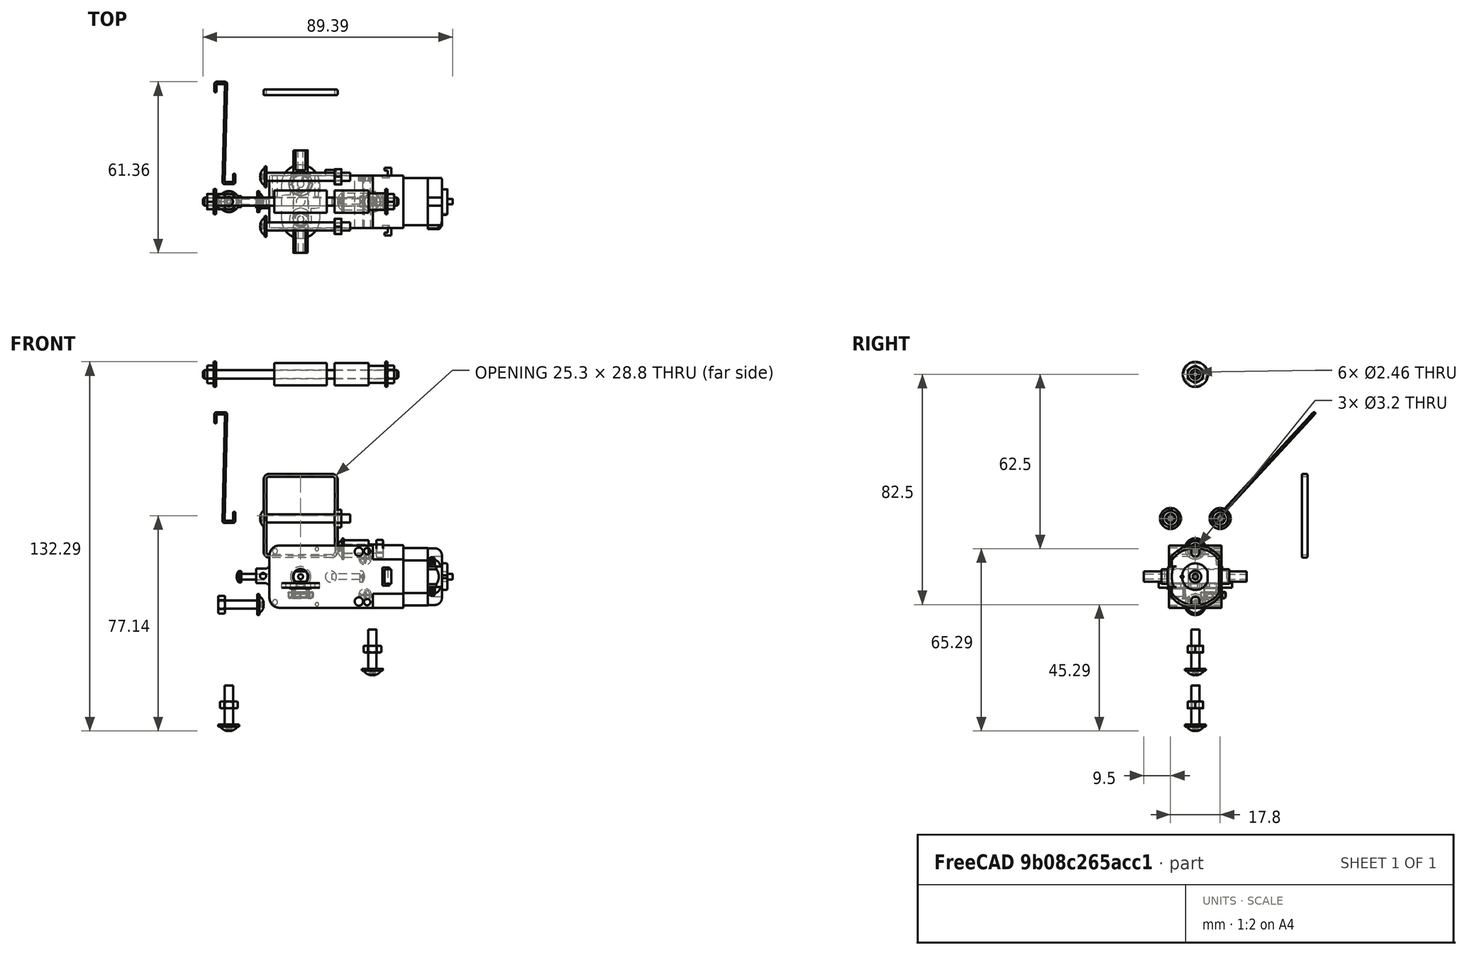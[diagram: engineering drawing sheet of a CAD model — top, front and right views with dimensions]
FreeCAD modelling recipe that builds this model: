
FCSTD DOCUMENT  (FreeCAD 0.21R33771 (Git))
Label: walking_robot_05_real_color
License: CERN Open Hardware Licence permissive
LicenseURL: https://cern-ohl.web.cern.ch/
objects: PartDesign::Body×27, PartDesign::SubShapeBinder×26, Sketcher::SketchObject×22, Part::FeaturePython×19, Part::Part2DObjectPython×19, PartDesign::Pad×15, PartDesign::FeatureBase×12, Part::Feature×10, PartDesign::Plane×7, App::DocumentObjectGroup×5, TechDraw::DrawViewDimension×5, PartDesign::FeaturePython×4, PartDesign::Fillet×3, Spreadsheet::Sheet×2, PartDesign::CoordinateSystem×2, Part::Box×2, Part::Cut×2, App::Part×2, PartDesign::Pocket×2, PartDesign::AdditivePipe×1, +4 more types
note: 199 computed .brp shape members not serialized (recipe doc carries the construction recipe); baked Part::Feature solids carry a one-line shape summary decoded from their .brp

FEATURE [Spreadsheet::Sheet] Spreadsheet
  cells = A1='acrylic_thick; B1(acrylic_thick)==4.9 mm; A2='acrylic_thin; B2(acrylic_thin)=2.8; A3='cam_length; B3(cam_length)=10; A4='angle; B4(angle)=270
FEATURE [Part::Feature] Compound002  label="motoreducteur001"
  Placement = pos=(25.85,-9.4,11.15) rot=(-1,0,0;1.5708rad)
  shape: bbox 70.34 x 38.2 x 22.5 mm, 234 faces, 3 solids (baked)
FEATURE [PartDesign::CoordinateSystem] Local_CS002
  AttacherType = Attacher::AttachEngine3D
  AttachmentOffset = pos=(0,0,0) rot=(0,-1,0;1.5708rad)
  MapMode = 11
  Placement = pos=(-2.8e-15,-19.1,1.8e-15) rot=(0,0,-1;1.5708rad)
  Support = -> [Compound002]
FEATURE [PartDesign::CoordinateSystem] Local_CS003
  AttacherType = Attacher::AttachEngine3D
  AttachmentOffset = pos=(0,0,0) rot=(0,1,0;1.5708rad)
  MapMode = 11
  Placement = pos=(-2.8e-15,19.1,1.9e-15) rot=(0,0,1;4.71239rad)
  Support = -> [Compound002]
FEATURE [PartDesign::SubShapeBinder] Binder
  BindCopyOnChange = 0
  BindMode = 0
  ClaimChildren = false
  Context = -> Body [Binder.]
  Fuse = false
  MakeFace = true
  OffsetFill = false
  OffsetIntersection = false
  OffsetJoinType = 0
  OffsetOpenResult = false
  PartialLoad = false
  Relative = true
  Support = -> [Part001]
  _Version = 2
FEATURE [Sketcher::SketchObject] Sketch
  ExternalGeometry = -> [Binder]
  FullyConstrained = true
  MapMode = 5
  Placement = pos=(-18.4,0,0) rot=(0.57735,-0.57735,-0.57735;2.0944rad)
  Support = -> [Binder]
  expr: Constraints[38] = Spreadsheet.cam_length
  expr: Constraints[81] = Spreadsheet.angle
  sketch-geometry (37):
    g0: ArcOfCircle CenterX=3.55 CenterY=5 CenterZ=0 NormalX=0 NormalY=0 NormalZ=1 AngleXU=0 Radius=0.4 StartAngle=0 EndAngle=3.14159
    g1: ArcOfCircle CenterX=3.55 CenterY=-5 CenterZ=0 NormalX=0 NormalY=0 NormalZ=1 AngleXU=0 Radius=0.4 StartAngle=3.14159 EndAngle=6.28319
    g2: LineSegment StartX=3.15 StartY=5 StartZ=0 EndX=3.15 EndY=-5 EndZ=0
    g3: LineSegment StartX=3.95 StartY=-5 StartZ=0 EndX=3.95 EndY=5 EndZ=0
    g4: ArcOfCircle CenterX=-3.55 CenterY=5 CenterZ=0 NormalX=0 NormalY=0 NormalZ=1 AngleXU=0 Radius=0.4 StartAngle=3e-16 EndAngle=3.14159
    g5: ArcOfCircle CenterX=-3.55 CenterY=-5 CenterZ=0 NormalX=0 NormalY=0 NormalZ=1 AngleXU=0 Radius=0.4 StartAngle=3.14159 EndAngle=6.28319
    g6: LineSegment StartX=-3.15 StartY=-5 StartZ=0 EndX=-3.15 EndY=5 EndZ=0
    g7: LineSegment StartX=3.55 StartY=5 StartZ=0 EndX=3.55 EndY=-5 EndZ=0
    g8: LineSegment StartX=-3.55 StartY=5 StartZ=0 EndX=-3.55 EndY=-5 EndZ=0
    g9: ArcOfCircle CenterX=1.55 CenterY=5 CenterZ=0 NormalX=0 NormalY=0 NormalZ=1 AngleXU=0 Radius=0.2 StartAngle=0 EndAngle=3.14159
    g10: ArcOfCircle CenterX=1.55 CenterY=-5 CenterZ=0 NormalX=0 NormalY=0 NormalZ=1 AngleXU=0 Radius=0.2 StartAngle=3.14159 EndAngle=6.28319
    g11: LineSegment StartX=1.35 StartY=5 StartZ=0 EndX=1.35 EndY=2.16333 EndZ=0
    g12: LineSegment StartX=1.75 StartY=-5 StartZ=0 EndX=1.75 EndY=5 EndZ=0
    g13: ArcOfCircle CenterX=-1.55 CenterY=5 CenterZ=0 NormalX=0 NormalY=0 NormalZ=1 AngleXU=0 Radius=0.2 StartAngle=5e-16 EndAngle=3.14159
    g14: ArcOfCircle CenterX=-1.55 CenterY=-5 CenterZ=0 NormalX=0 NormalY=0 NormalZ=1 AngleXU=0 Radius=0.2 StartAngle=3.14159 EndAngle=6.28319
    g15: LineSegment StartX=-1.75 StartY=5 StartZ=0 EndX=-1.75 EndY=-5 EndZ=0
    g16: LineSegment StartX=-1.35 StartY=-5 StartZ=0 EndX=-1.35 EndY=-2.16333 EndZ=0
    g17: LineSegment StartX=1.55 StartY=5 StartZ=0 EndX=1.55 EndY=-5 EndZ=0
    g18: LineSegment StartX=-1.55 StartY=5 StartZ=0 EndX=-1.55 EndY=-5 EndZ=0
    g19: LineSegment StartX=3.55 StartY=-4.2e-15 StartZ=0 EndX=1.55 EndY=-3.8e-15 EndZ=0
    g20: ArcOfCircle CenterX=9.6e-15 CenterY=5 CenterZ=0 NormalX=0 NormalY=0 NormalZ=1 AngleXU=0 Radius=7.5 StartAngle=0 EndAngle=3.14159
    g21: ArcOfCircle CenterX=6.9e-15 CenterY=-10 CenterZ=0 NormalX=0 NormalY=0 NormalZ=1 AngleXU=0 Radius=7.5 StartAngle=3.14159 EndAngle=6.28319
    g22: LineSegment StartX=-7.5 StartY=5 StartZ=0 EndX=-7.5 EndY=-10 EndZ=0
    g23: LineSegment StartX=7.5 StartY=-10 StartZ=0 EndX=7.5 EndY=5 EndZ=0
    g24: LineSegment StartX=8.7e-15 StartY=-3.6e-15 StartZ=0 EndX=9.6e-15 EndY=5 EndZ=0
    g25: LineSegment StartX=8.7e-15 StartY=-3.6e-15 StartZ=0 EndX=6.9e-15 EndY=-10 EndZ=0
    g26: Circle CenterX=6.9e-15 CenterY=-10 CenterZ=0 NormalX=0 NormalY=0 NormalZ=1 AngleXU=0 Radius=3.1
    g27: LineSegment StartX=-3.95 StartY=-5 StartZ=0 EndX=-3.95 EndY=5 EndZ=0
    g28: LineSegment StartX=1.55 StartY=-3.8e-15 StartZ=0 EndX=8.7e-15 EndY=-3.6e-15 EndZ=0
    g29: Circle CenterX=8.7e-15 CenterY=-3.6e-15 CenterZ=0 NormalX=0 NormalY=0 NormalZ=1 AngleXU=0 Radius=1.75
    g30: LineSegment StartX=-1.75 StartY=-4.1e-15 StartZ=0 EndX=-1.85 EndY=-4.1e-15 EndZ=0
    g31: LineSegment StartX=-3.55 StartY=-2.9e-15 StartZ=0 EndX=-1.55 EndY=-3.3e-15 EndZ=0
    g32: LineSegment StartX=8.7e-15 StartY=-3.6e-15 StartZ=0 EndX=-1.55 EndY=-3.3e-15 EndZ=0
    g33: LineSegment StartX=-1.35 StartY=2.16333 StartZ=0 EndX=-1.35 EndY=5 EndZ=0
    g34: LineSegment StartX=1.35 StartY=-2.16333 StartZ=0 EndX=1.35 EndY=-5 EndZ=0
    g35: ArcOfCircle CenterX=8.7e-15 CenterY=-3.6e-15 CenterZ=0 NormalX=0 NormalY=0 NormalZ=1 AngleXU=0 Radius=2.55 StartAngle=1.01289 EndAngle=2.1287
    g36: ArcOfCircle CenterX=8.7e-15 CenterY=-3.6e-15 CenterZ=0 NormalX=0 NormalY=0 NormalZ=1 AngleXU=0 Radius=2.55 StartAngle=4.15448 EndAngle=5.2703
  constraints (89):
    c: Tangent(g0,g2) = -1.5708
    c: Tangent(g2,g1) = -1.5708
    c: Tangent(g1,g3) = -1.5708
    c: Tangent(g5,g6) = -1.5708
    c: Tangent(g6,g4) = -1.5708
    c: Radius(g0) = 0.4
    c: Coincident(g7,g0)
    c: Coincident(g7,g1)
    c: Coincident(g8,g4)
    c: Coincident(g8,g5)
    c: Equal(g7,g8)
    c: Distance(g7) = 10
    c: Tangent(g9,g11) = -1.5708
    c: Tangent(g10,g12) = -1.5708
    c: Tangent(g12,g9) = -1.5708
    c: Tangent(g13,g15) = -1.5708
    c: Tangent(g15,g14) = -1.5708
    c: Tangent(g14,g16) = -1.5708
    c: Coincident(g17,g9)
    c: Coincident(g17,g10)
    c: Coincident(g18,g13)
    c: Coincident(g18,g14)
    c: Equal(g17,g7)
    c: Equal(g8,g18)
    c: Symmetric(g10,g9,g19)
    c: Distance(g19) = 2
    c: Perpendicular(g7,g19)
    c: Parallel(g17,g7)
    c: Parallel(g18,g8)
    c: Tangent(g20,g22) = -1.5708
    c: Tangent(g22,g21) = -1.5708
    c: Tangent(g21,g23) = -1.5708
    c: Tangent(g23,g20) = -1.5708
    c: Equal(g20,g21)
    c: Coincident(g24,g20)
    c: Coincident(g25,g21)
    c: Diameter(g20) = 15
    c: Distance(g24) = 5
    c: Distance(g25) = 10
    c: Coincident(g26,g21)
    c: Diameter(g26) = 6.2
    c: Tangent(g27,g4) = 1.5708
    c: Tangent(g27,g5) = 1.5708
    c: Symmetric(g0,g1,g19)
    c: Coincident(g28,g19)
    c: Parallel(g28,g19)
    c: Perpendicular(g28,g24)
    c: Tangent(g0,g3) = -1.5708
    c: PointOnObject(g30,g29)
    c: Horizontal(g30)
    c: Symmetric(g-5,g-5,g30)
    c: DistanceX(g30,g30) = 0.1
    c: Perpendicular(g25,g28)
    c: Symmetric(g14,g13,g31)
    c: Symmetric(g5,g4,g31)
    c: Equal(g31,g19)
    c: Coincident(g32,g31)
    c: Equal(g28,g32)
    c: Perpendicular(g32,g24)
    c: Perpendicular(g32,g18)
    c: Perpendicular(g18,g31)
    c: Tangent(g15,g29)
    c: PointOnObject(g34,g11)
    c: PointOnObject(g33,g-3)
    c: Parallel(g33,g17)
    c: Parallel(g17,g34)
    c: Tangent(g33,g13) = -1.5708
    c: Tangent(g34,g10) = -1.5708
    c: Coincident(g25,g32)
    c: Coincident(g25,g24)
    c: Coincident(g25,g28)
    c: Coincident(g24,g29)
    c: Coincident(g35,g24)
    c: Coincident(g35,g33)
    c: Coincident(g35,g11)
    c: Coincident(g36,g35)
    c: Coincident(g36,g34)
    c: Equal(g36,g-4)
    c: Coincident(g16,g36)
    c: Parallel(g16,g18)
    c: Coincident(g35,g-4)
    c: Angle(g25) = 4.71239
    c: Equal(g5,g1)
    c: Equal(g1,g4)
    c: Equal(g4,g0)
    c: Equal(g13,g9)
    c: Equal(g9,g14)
    c: Equal(g14,g10)
    c: Radius(g9) = 0.2
FEATURE [PartDesign::SubShapeBinder] Binder001
  BindCopyOnChange = 0
  BindMode = 0
  ClaimChildren = false
  Context = -> Body002 [Binder001.]
  Fuse = false
  MakeFace = true
  OffsetFill = false
  OffsetIntersection = false
  OffsetJoinType = 0
  OffsetOpenResult = false
  PartialLoad = false
  Relative = true
  Support = -> [Part001]
  _Version = 2
FEATURE [Part::Box] Box  label="Cube"
  AttacherType = Attacher::AttachEngine3D
  Height = 10
  Length = 10
  Placement = pos=(-5,18.4,-5) rot=(0,0,1;0rad)
  Width = 10
FEATURE [Part::Box] Box001  label="Cube001"
  AttacherType = Attacher::AttachEngine3D
  Height = 10
  Length = 10
  Placement = pos=(-5,-28.4,-5) rot=(0,0,1;0rad)
  Width = 10
FEATURE [Part::Cut] Cut
  Base = -> Compound002
  Tool = -> Box
FEATURE [Part::Cut] Cut001
  Base = -> Cut
  Tool = -> Box001
FEATURE [App::Part] Part001  label="Motor"
  Group = -> [Box001,Compound002,Local_CS002,Local_CS003,Box,Cut,Cut001]
  Origin = -> Origin004
  Placement = pos=(0,0,0) rot=(-0.57735,0.57735,-0.57735;4.18879rad)
FEATURE [PartDesign::Pad] Pad
  Direction = (-1,2e-16,-2e-16)
  Length = 2.8
  Length2 = 10
  Profile = -> Sketch
  ReferenceAxis = -> Sketch [N_Axis]
  Reversed = true
  Type = 0
  expr: Length = Spreadsheet.acrylic_thin
FEATURE [PartDesign::Body] Body  label="cam_right_1"
  Group = -> [Sketch,Binder,Pad]
  Origin = -> Origin001
  Tip = -> Pad
FEATURE [PartDesign::SubShapeBinder] Binder002
  BindCopyOnChange = 0
  BindMode = 0
  ClaimChildren = false
  Context = -> Body003 [Binder002.]
  Fuse = false
  MakeFace = true
  OffsetFill = false
  OffsetIntersection = false
  OffsetJoinType = 0
  OffsetOpenResult = false
  PartialLoad = false
  Relative = true
  Support = -> [Body]
  _Version = 2
FEATURE [PartDesign::Plane] DatumPlane001
  AttachmentOffset = pos=(0,0,0.1) rot=(0,0,1;0rad)
  Length = 60
  MapMode = 5
  Placement = pos=(-18.5,5.2e-15,-3.9e-15) rot=(-0.57735,0.57735,0.57735;4.18879rad)
  ResizeMode = 0
  Support = -> [Binder002]
  Width = 60
FEATURE [Sketcher::SketchObject] Sketch002
  ExternalGeometry = -> [Binder002]
  FullyConstrained = true
  MapMode = 5
  Placement = pos=(-18.5,5.2e-15,-3.9e-15) rot=(-0.57735,0.57735,0.57735;4.18879rad)
  Support = -> [DatumPlane001]
  sketch-geometry (6):
    g0: ArcOfCircle CenterX=-1.6948e-12 CenterY=5 CenterZ=0 NormalX=0 NormalY=0 NormalZ=1 AngleXU=0 Radius=7.5 StartAngle=2.58e-13 EndAngle=3.14159
    g1: ArcOfCircle CenterX=2.174e-12 CenterY=-10 CenterZ=0 NormalX=0 NormalY=0 NormalZ=1 AngleXU=0 Radius=7.5 StartAngle=3.14159 EndAngle=6.28319
    g2: LineSegment StartX=-7.5 StartY=5 StartZ=0 EndX=-7.5 EndY=-10 EndZ=0
    g3: LineSegment StartX=7.5 StartY=-10 StartZ=0 EndX=7.5 EndY=5 EndZ=0
    g4: Circle CenterX=2.174e-12 CenterY=-10 CenterZ=0 NormalX=0 NormalY=0 NormalZ=1 AngleXU=0 Radius=3.1
    g5: Circle CenterX=0 CenterY=0 CenterZ=0 NormalX=0 NormalY=0 NormalZ=1 AngleXU=0 Radius=1
  constraints (12):
    c: Tangent(g0,g2) = -1.5708
    c: Tangent(g2,g1) = -1.5708
    c: Tangent(g1,g3) = -1.5708
    c: Tangent(g3,g0) = -1.5708
    c: Equal(g0,g1)
    c: Coincident(g0,g-3)
    c: Coincident(g1,g-5)
    c: Equal(g0,g-3)
    c: Coincident(g4,g1)
    c: Equal(g4,g-5)
    c: Coincident(g5,g-6)
    c: Diameter(g5) = 2
FEATURE [PartDesign::Pad] Pad002
  Direction = (-1,2e-16,-2e-16)
  Length = 2.8
  Length2 = 10
  Placement = pos=(-18.5,5e-15,-4e-15) rot=(0.57735,-0.57735,-0.57735;2.0944rad)
  Profile = -> Sketch002
  ReferenceAxis = -> Sketch002 [N_Axis]
  Type = 0
  expr: Length = Spreadsheet.acrylic_thin
FEATURE [PartDesign::Body] Body003  label="cam_right_2"
  Group = -> [Binder002,DatumPlane001,Sketch002,Pad002]
  Origin = -> Origin
  Tip = -> Pad002
FEATURE [PartDesign::SubShapeBinder] Binder003
  BindCopyOnChange = 0
  BindMode = 0
  ClaimChildren = false
  Context = -> Body004 [Binder003.]
  Fuse = false
  MakeFace = true
  OffsetFill = false
  OffsetIntersection = false
  OffsetJoinType = 0
  OffsetOpenResult = false
  PartialLoad = false
  Relative = true
  Support = -> [Body003]
  _Version = 2
FEATURE [PartDesign::Plane] DatumPlane002
  AttachmentOffset = pos=(0,0,0.1) rot=(0,0,1;0rad)
  Length = 60
  MapMode = 5
  Placement = pos=(-21.4,5.3e-15,-1.05e-14) rot=(-0.57735,0.57735,0.57735;4.18879rad)
  ResizeMode = 0
  Support = -> [Binder003]
  Width = 60
FEATURE [Sketcher::SketchObject] Sketch003
  ExternalGeometry = -> [Binder003]
  FullyConstrained = true
  MapMode = 5
  Placement = pos=(-21.4,5.3e-15,-1.05e-14) rot=(-0.57735,0.57735,0.57735;4.18879rad)
  Support = -> [DatumPlane002]
  sketch-geometry (6):
    g0: ArcOfCircle CenterX=-1.6956e-12 CenterY=5 CenterZ=0 NormalX=0 NormalY=0 NormalZ=1 AngleXU=0 Radius=7.5 StartAngle=2.581e-13 EndAngle=3.14159
    g1: ArcOfCircle CenterX=2.1765e-12 CenterY=-10 CenterZ=0 NormalX=0 NormalY=0 NormalZ=1 AngleXU=0 Radius=7.5 StartAngle=3.14159 EndAngle=6.28319
    g2: LineSegment StartX=-7.5 StartY=5 StartZ=0 EndX=-7.5 EndY=-10 EndZ=0
    g3: LineSegment StartX=7.5 StartY=-10 StartZ=0 EndX=7.5 EndY=5 EndZ=0
    g4: Circle CenterX=2.1765e-12 CenterY=-10 CenterZ=0 NormalX=0 NormalY=0 NormalZ=1 AngleXU=0 Radius=3.1
    g5: Circle CenterX=0 CenterY=0 CenterZ=0 NormalX=0 NormalY=0 NormalZ=1 AngleXU=0 Radius=3
  constraints (12):
    c: Tangent(g0,g2) = -1.5708
    c: Tangent(g2,g1) = -1.5708
    c: Tangent(g1,g3) = -1.5708
    c: Tangent(g3,g0) = -1.5708
    c: Equal(g0,g1)
    c: Coincident(g0,g-3)
    c: Coincident(g1,g-5)
    c: Equal(g0,g-3)
    c: Coincident(g4,g1)
    c: Equal(g4,g-5)
    c: Coincident(g5,g-6)
    c: Diameter(g5) = 6
FEATURE [PartDesign::Pad] Pad003
  Direction = (-1,3e-16,-3e-16)
  Length = 2.8
  Length2 = 10
  Placement = pos=(-21.4,5e-15,-1e-14) rot=(0.57735,-0.57735,-0.57735;2.0944rad)
  Profile = -> Sketch003
  ReferenceAxis = -> Sketch003 [N_Axis]
  Type = 0
  expr: Length = Spreadsheet.acrylic_thin
FEATURE [PartDesign::Body] Body004  label="cam_right_3"
  Group = -> [Binder003,DatumPlane002,Sketch003,Pad003]
  Origin = -> Origin005
  Tip = -> Pad003
FEATURE [PartDesign::SubShapeBinder] Binder004
  BindCopyOnChange = 0
  BindMode = 0
  ClaimChildren = false
  Context = -> Body002 [Binder004.]
  Fuse = false
  MakeFace = true
  OffsetFill = false
  OffsetIntersection = false
  OffsetJoinType = 0
  OffsetOpenResult = false
  PartialLoad = false
  Relative = true
  Support = -> [Body004]
  _Version = 2
FEATURE [PartDesign::Plane] DatumPlane003
  AttachmentOffset = pos=(0,0,0.1) rot=(0,0,1;0rad)
  Length = 66.5529
  MapMode = 5
  Placement = pos=(-24.3,8.3e-15,-1.41e-14) rot=(-0.57735,0.57735,0.57735;4.18879rad)
  ResizeMode = 0
  Support = -> [Binder004]
  Width = 153.553
FEATURE [Sketcher::SketchObject] Sketch001
  ExternalGeometry = -> [Binder004]
  FullyConstrained = false
  MapMode = 5
  Placement = pos=(-24.3,8.3e-15,-1.41e-14) rot=(-0.57735,0.57735,0.57735;4.18879rad)
  Support = -> [DatumPlane003]
  expr: Constraints[92] = Spreadsheet.angle
  expr: Constraints[98] = Spreadsheet.acrylic_thin
  sketch-geometry (38):
    g0: LineSegment StartX=-10 StartY=84 StartZ=0 EndX=10 EndY=84 EndZ=0
    g1: LineSegment StartX=10 StartY=84 StartZ=0 EndX=10 EndY=-53 EndZ=0
    g2: LineSegment StartX=10 StartY=-53 StartZ=0 EndX=-10 EndY=-53 EndZ=0
    g3: LineSegment StartX=-10 StartY=-53 StartZ=0 EndX=-10 EndY=84 EndZ=0
    g4: LineSegment StartX=4e-15 StartY=-10 StartZ=0 EndX=-10 EndY=-10 EndZ=0
    g5: LineSegment StartX=4e-15 StartY=-10 StartZ=0 EndX=10 EndY=-10 EndZ=0
    g6: ArcOfCircle CenterX=-2e-16 CenterY=75 CenterZ=0 NormalX=0 NormalY=0 NormalZ=1 AngleXU=0 Radius=3.1 StartAngle=2e-16 EndAngle=3.14159
    g7: ArcOfCircle CenterX=6e-16 CenterY=50 CenterZ=0 NormalX=0 NormalY=0 NormalZ=1 AngleXU=0 Radius=3.1 StartAngle=3.14159 EndAngle=6.28319
    g8: LineSegment StartX=-3.1 StartY=75 StartZ=0 EndX=-3.1 EndY=50 EndZ=0
    g9: LineSegment StartX=3.1 StartY=50 StartZ=0 EndX=3.1 EndY=75 EndZ=0
    g10: LineSegment StartX=-2e-16 StartY=75 StartZ=0 EndX=-4e-16 EndY=84 EndZ=0
    g11: Circle CenterX=4e-15 CenterY=-10 CenterZ=0 NormalX=0 NormalY=0 NormalZ=1 AngleXU=0 Radius=1.55
    g12: LineSegment StartX=0 StartY=0 StartZ=0 EndX=4e-15 EndY=-10 EndZ=0
    g13: Circle CenterX=0 CenterY=71 CenterZ=0 NormalX=0 NormalY=0 NormalZ=1 AngleXU=0 Radius=3.1
    g14: LineSegment StartX=0 StartY=71 StartZ=0 EndX=0 EndY=0 EndZ=0
    g15: LineSegment StartX=6e-16 StartY=50 StartZ=0 EndX=1e-16 EndY=62.5 EndZ=0
    g16: LineSegment StartX=-2e-16 StartY=75 StartZ=0 EndX=1e-16 EndY=62.5 EndZ=0
    g17: LineSegment StartX=-10 StartY=-53 StartZ=0 EndX=-6 EndY=-53 EndZ=0
    g18: LineSegment StartX=-6 StartY=-53 StartZ=0 EndX=-6 EndY=-50.2 EndZ=0
    g19: LineSegment StartX=-6 StartY=-50.2 StartZ=0 EndX=-1.25 EndY=-50.2 EndZ=0
    g20: LineSegment StartX=-1.25 StartY=-50.2 StartZ=0 EndX=-1.25 EndY=-47.2 EndZ=0
    g21: LineSegment StartX=-1.25 StartY=-47.2 StartZ=0 EndX=-2.75 EndY=-47.2 EndZ=0
    g22: LineSegment StartX=-2.75 StartY=-47.2 StartZ=0 EndX=-2.75 EndY=-44.7 EndZ=0
    g23: LineSegment StartX=-2.75 StartY=-44.7 StartZ=0 EndX=-1.25 EndY=-44.7 EndZ=0
    g24: LineSegment StartX=-1.25 StartY=-44.7 StartZ=0 EndX=-1.25 EndY=-37.7 EndZ=0
    g25: LineSegment StartX=-1.25 StartY=-37.7 StartZ=0 EndX=1.25 EndY=-37.7 EndZ=0
    g26: LineSegment StartX=1.25 StartY=-37.7 StartZ=0 EndX=1.25 EndY=-44.7 EndZ=0
    g27: LineSegment StartX=1.25 StartY=-44.7 StartZ=0 EndX=2.75 EndY=-44.7 EndZ=0
    g28: LineSegment StartX=2.75 StartY=-44.7 StartZ=0 EndX=2.75 EndY=-47.2 EndZ=0
    g29: LineSegment StartX=2.75 StartY=-47.2 StartZ=0 EndX=1.25 EndY=-47.2 EndZ=0
    g30: LineSegment StartX=1.25 StartY=-47.2 StartZ=0 EndX=1.25 EndY=-50.2 EndZ=0
    g31: LineSegment StartX=1.25 StartY=-50.2 StartZ=0 EndX=6 EndY=-50.2 EndZ=0
    g32: LineSegment StartX=6 StartY=-50.2 StartZ=0 EndX=6 EndY=-53 EndZ=0
    g33: LineSegment StartX=6 StartY=-53 StartZ=0 EndX=10 EndY=-53 EndZ=0
    g34: LineSegment StartX=-7 StartY=-10 StartZ=0 EndX=-7 EndY=20 EndZ=0
    g35: LineSegment StartX=7 StartY=20 StartZ=0 EndX=7 EndY=-10 EndZ=0
    g36: Circle CenterX=-7 CenterY=20 CenterZ=0 NormalX=0 NormalY=0 NormalZ=1 AngleXU=0 Radius=0.6
    g37: Circle CenterX=7 CenterY=20 CenterZ=0 NormalX=0 NormalY=0 NormalZ=1 AngleXU=0 Radius=0.6
  constraints (105):
    c: Coincident(g0,g1)
    c: Coincident(g1,g2)
    c: Coincident(g2,g3)
    c: Coincident(g3,g0)
    c: Distance(g0) = 20
    c: Perpendicular(g3,g0)
    c: Perpendicular(g1,g2)
    c: Perpendicular(g2,g3)
    c: PointOnObject(g4,g3)
    c: PointOnObject(g5,g1)
    c: Perpendicular(g1,g5)
    c: Perpendicular(g3,g4)
    c: Equal(g4,g5)
    c: Distance(g3) = 137
    c: Tangent(g6,g8) = -1.5708
    c: Tangent(g8,g7) = -1.5708
    c: Tangent(g7,g9) = -1.5708
    c: Tangent(g9,g6) = -1.5708
    c: Equal(g6,g7)
    c: Diameter(g7) = 6.2
    c: Distance(g6,g7) = 25
    c: Coincident(g10,g6)
    c: Perpendicular(g0,g10)
    c: Distance(g10) = 9
    c: Symmetric(g0,g0,g10)
    c: Parallel(g8,g3)
    c: Diameter(g11) = 3.1
    c: Coincident(g14,g13)
    c: DistanceY(g14,g14) = 71
    c: Coincident(g14,g12)
    c: Coincident(g15,g7)
    c: Coincident(g16,g6)
    c: Coincident(g16,g15)
    c: Equal(g16,g15)
    c: Parallel(g16,g8)
    c: Tangent(g13,g9)
    c: Vertical(g14)
    c: Coincident(g17,g3)
    c: Coincident(g17,g18)
    c: Coincident(g18,g19)
    c: Coincident(g19,g20)
    c: Coincident(g20,g21)
    c: Coincident(g21,g22)
    c: Coincident(g22,g23)
    c: Coincident(g23,g24)
    c: Coincident(g24,g25)
    c: Coincident(g25,g26)
    c: Coincident(g26,g27)
    c: Coincident(g27,g28)
    c: Coincident(g28,g29)
    c: Coincident(g29,g30)
    c: Coincident(g30,g31)
    c: Coincident(g31,g32)
    c: Coincident(g32,g33)
    c: Coincident(g33,g1)
    c: Perpendicular(g17,g3)
    c: Perpendicular(g33,g1)
    c: Perpendicular(g32,g33)
    c: Perpendicular(g17,g18)
    c: Perpendicular(g19,g18)
    c: Perpendicular(g32,g31)
    c: Perpendicular(g31,g30)
    c: Perpendicular(g19,g20)
    c: Perpendicular(g29,g30)
    c: Perpendicular(g20,g21)
    c: Perpendicular(g28,g29)
    c: Perpendicular(g22,g21)
    c: Perpendicular(g28,g27)
    c: Perpendicular(g23,g22)
    c: Perpendicular(g27,g26)
    c: Perpendicular(g24,g23)
    c: Equal(g18,g32)
    c: Equal(g30,g20)
    c: Equal(g29,g21)
    c: Equal(g23,g27)
    c: Equal(g19,g31)
    c: Distance(g22,g27) = 5.5
    c: Equal(g25,g22)
    c: Equal(g22,g28)
    c: Distance(g24) = 7
    c: Perpendicular(g25,g26)
    c: Equal(g21,g23)
    c: PointOnObject(g34,g4)
    c: Equal(g34,g35)
    c: Distance(g34,g4) = 3
    c: Coincident(g36,g34)
    c: Coincident(g37,g35)
    c: Equal(g37,g36)
    c: Diameter(g37) = 1.2
    c: Distance(g34) = 30
    c: Perpendicular(g5,g35)
    c: Perpendicular(g4,g34)
    c: Angle(g12) = 4.71239
    c: Equal(g17,g33)
    c: Distance(g17) = 4
    c: DistanceY(g3,g12) = 53
    c: Coincident(g12,g-1)
    c: DistanceY(g22,g22) = 2.5
    c: DistanceY(g18,g18) = 2.8
    c: DistanceY(g20,g20) = 3
    c: Equal(g7,g13)
    c: Coincident(g4,g5)
    c: Coincident(g4,g12)
    c: Coincident(g4,g-3)
    c: Coincident(g4,g11)
FEATURE [PartDesign::Pad] Pad004
  Direction = (-1,5e-16,-5e-16)
  Length = 2.8
  Length2 = 10
  Placement = pos=(-24.3,8e-15,-1.4e-14) rot=(0.57735,-0.57735,-0.57735;2.0944rad)
  Profile = -> Sketch001
  ReferenceAxis = -> Sketch001 [N_Axis]
  Type = 0
  expr: Length = Spreadsheet.acrylic_thin
FEATURE [PartDesign::SubShapeBinder] Binder005
  BindCopyOnChange = 0
  BindMode = 0
  ClaimChildren = false
  Context = -> Body005 [Binder005.]
  Fuse = false
  MakeFace = true
  OffsetFill = false
  OffsetIntersection = false
  OffsetJoinType = 0
  OffsetOpenResult = false
  PartialLoad = false
  Relative = true
  Support = -> [Body004]
  _Version = 2
FEATURE [Part::FeaturePython] Screw  label="M3x14-Screw"  # Fasteners workbench fastener (typed FeaturePython)
  Placement = pos=(-15.5,7.6099e-12,-10) rot=(0,1,0;1.5708rad)
  diameter = 1
  invert = false
  leftHanded = false
  length = 6
  lengthCustom = 14
  matchOuter = false
  offset = 0
  thread = false
  type = 25
FEATURE [Part::FeaturePython] Nut  label="M3-Nut"  # Fasteners workbench fastener (typed FeaturePython)
  Placement = pos=(-29.5,7.6239e-12,-10) rot=(0,1,0;1.5708rad)
  baseObject = -> Screw [Edge71]
  diameter = 4
  invert = false
  leftHanded = false
  matchOuter = false
  offset = 0
  thread = false
  type = 25
FEATURE [PartDesign::SubShapeBinder] Binder008
  BindCopyOnChange = 0
  BindMode = 0
  ClaimChildren = false
  Context = -> Body005 [Binder008.]
  Fuse = false
  MakeFace = true
  OffsetFill = false
  OffsetIntersection = false
  OffsetJoinType = 0
  OffsetOpenResult = false
  PartialLoad = false
  Relative = true
  Support = -> [Body002[Pad004.]]
  _Version = 2
FEATURE [Sketcher::SketchObject] Sketch004
  ExternalGeometry = -> [Binder005]
  FullyConstrained = true
  MapMode = 5
  Placement = pos=(-24.3,-1.36e-14,-3.65e-14) rot=(0.57735,0.57735,0.57735;2.0944rad)
  Support = -> [Binder008]
  sketch-geometry (2):
    g0: Circle CenterX=-2.172e-12 CenterY=-10 CenterZ=0 NormalX=0 NormalY=0 NormalZ=1 AngleXU=0 Radius=3
    g1: Circle CenterX=-2.172e-12 CenterY=-10 CenterZ=0 NormalX=0 NormalY=0 NormalZ=1 AngleXU=0 Radius=1.6
  constraints (4):
    c: Diameter(g1) = 3.2
    c: Diameter(g0) = 6
    c: Coincident(g1,g-3)
    c: Coincident(g0,g1)
FEATURE [PartDesign::Pad] Pad005
  Direction = (1,0,4e-16)
  Length = 8.8
  Length2 = 10
  Profile = -> Sketch004
  ReferenceAxis = -> Sketch004 [N_Axis]
  Type = 0
FEATURE [PartDesign::Body] Body005  label="spacer_right"
  Group = -> [Binder005,Sketch004,Pad005,Binder008]
  Origin = -> Origin006
  Tip = -> Pad005
FEATURE [PartDesign::SubShapeBinder] Binder009
  BindCopyOnChange = 0
  BindMode = 0
  ClaimChildren = false
  Context = -> Body007 [Binder009.]
  Fuse = false
  MakeFace = true
  OffsetFill = false
  OffsetIntersection = false
  OffsetJoinType = 0
  OffsetOpenResult = false
  PartialLoad = false
  Relative = true
  Support = -> [Body002[Pad004.]]
  _Version = 2
FEATURE [PartDesign::Plane] DatumPlane
  Length = 74.3266
  MapMode = 5
  Placement = pos=(5.3e-14,-1.145e-13,-53) rot=(1,0,0;3.14159rad)
  ResizeMode = 0
  Support = -> [Binder009]
  Width = 119.627
FEATURE [Sketcher::SketchObject] Sketch006
  ExternalGeometry = -> [Binder009]
  FullyConstrained = true
  MapMode = 5
  Placement = pos=(5.3e-14,-1.145e-13,-53) rot=(0,0,1;3.14159rad)
  Support = -> [DatumPlane]
  sketch-geometry (51):
    g0: LineSegment StartX=-12.3 StartY=40 StartZ=0 EndX=25.7 EndY=40 EndZ=0
    g1: LineSegment StartX=25.7 StartY=40 StartZ=0 EndX=25.7 EndY=0 EndZ=0
    g2: LineSegment StartX=25.7 StartY=0 StartZ=0 EndX=25.7 EndY=-56 EndZ=0
    g3: LineSegment StartX=25.7 StartY=-56 StartZ=0 EndX=-12.3 EndY=-56 EndZ=0
    g4: ArcOfCircle CenterX=-12.3 CenterY=40 CenterZ=0 NormalX=0 NormalY=0 NormalZ=1 AngleXU=0 Radius=4 StartAngle=1.5708 EndAngle=4.71239
    g5: ArcOfCircle CenterX=-12.3 CenterY=-56 CenterZ=0 NormalX=0 NormalY=0 NormalZ=1 AngleXU=0 Radius=4 StartAngle=1.5708 EndAngle=4.71239
    g6: LineSegment StartX=-12.3 StartY=44 StartZ=0 EndX=25.7 EndY=44 EndZ=0
    g7: LineSegment StartX=-12.3 StartY=36 StartZ=0 EndX=15.7 EndY=36 EndZ=0
    g8: LineSegment StartX=-12.3 StartY=-52 StartZ=0 EndX=15.7 EndY=-52 EndZ=0
    g9: LineSegment StartX=-12.3 StartY=-60 StartZ=0 EndX=25.7 EndY=-60 EndZ=0
    g10: ArcOfCircle CenterX=25.7 CenterY=10.1 CenterZ=0 NormalX=0 NormalY=0 NormalZ=1 AngleXU=0 Radius=8 StartAngle=0 EndAngle=0.895665
    g11: ArcOfCircle CenterX=25.7 CenterY=-9.9 CenterZ=0 NormalX=0 NormalY=0 NormalZ=1 AngleXU=0 Radius=8 StartAngle=3.14159 EndAngle=4.03726
    g12: LineSegment StartX=17.7 StartY=10.1 StartZ=0 EndX=17.7 EndY=-9.9 EndZ=0
    g13: LineSegment StartX=33.7 StartY=-9.9 StartZ=0 EndX=33.7 EndY=10.1 EndZ=0
    g14: LineSegment StartX=20.7 StartY=31 StartZ=0 EndX=20.7 EndY=16.345 EndZ=0
    g15: LineSegment StartX=30.7 StartY=16.345 StartZ=0 EndX=30.7 EndY=39 EndZ=0
    g16: ArcOfCircle CenterX=25.7 CenterY=39 CenterZ=0 NormalX=0 NormalY=0 NormalZ=1 AngleXU=0 Radius=5 StartAngle=0 EndAngle=1.5708
    g17: LineSegment StartX=20.7 StartY=-47 StartZ=0 EndX=20.7 EndY=-16.145 EndZ=0
    g18: LineSegment StartX=30.7 StartY=-16.145 StartZ=0 EndX=30.7 EndY=-55 EndZ=0
    g19: ArcOfCircle CenterX=25.7 CenterY=-55 CenterZ=0 NormalX=0 NormalY=0 NormalZ=1 AngleXU=0 Radius=5 StartAngle=4.71239 EndAngle=6.28319
    g20: ArcOfCircle CenterX=25.7 CenterY=-9.9 CenterZ=0 NormalX=0 NormalY=0 NormalZ=1 AngleXU=0 Radius=8 StartAngle=5.38752 EndAngle=6.28319
    g21: ArcOfCircle CenterX=25.7 CenterY=10.1 CenterZ=0 NormalX=0 NormalY=0 NormalZ=1 AngleXU=0 Radius=8 StartAngle=2.24593 EndAngle=3.14159
    g22: Circle CenterX=25.7 CenterY=0 CenterZ=0 NormalX=0 NormalY=0 NormalZ=1 AngleXU=0 Radius=1.55
    g23: LineSegment StartX=24.2 StartY=10.1 StartZ=0 EndX=27.2 EndY=10.1 EndZ=0
    g24: LineSegment StartX=27.2 StartY=10.1 StartZ=0 EndX=27.2 EndY=6.1 EndZ=0
    g25: LineSegment StartX=27.2 StartY=6.1 StartZ=0 EndX=24.2 EndY=6.1 EndZ=0
    g26: LineSegment StartX=24.2 StartY=6.1 StartZ=0 EndX=24.2 EndY=10.1 EndZ=0
    g27: LineSegment StartX=24.3 StartY=10 StartZ=0 EndX=24.3 EndY=10.1 EndZ=0
    g28: LineSegment StartX=24.3 StartY=10 StartZ=0 EndX=24.2 EndY=10 EndZ=0
    g29: LineSegment StartX=27.1 StartY=6 StartZ=0 EndX=27.2 EndY=6 EndZ=0
    g30: LineSegment StartX=27.1 StartY=6 StartZ=0 EndX=27.1 EndY=6.1 EndZ=0
    g31: LineSegment StartX=24.2 StartY=-5.9 StartZ=0 EndX=27.2 EndY=-5.9 EndZ=0
    g32: LineSegment StartX=27.2 StartY=-5.9 StartZ=0 EndX=27.2 EndY=-9.9 EndZ=0
    g33: LineSegment StartX=27.2 StartY=-9.9 StartZ=0 EndX=24.2 EndY=-9.9 EndZ=0
    g34: LineSegment StartX=24.2 StartY=-9.9 StartZ=0 EndX=24.2 EndY=-5.9 EndZ=0
    g35: LineSegment StartX=24.3 StartY=-6 StartZ=0 EndX=24.3 EndY=-5.9 EndZ=0
    g36: LineSegment StartX=24.3 StartY=-6 StartZ=0 EndX=24.2 EndY=-6 EndZ=0
    g37: LineSegment StartX=27.1 StartY=-10 StartZ=0 EndX=27.2 EndY=-10 EndZ=0
    g38: LineSegment StartX=27.1 StartY=-10 StartZ=0 EndX=27.1 EndY=-9.9 EndZ=0
    g39: ArcOfCircle CenterX=15.7 CenterY=-47 CenterZ=0 NormalX=0 NormalY=0 NormalZ=1 AngleXU=0 Radius=5 StartAngle=4.71239 EndAngle=6.28319
    g40: GeomPoint X=20.7 Y=-52 Z=0
    g41: ArcOfCircle CenterX=15.7 CenterY=31 CenterZ=0 NormalX=0 NormalY=0 NormalZ=1 AngleXU=0 Radius=5 StartAngle=0 EndAngle=1.5708
    g42: GeomPoint X=20.7 Y=36 Z=0
    g43: LineSegment StartX=24.2 StartY=10.1 StartZ=0 EndX=17.7 EndY=10.1 EndZ=0
    g44: LineSegment StartX=27.2 StartY=10.1 StartZ=0 EndX=33.7 EndY=10.1 EndZ=0
    g45: LineSegment StartX=24.2 StartY=-9.9 StartZ=0 EndX=17.7 EndY=-9.9 EndZ=0
    g46: LineSegment StartX=27.2 StartY=-9.9 StartZ=0 EndX=33.7 EndY=-9.9 EndZ=0
    g47: LineSegment StartX=24.3 StartY=1.25 StartZ=0 EndX=24.3 EndY=-1.25 EndZ=0
    g48: LineSegment StartX=27.1 StartY=1.25 StartZ=0 EndX=27.1 EndY=-1.25 EndZ=0
    g49: LineSegment StartX=24.3 StartY=1e-15 StartZ=0 EndX=25.7 EndY=0 EndZ=0
    g50: LineSegment StartX=25.7 StartY=0 StartZ=0 EndX=27.1 EndY=1e-15 EndZ=0
  constraints (133):
    c: Horizontal(g0)
    c: Coincident(g0,g1)
    c: Vertical(g1)
    c: Coincident(g1,g2)
    c: Vertical(g2)
    c: Coincident(g2,g3)
    c: Horizontal(g3)
    c: DistanceY(g2,g2) = 56
    c: Equal(g3,g0)
    c: DistanceX(g0,g0) = 38
    c: Coincident(g4,g0)
    c: Coincident(g5,g3)
    c: Equal(g5,g4)
    c: Diameter(g5) = 8
    c: Horizontal(g6)
    c: Horizontal(g7)
    c: Tangent(g4,g6) = 1.5708
    c: Tangent(g4,g7) = -1.5708
    c: Distance(g42,g1) = 5
    c: Horizontal(g8)
    c: Horizontal(g9)
    c: Tangent(g5,g8) = 1.5708
    c: Tangent(g5,g9) = -1.5708
    c: Equal(g6,g9)
    c: Tangent(g12,g11) = -1.5708
    c: Tangent(g13,g10) = -1.5708
    c: Equal(g10,g11)
    c: Diameter(g10) = 16
    c: Vertical(g14)
    c: PointOnObject(g6,g1)
    c: Vertical(g15)
    c: Tangent(g15,g16) = -1.5708
    c: Tangent(g16,g6) = 1.5708
    c: Distance(g15,g1) = 5
    c: Vertical(g17)
    c: Vertical(g18)
    c: Distance(g18,g2) = 5
    c: Tangent(g19,g9) = -1.5708
    c: Tangent(g19,g18) = 1.5708
    c: Equal(g11,g20)
    c: Coincident(g11,g17)
    c: Coincident(g20,g18)
    c: Coincident(g11,g20)
    c: Tangent(g20,g13) = -1.5708
    c: Equal(g10,g21)
    c: Coincident(g21,g14)
    c: Coincident(g10,g21)
    c: Coincident(g10,g15)
    c: Tangent(g21,g12) = -1.5708
    c: Coincident(g22,g1)
    c: Diameter(g22) = 3.1
    c: Coincident(g23,g24)
    c: Coincident(g24,g25)
    c: Coincident(g25,g26)
    c: Coincident(g26,g23)
    c: Coincident(g28,g27)
    c: Coincident(g30,g29)
    c: Equal(g28,g27)
    c: Equal(g27,g30)
    c: Equal(g30,g29)
    c: Coincident(g31,g32)
    c: Coincident(g32,g33)
    c: Coincident(g33,g34)
    c: Coincident(g34,g31)
    c: Coincident(g36,g35)
    c: Coincident(g38,g37)
    c: Coincident(g37,g-5)
    c: Coincident(g35,g-6)
    c: Coincident(g-4,g29)
    c: Coincident(g27,g-3)
    c: PointOnObject(g40,g8)
    c: PointOnObject(g40,g17)
    c: Tangent(g8,g39) = -1.5708
    c: Tangent(g17,g39) = -1.5708
    c: Radius(g39) = 5
    c: Symmetric(g11,g18,g2)
    c: PointOnObject(g42,g7)
    c: PointOnObject(g42,g14)
    c: Tangent(g7,g41) = 1.5708
    c: Tangent(g14,g41) = 1.5708
    c: Equal(g41,g39)
    c: DistanceY(g1,g1) = 40
    c: Distance(g27) = 0.1
    c: Perpendicular(g-3,g27)
    c: Perpendicular(g28,g27)
    c: PointOnObject(g28,g26)
    c: PointOnObject(g27,g23)
    c: Perpendicular(g28,g26)
    c: Perpendicular(g23,g27)
    c: Perpendicular(g-4,g30)
    c: Perpendicular(g29,g30)
    c: PointOnObject(g29,g24)
    c: PointOnObject(g30,g25)
    c: Perpendicular(g25,g30)
    c: Perpendicular(g29,g24)
    c: Perpendicular(g-5,g38)
    c: Perpendicular(g37,g38)
    c: Perpendicular(g35,g-6)
    c: Perpendicular(g36,g35)
    c: Equal(g35,g36)
    c: Equal(g36,g37)
    c: Equal(g37,g38)
    c: Equal(g38,g27)
    c: PointOnObject(g35,g31)
    c: PointOnObject(g36,g34)
    c: Perpendicular(g34,g36)
    c: Perpendicular(g31,g35)
    c: PointOnObject(g38,g33)
    c: PointOnObject(g37,g32)
    c: Perpendicular(g32,g37)
    c: Perpendicular(g33,g38)
    c: Coincident(g43,g23)
    c: Coincident(g43,g12)
    c: Coincident(g44,g23)
    c: Coincident(g44,g10)
    c: Perpendicular(g44,g24)
    c: Perpendicular(g43,g26)
    c: Coincident(g45,g33)
    c: Coincident(g45,g11)
    c: Coincident(g46,g32)
    c: Coincident(g46,g13)
    c: Perpendicular(g32,g46)
    c: Coincident(g47,g-8)
    c: Coincident(g47,g-7)
    c: Coincident(g48,g-8)
    c: Coincident(g48,g-7)
    c: Coincident(g50,g49)
    c: PointOnObject(g50,g48)
    c: Equal(g49,g50)
    c: Perpendicular(g49,g47)
    c: Perpendicular(g48,g50)
    c: Symmetric(g47,g47,g49)
    c: Coincident(g22,g49)
FEATURE [PartDesign::Pad] Pad006
  Direction = (-6e-16,2.1e-15,1)
  Length = 2.8
  Length2 = 10
  Placement = pos=(2.9e-14,-1.09e-13,-53) rot=(1,0,0;3.14159rad)
  Profile = -> Sketch006
  ReferenceAxis = -> Sketch006 [N_Axis]
  Type = 0
  expr: Length = Spreadsheet.acrylic_thin
FEATURE [PartDesign::Body] Body007  label="feet_right"
  Group = -> [Sketch006,Binder009,DatumPlane,Pad006]
  Origin = -> Origin009
  Tip = -> Pad006
FEATURE [PartDesign::FeatureBase] Clone
  BaseFeature = -> Body
FEATURE [PartDesign::Body] Body008  label="cam_left_1"
  Group = -> [Clone]
  Origin = -> Origin010
  Placement = pos=(0,0,0) rot=(0,1,0;3.14159rad)
  Tip = -> Clone
FEATURE [PartDesign::FeatureBase] Clone001
  BaseFeature = -> Body003
FEATURE [PartDesign::Body] Body009  label="cam_left_2"
  Group = -> [Clone001]
  Origin = -> Origin011
  Placement = pos=(0,0,0) rot=(0,1,0;3.14159rad)
  Tip = -> Clone001
FEATURE [PartDesign::FeatureBase] Clone002
  BaseFeature = -> Body004
FEATURE [PartDesign::Body] Body010  label="cam_left_3"
  Group = -> [Clone002]
  Origin = -> Origin012
  Placement = pos=(0,0,0) rot=(0,1,0;3.14159rad)
  Tip = -> Clone002
FEATURE [PartDesign::FeatureBase] Clone003
  BaseFeature = -> Body005
FEATURE [PartDesign::Body] Body011  label="spacer_left"
  Group = -> [Clone003]
  Origin = -> Origin013
  Placement = pos=(0,0,0) rot=(0,1,0;3.14159rad)
  Tip = -> Clone003
FEATURE [PartDesign::FeatureBase] Clone007
  BaseFeature = -> Body007
FEATURE [PartDesign::Body] Body015  label="feet_left"
  Group = -> [Clone007]
  Origin = -> Origin017
  Placement = pos=(1e-14,0,-83.2) rot=(0,1,0;3.14159rad)
  Tip = -> Clone007
FEATURE [PartDesign::Fillet] Fillet
  Base = -> Pad004 [Edge1,Edge2,Edge11,Edge14,Edge53,Edge20,Edge38,Edge35,Edge50,Edge23,Edge41,Edge32,Edge26,Edge47,Edge44,Edge29]
  BaseFeature = -> Pad004
  Placement = pos=(-24.3,8e-15,-1.4e-14) rot=(0.57735,-0.57735,-0.57735;2.0944rad)
  Radius = 0.4
  SupportTransform = false
  UseAllEdges = false
FEATURE [PartDesign::Fillet] Fillet001
  Base = -> Fillet [Edge91,Edge93]
  BaseFeature = -> Fillet
  Placement = pos=(-24.3,8e-15,-1.4e-14) rot=(0.57735,-0.57735,-0.57735;2.0944rad)
  Radius = 5
  SupportTransform = false
  UseAllEdges = false
FEATURE [PartDesign::SubShapeBinder] Binder010
  BindCopyOnChange = 0
  BindMode = 0
  ClaimChildren = false
  Context = -> Body017 [Binder010.]
  Fuse = false
  MakeFace = true
  OffsetFill = false
  OffsetIntersection = false
  OffsetJoinType = 0
  OffsetOpenResult = false
  PartialLoad = false
  Relative = true
  Support = -> [Part001]
  _Version = 2
FEATURE [PartDesign::SubShapeBinder] Binder011
  BindCopyOnChange = 0
  BindMode = 0
  ClaimChildren = false
  Context = -> Body017 [Binder011.]
  Fuse = false
  MakeFace = true
  OffsetFill = false
  OffsetIntersection = false
  OffsetJoinType = 0
  OffsetOpenResult = false
  PartialLoad = false
  Relative = true
  Support = -> [Body002]
  _Version = 2
FEATURE [PartDesign::SubShapeBinder] Binder012
  BindCopyOnChange = 0
  BindMode = 0
  ClaimChildren = false
  Context = -> Body017 [Binder012.]
  Fuse = false
  MakeFace = true
  OffsetFill = false
  OffsetIntersection = false
  OffsetJoinType = 0
  OffsetOpenResult = false
  PartialLoad = false
  Relative = true
  Support = -> [Body014]
  _Version = 2
FEATURE [Sketcher::SketchObject] Sketch007
  ExternalGeometry = -> [Binder010,Binder011,Binder012]
  FullyConstrained = true
  MapMode = 5
  Placement = pos=(-9.4,0,0) rot=(0.57735,-0.57735,-0.57735;2.0944rad)
  Support = -> [Binder010]
  expr: Constraints[77] = Spreadsheet.acrylic_thin
  expr: Constraints[80] = Spreadsheet.acrylic_thin
  expr: Constraints[84] = Spreadsheet.acrylic_thin * 2
  sketch-geometry (39):
    g0: Circle CenterX=0 CenterY=10.85 CenterZ=0 NormalX=0 NormalY=0 NormalZ=1 AngleXU=0 Radius=2.1
    g1: Circle CenterX=-8.9 CenterY=20.85 CenterZ=0 NormalX=0 NormalY=0 NormalZ=1 AngleXU=0 Radius=1.55
    g2: Circle CenterX=8.9 CenterY=20.85 CenterZ=0 NormalX=0 NormalY=0 NormalZ=1 AngleXU=0 Radius=1.55
    g3: Circle CenterX=-1.19e-14 CenterY=72.5 CenterZ=0 NormalX=0 NormalY=0 NormalZ=1 AngleXU=0 Radius=1.55
    g4: ArcOfCircle CenterX=-8.15 CenterY=75.1 CenterZ=0 NormalX=0 NormalY=0 NormalZ=1 AngleXU=0 Radius=3 StartAngle=1.5708 EndAngle=3.14159
    g5: ArcOfCircle CenterX=8.15 CenterY=75.1 CenterZ=0 NormalX=0 NormalY=0 NormalZ=1 AngleXU=0 Radius=3 StartAngle=1.6841e-12 EndAngle=1.5708
    g6: LineSegment StartX=11.15 StartY=75.1 StartZ=0 EndX=11.15 EndY=36.85 EndZ=0
    g7: ArcOfCircle CenterX=8.15 CenterY=9.85 CenterZ=0 NormalX=0 NormalY=0 NormalZ=1 AngleXU=0 Radius=3 StartAngle=4.71239 EndAngle=6.28319
    g8: LineSegment StartX=8.15 StartY=6.85 StartZ=0 EndX=-11.15 EndY=6.85 EndZ=0
    g9: LineSegment StartX=-11.15 StartY=39.85 StartZ=0 EndX=-11.15 EndY=75.1 EndZ=0
    g10: GeomPoint X=11.15 Y=6.85 Z=0
    g11: ArcOfCircle CenterX=-3.18082 CenterY=49.59 CenterZ=0 NormalX=0 NormalY=0 NormalZ=1 AngleXU=0 Radius=3 StartAngle=1.5708 EndAngle=3.14159
    g12: LineSegment StartX=-3.18082 StartY=52.59 StartZ=0 EndX=3.18082 EndY=52.59 EndZ=0
    g13: ArcOfCircle CenterX=3.18082 CenterY=49.59 CenterZ=0 NormalX=0 NormalY=0 NormalZ=1 AngleXU=0 Radius=3 StartAngle=-7.3053e-12 EndAngle=1.5708
    g14: ArcOfCircle CenterX=3.18082 CenterY=28.85 CenterZ=0 NormalX=0 NormalY=0 NormalZ=1 AngleXU=0 Radius=3 StartAngle=4.71239 EndAngle=6.28319
    g15: LineSegment StartX=3.18082 StartY=25.85 StartZ=0 EndX=-3.18082 EndY=25.85 EndZ=0
    g16: ArcOfCircle CenterX=-3.18082 CenterY=28.85 CenterZ=0 NormalX=0 NormalY=0 NormalZ=1 AngleXU=0 Radius=3 StartAngle=3.14159 EndAngle=4.71239
    g17: LineSegment StartX=-6.18082 StartY=28.85 StartZ=0 EndX=-6.18082 EndY=49.59 EndZ=0
    g18: LineSegment StartX=6.18082 StartY=49.59 StartZ=0 EndX=6.18082 EndY=28.85 EndZ=0
    g19: LineSegment StartX=-11.15 StartY=6.85 StartZ=0 EndX=-37.15 EndY=6.85 EndZ=0
    g20: ArcOfCircle CenterX=-37.15 CenterY=7.85 CenterZ=0 NormalX=0 NormalY=0 NormalZ=1 AngleXU=0 Radius=1 StartAngle=3.14159 EndAngle=4.71239
    g21: ArcOfCircle CenterX=-39.15 CenterY=7.85 CenterZ=0 NormalX=0 NormalY=0 NormalZ=1 AngleXU=0 Radius=1 StartAngle=0 EndAngle=3.14159
    g22: ArcOfCircle CenterX=-41.15 CenterY=7.85 CenterZ=0 NormalX=0 NormalY=0 NormalZ=1 AngleXU=0 Radius=1 StartAngle=3.14159 EndAngle=6.28319
    g23: LineSegment StartX=-42.15 StartY=7.85 StartZ=0 EndX=-42.15 EndY=35.85 EndZ=0
    g24: ArcOfCircle CenterX=-41.15 CenterY=35.85 CenterZ=0 NormalX=0 NormalY=0 NormalZ=1 AngleXU=0 Radius=1 StartAngle=-1.8e-15 EndAngle=3.14159
    g25: ArcOfCircle CenterX=-39.15 CenterY=35.85 CenterZ=0 NormalX=0 NormalY=0 NormalZ=1 AngleXU=0 Radius=1 StartAngle=3.14159 EndAngle=6.28319
    g26: ArcOfCircle CenterX=-37.15 CenterY=35.85 CenterZ=0 NormalX=0 NormalY=0 NormalZ=1 AngleXU=0 Radius=1 StartAngle=1.5708 EndAngle=3.14159
    g27: LineSegment StartX=-37.15 StartY=36.85 StartZ=0 EndX=-14.15 EndY=36.85 EndZ=0
    g28: ArcOfCircle CenterX=-14.15 CenterY=39.85 CenterZ=0 NormalX=0 NormalY=0 NormalZ=1 AngleXU=0 Radius=3 StartAngle=4.71239 EndAngle=6.28319
    g29: LineSegment StartX=-8.15 StartY=78.1 StartZ=0 EndX=8.15 EndY=78.1 EndZ=0
    g30: ArcOfCircle CenterX=12.55 CenterY=13.85 CenterZ=0 NormalX=0 NormalY=0 NormalZ=1 AngleXU=0 Radius=1.4 StartAngle=6e-16 EndAngle=3.14159
    g31: LineSegment StartX=13.95 StartY=13.85 StartZ=0 EndX=13.95 EndY=8.25 EndZ=0
    g32: ArcOfCircle CenterX=15.35 CenterY=8.25 CenterZ=0 NormalX=0 NormalY=0 NormalZ=1 AngleXU=0 Radius=1.4 StartAngle=3.14159 EndAngle=6.28319
    g33: LineSegment StartX=16.75 StartY=8.25 StartZ=0 EndX=16.75 EndY=39.65 EndZ=0
    g34: ArcOfCircle CenterX=15.35 CenterY=39.65 CenterZ=0 NormalX=0 NormalY=0 NormalZ=1 AngleXU=0 Radius=1.4 StartAngle=-9e-16 EndAngle=3.14159
    g35: LineSegment StartX=13.95 StartY=39.65 StartZ=0 EndX=13.95 EndY=36.85 EndZ=0
    g36: LineSegment StartX=13.95 StartY=36.85 StartZ=0 EndX=11.15 EndY=36.85 EndZ=0
    g37: LineSegment StartX=8.15 StartY=6.85 StartZ=0 EndX=15.35 EndY=6.85 EndZ=0
    g38: LineSegment StartX=11.15 StartY=13.85 StartZ=0 EndX=11.15 EndY=9.85 EndZ=0
  constraints (98):
    c: Equal(g1,g2)
    c: Diameter(g1) = 3.1
    c: Diameter(g3) = 3.1
    c: Tangent(g5,g6) = 1.5708
    c: Tangent(g7,g8) = 1.5708
    c: Tangent(g9,g4) = 1.5708
    c: Horizontal(g8)
    c: Vertical(g6)
    c: Vertical(g9)
    c: Equal(g4,g5)
    c: Equal(g5,g7)
    c: PointOnObject(g10,g6)
    c: PointOnObject(g10,g8)
    c: Distance(g0,g8) = 4
    c: Tangent(g11,g12) = 1.5708
    c: Tangent(g12,g13) = 1.5708
    c: Tangent(g14,g15) = 1.5708
    c: Tangent(g15,g16) = 1.5708
    c: Tangent(g17,g11) = 1.5708
    c: Horizontal(g12)
    c: Horizontal(g15)
    c: Vertical(g17)
    c: Radius(g11) = 3
    c: Coincident(g0,g-5)
    c: Coincident(g1,g-3)
    c: Coincident(g2,g-4)
    c: PointOnObject(g38,g-7)
    c: Tangent(g16,g17) = 1.5708
    c: Vertical(g18)
    c: Tangent(g18,g14) = 1.5708
    c: Tangent(g18,g13) = 1.5708
    c: Equal(g11,g13)
    c: Equal(g13,g14)
    c: Equal(g14,g16)
    c: PointOnObject(g16,g-10)
    c: PointOnObject(g14,g-11)
    c: Horizontal(g15,g-10)
    c: PointOnObject(g19,g-6)
    c: Horizontal(g19)
    c: Tangent(g19,g20) = 1.5708
    c: Tangent(g20,g21) = 1.5708
    c: Tangent(g21,g22) = 1.5708
    c: Vertical(g23)
    c: Tangent(g23,g24) = 1.5708
    c: Tangent(g24,g25) = 1.5708
    c: Tangent(g25,g26) = 1.5708
    c: Horizontal(g27)
    c: Coincident(g8,g19)
    c: Tangent(g9,g28) = -1.5708
    c: Tangent(g27,g28) = -1.5708
    c: Tangent(g26,g27) = 1.5708
    c: Tangent(g22,g23) = 1.5708
    c: Equal(g20,g21)
    c: Equal(g20,g22)
    c: Equal(g20,g24)
    c: Equal(g20,g25)
    c: Equal(g20,g26)
    c: Radius(g20) = 1
    c: Angle(g20) = 1.5708
    c: Angle(g21) = 3.14159
    c: Angle(g26) = 1.5708
    c: Angle(g25) = 3.14159
    c: Radius(g4) = 3
    c: Equal(g28,g4)
    c: DistanceY(g8,g27) = 30
    c: DistanceX(g19,g19) = 26
    c: Vertical(g9,g8)
    c: Horizontal(g29)
    c: Tangent(g29,g4) = 1.5708
    c: Tangent(g29,g5) = 1.5708
    c: Vertical(g31)
    c: Tangent(g31,g32) = -1.5708
    c: Vertical(g33)
    c: Vertical(g35)
    c: Coincident(g35,g36)
    c: Horizontal(g36)
    c: Equal(g36,g35)
    c: DistanceX(g36,g36) = 2.8
    c: Tangent(g33,g34) = -1.5708
    c: Tangent(g34,g35) = -1.5708
    c: Diameter(g34) = 2.8
    c: Equal(g32,g34)
    c: Tangent(g32,g33) = -1.5708
    c: Tangent(g30,g31) = 1.5708
    c: DistanceY(g32,g30) = 5.6
    c: Tangent(g30,g6) = -1.5708
    c: Coincident(g37,g7)
    c: Horizontal(g37)
    c: Horizontal(g36,g27)
    c: Tangent(g37,g32) = -1.5708
    c: Coincident(g6,g36)
    c: Vertical(g38)
    c: Coincident(g38,g30)
    c: Tangent(g38,g7) = 1.5708
    c: Diameter(g0) = 4.2
    c: Symmetric(g-12,g-13,g3)
    c: Tangent(g29,g-12)
    c: PointOnObject(g11,g-14)
FEATURE [PartDesign::Pad] Pad007
  Direction = (-1,0,0)
  Length = 2.8
  Length2 = 10
  Profile = -> Sketch007
  ReferenceAxis = -> Sketch007 [N_Axis]
  Type = 0
  expr: Length = Spreadsheet.acrylic_thin
FEATURE [PartDesign::Body] Body017  label="body_right"
  Group = -> [Sketch007,Binder010,Binder011,Binder012,Pad007]
  Origin = -> Origin019
  Tip = -> Pad007
FEATURE [Part::Feature] Part__Feature  label="batt_9V005_cp_sp"
  shape: bbox 13.59 x 26.29 x 1.575 mm, 21 faces (baked)
FEATURE [Part::Feature] Part__Feature003  label="batt_9V005_cp_sp003"
  shape: bbox 7.925 x 7.925 x 3.557 mm, 27 faces (baked)
FEATURE [Part::Feature] Part__Feature004  label="batt_9V005_cp_sp004"
  shape: bbox 9.35 x 9.35 x 4.186 mm, 125 faces (baked)
FEATURE [Part::Feature] Part__Feature005  label="batt_9V005_cp_sp005"
  shape: bbox 15.74 x 25.33 x 0.8457 mm, 1 faces, 0 solids (baked)
FEATURE [Part::Feature] Part__Feature006  label="batt_9V005_cp_sp006"
  shape: bbox 15.38 x 24.78 x 2e-07 mm, 1 faces, 0 solids (baked)
FEATURE [Part::Feature] Part__Feature007  label="batt_9V005_cp_sp007"
  shape: bbox 16.6 x 26 x 42.82 mm, 188 faces, 0 solids (baked)
FEATURE [Part::Feature] Part__Feature008  label="batt_9V005_cp_sp008"
  shape: bbox 7.6 x 8.776 x 3 mm, 28 faces, 0 solids (baked)
FEATURE [Part::Feature] Part__Feature009  label="batt_9V005_cp_sp009"
  shape: bbox 6.35 x 6.35 x 1.5 mm, 2 faces, 0 solids (baked)
FEATURE [Part::Feature] Part__Feature010  label="batt_9V005_cp_sp010"
  shape: bbox 8 x 8 x 3.2 mm, 10 faces, 0 solids (baked)
FEATURE [App::Part] batt_9V005_cp_sp  label="batt_9V005_cp_sp011"
  Group = -> [Part__Feature,Part__Feature003,Part__Feature004,Part__Feature005,Part__Feature006,Part__Feature007,Part__Feature008,Part__Feature009,Part__Feature010]
  Origin = -> Origin020
  Placement = pos=(0,25,40) rot=(0,0,1;0rad)
FEATURE [PartDesign::FeatureBase] Clone008
  BaseFeature = -> Body017
FEATURE [PartDesign::Body] Body018  label="body_left"
  Group = -> [Clone008]
  Origin = -> Origin021
  Placement = pos=(21.6,0,0) rot=(0,0,1;0rad)
  Tip = -> Clone008
FEATURE [PartDesign::SubShapeBinder] Binder013
  BindCopyOnChange = 0
  BindMode = 0
  ClaimChildren = false
  Context = -> Body019 [Binder013.]
  Fuse = false
  MakeFace = true
  OffsetFill = false
  OffsetIntersection = false
  OffsetJoinType = 0
  OffsetOpenResult = false
  PartialLoad = false
  Relative = true
  Support = -> [Body017]
  _Version = 2
FEATURE [PartDesign::SubShapeBinder] Binder014
  BindCopyOnChange = 0
  BindMode = 0
  ClaimChildren = false
  Context = -> Body019 [Binder014.]
  Fuse = false
  MakeFace = true
  OffsetFill = false
  OffsetIntersection = false
  OffsetJoinType = 0
  OffsetOpenResult = false
  PartialLoad = false
  Relative = true
  Support = -> [Body018]
  _Version = 2
FEATURE [Sketcher::SketchObject] Sketch008
  ExternalGeometry = -> [Binder014]
  FullyConstrained = true
  MapMode = 5
  Placement = pos=(0,0,0) rot=(0.57735,0.57735,0.57735;2.0944rad)
  Support = -> [YZ_Plane020]
  sketch-geometry (2):
    g0: Circle CenterX=5e-16 CenterY=72.5 CenterZ=0 NormalX=0 NormalY=0 NormalZ=1 AngleXU=0 Radius=1.55
    g1: Circle CenterX=5e-16 CenterY=72.5 CenterZ=0 NormalX=0 NormalY=0 NormalZ=1 AngleXU=0 Radius=4
  constraints (4):
    c: Coincident(g0,g-3)
    c: Coincident(g1,g0)
    c: Equal(g0,g-3)
    c: Diameter(g1) = 8
FEATURE [PartDesign::Pad] Pad008
  Direction = (1,-2e-16,3e-16)
  Length = 18.8
  Length2 = 10
  Midplane = true
  Placement = pos=(0,0,0) rot=(0.57735,0.57735,0.57735;2.0944rad)
  Profile = -> Sketch008
  ReferenceAxis = -> Sketch008 [N_Axis]
  Type = 0
FEATURE [PartDesign::Body] Body019  label="spacer_top_centre"
  Group = -> [Sketch008,Binder013,Binder014,Pad008]
  Origin = -> Origin022
  Tip = -> Pad008
FEATURE [PartDesign::SubShapeBinder] Binder015
  BindCopyOnChange = 0
  BindMode = 0
  ClaimChildren = false
  Context = -> Body020 [Binder015.]
  Fuse = false
  MakeFace = true
  OffsetFill = false
  OffsetIntersection = false
  OffsetJoinType = 0
  OffsetOpenResult = false
  PartialLoad = false
  Relative = true
  Support = -> [Body017]
  _Version = 2
FEATURE [PartDesign::SubShapeBinder] Binder016
  BindCopyOnChange = 0
  BindMode = 0
  ClaimChildren = false
  Context = -> Body020 [Binder016.]
  Fuse = false
  MakeFace = true
  OffsetFill = false
  OffsetIntersection = false
  OffsetJoinType = 0
  OffsetOpenResult = false
  PartialLoad = false
  Relative = true
  Support = -> [Body002]
  _Version = 2
FEATURE [Sketcher::SketchObject] Sketch009
  ExternalGeometry = -> [Binder015]
  FullyConstrained = true
  MapMode = 5
  Placement = pos=(-12.2,0,0) rot=(0.57735,-0.57735,-0.57735;2.0944rad)
  Support = -> [Binder015]
  sketch-geometry (2):
    g0: Circle CenterX=-5.8e-15 CenterY=72.5 CenterZ=0 NormalX=0 NormalY=0 NormalZ=1 AngleXU=0 Radius=1.55
    g1: Circle CenterX=-5.8e-15 CenterY=72.5 CenterZ=0 NormalX=0 NormalY=0 NormalZ=1 AngleXU=0 Radius=4
  constraints (4):
    c: Coincident(g1,g0)
    c: Diameter(g1) = 8
    c: Equal(g0,g-3)
    c: Coincident(g0,g-3)
FEATURE [PartDesign::Pad] Pad009
  Direction = (-1,0,0)
  Length = 10
  Length2 = 10
  Profile = -> Sketch009
  ReferenceAxis = -> Sketch009 [N_Axis]
  Type = 3
  UpToFace = -> Binder016 [Face1]
FEATURE [Sketcher::SketchObject] Sketch010
  ExternalGeometry = -> [Pad009,Binder016]
  FullyConstrained = true
  MapMode = 5
  Placement = pos=(-24.3,-1.09e-14,-2.58e-14) rot=(0.57735,-0.57735,-0.57735;2.0944rad)
  Support = -> [Pad009]
  sketch-geometry (2):
    g0: Circle CenterX=-2.06e-14 CenterY=72.5 CenterZ=0 NormalX=0 NormalY=0 NormalZ=1 AngleXU=0 Radius=3
    g1: Circle CenterX=-2.06e-14 CenterY=72.5 CenterZ=0 NormalX=0 NormalY=0 NormalZ=1 AngleXU=0 Radius=1.55
  constraints (4):
    c: Equal(g1,g-6)
    c: Coincident(g0,g-6)
    c: Coincident(g0,g1)
    c: Diameter(g0) = 6
FEATURE [PartDesign::Pad] Pad010
  BaseFeature = -> Pad009
  Direction = (-1,-3e-16,-1e-15)
  Length = 6
  Length2 = 10
  Profile = -> Sketch010
  ReferenceAxis = -> Sketch010 [N_Axis]
  Type = 0
  expr: Length = Spreadsheet.acrylic_thin * 2 + 0.4
FEATURE [PartDesign::Body] Body020  label="spacer_top_right"
  Group = -> [Binder015,Binder016,Sketch009,Pad009,Sketch010,Pad010]
  Origin = -> Origin023
  Tip = -> Pad010
FEATURE [PartDesign::FeatureBase] Clone009
  BaseFeature = -> Body020
FEATURE [PartDesign::Body] Body021  label="spacer_top_left"
  Group = -> [Clone009]
  Origin = -> Origin024
  Placement = pos=(0,0,0) rot=(0,0,1;3.14159rad)
  Tip = -> Clone009
FEATURE [Part::FeaturePython] ThreadedRod  label="M3x70-ThreadedRod"  # Fasteners workbench fastener (typed FeaturePython)
  Placement = pos=(-35,0,72.5) rot=(0,-1,0;1.5708rad)
  diameter = 4
  diameterCustom = 6
  invert = false
  leftHanded = false
  length = 70
  matchOuter = false
  offset = 0
  pitchCustom = 1
  thread = false
  type = 4
FEATURE [PartDesign::SubShapeBinder] Binder017
  BindCopyOnChange = 0
  BindMode = 0
  ClaimChildren = false
  Context = -> Body022 [Binder017.]
  Fuse = false
  MakeFace = true
  OffsetFill = false
  OffsetIntersection = false
  OffsetJoinType = 0
  OffsetOpenResult = false
  PartialLoad = false
  Relative = true
  Support = -> [Body017]
  _Version = 2
FEATURE [PartDesign::SubShapeBinder] Binder018
  BindCopyOnChange = 0
  BindMode = 0
  ClaimChildren = false
  Context = -> Body022 [Binder018.]
  Fuse = false
  MakeFace = true
  OffsetFill = false
  OffsetIntersection = false
  OffsetJoinType = 0
  OffsetOpenResult = false
  PartialLoad = false
  Relative = true
  Support = -> [Body018]
  _Version = 2
FEATURE [PartDesign::SubShapeBinder] Binder019
  BindCopyOnChange = 0
  BindMode = 0
  ClaimChildren = false
  Context = -> Body022 [Binder019.]
  Fuse = false
  MakeFace = true
  OffsetFill = false
  OffsetIntersection = false
  OffsetJoinType = 0
  OffsetOpenResult = false
  PartialLoad = false
  Relative = true
  Support = -> [Part001]
  _Version = 2
FEATURE [Sketcher::SketchObject] Sketch011
  ExternalGeometry = -> [Binder017,Binder018]
  FullyConstrained = true
  MapMode = 5
  Placement = pos=(0,-11.15,0) rot=(1,0,0;1.5708rad)
  Support = -> [Binder019]
  expr: Constraints[23] = Spreadsheet.acrylic_thin - 0.3
  expr: Constraints[24] = Spreadsheet.acrylic_thin + 0.3
  sketch-geometry (36):
    g0: LineSegment StartX=-9.4 StartY=36.85 StartZ=0 EndX=-12.2 EndY=36.85 EndZ=0
    g1: LineSegment StartX=-12.2 StartY=36.85 StartZ=0 EndX=-12.2 EndY=76.6 EndZ=0
    g2: ArcOfCircle CenterX=-10.7 CenterY=76.6 CenterZ=0 NormalX=0 NormalY=0 NormalZ=1 AngleXU=0 Radius=1.5 StartAngle=1.5708 EndAngle=3.14159
    g3: LineSegment StartX=-5 StartY=79.6 StartZ=0 EndX=-5 EndY=81.6 EndZ=0
    g4: LineSegment StartX=-9.4 StartY=36.85 StartZ=0 EndX=-9.4 EndY=11.35 EndZ=0
    g5: LineSegment StartX=-9.4 StartY=11.35 StartZ=0 EndX=-12.2 EndY=11.35 EndZ=0
    g6: LineSegment StartX=-12.2 StartY=11.35 StartZ=0 EndX=-12.2 EndY=8.25 EndZ=0
    g7: LineSegment StartX=-12.2 StartY=8.25 StartZ=0 EndX=0 EndY=8.25 EndZ=0
    g8: LineSegment StartX=-10.7 StartY=78.1 StartZ=0 EndX=-6.5 EndY=78.1 EndZ=0
    g9: ArcOfCircle CenterX=-6.5 CenterY=79.6 CenterZ=0 NormalX=0 NormalY=0 NormalZ=1 AngleXU=0 Radius=1.5 StartAngle=4.71239 EndAngle=6.28319
    g10: LineSegment StartX=12.2 StartY=11.35 StartZ=0 EndX=9.4 EndY=11.35 EndZ=0
    g11: LineSegment StartX=9.4 StartY=11.35 StartZ=0 EndX=9.4 EndY=36.85 EndZ=0
    g12: LineSegment StartX=9.4 StartY=36.85 StartZ=0 EndX=12.2 EndY=36.85 EndZ=0
    g13: LineSegment StartX=12.2 StartY=36.85 StartZ=0 EndX=12.2 EndY=76.6 EndZ=0
    g14: ArcOfCircle CenterX=10.7 CenterY=76.6 CenterZ=0 NormalX=0 NormalY=0 NormalZ=1 AngleXU=0 Radius=1.5 StartAngle=4e-15 EndAngle=1.5708
    g15: LineSegment StartX=10.7 StartY=78.1 StartZ=0 EndX=6.5 EndY=78.1 EndZ=0
    g16: ArcOfCircle CenterX=6.5 CenterY=79.6 CenterZ=0 NormalX=0 NormalY=0 NormalZ=1 AngleXU=0 Radius=1.5 StartAngle=3.14159 EndAngle=4.71239
    g17: LineSegment StartX=5 StartY=79.6 StartZ=0 EndX=5 EndY=81.6 EndZ=0
    g18: LineSegment StartX=12.2 StartY=11.35 StartZ=0 EndX=12.2 EndY=8.25 EndZ=0
    g19: LineSegment StartX=12.2 StartY=8.25 StartZ=0 EndX=0 EndY=8.25 EndZ=0
    g20: LineSegment StartX=-19 StartY=104.35 StartZ=0 EndX=19 EndY=104.35 EndZ=0
    g21: LineSegment StartX=19 StartY=104.35 StartZ=0 EndX=19 EndY=96.3913 EndZ=0
    g22: LineSegment StartX=19 StartY=83.1 StartZ=0 EndX=6.5 EndY=83.1 EndZ=0
    g23: LineSegment StartX=-19 StartY=83.1 StartZ=0 EndX=-19 EndY=86.8087 EndZ=0
    g24: LineSegment StartX=-6.5 StartY=83.1 StartZ=0 EndX=-19 EndY=83.1 EndZ=0
    g25: ArcOfCircle CenterX=-6.5 CenterY=81.6 CenterZ=0 NormalX=0 NormalY=0 NormalZ=1 AngleXU=0 Radius=1.5 StartAngle=-3.6e-15 EndAngle=1.5708
    g26: GeomPoint X=-5 Y=83.1 Z=0
    g27: ArcOfCircle CenterX=6.5 CenterY=81.6 CenterZ=0 NormalX=0 NormalY=0 NormalZ=1 AngleXU=0 Radius=1.5 StartAngle=1.5708 EndAngle=3.14159
    g28: ArcOfCircle CenterX=-18 CenterY=94.1 CenterZ=0 NormalX=0 NormalY=0 NormalZ=1 AngleXU=0 Radius=2.5 StartAngle=1.98231 EndAngle=3.14159
    g29: ArcOfCircle CenterX=-18 CenterY=89.1 CenterZ=0 NormalX=0 NormalY=0 NormalZ=1 AngleXU=0 Radius=2.5 StartAngle=3.14159 EndAngle=4.30087
    g30: LineSegment StartX=-20.5 StartY=94.1 StartZ=0 EndX=-20.5 EndY=89.1 EndZ=0
    g31: ArcOfCircle CenterX=18 CenterY=94.1 CenterZ=0 NormalX=0 NormalY=0 NormalZ=1 AngleXU=0 Radius=2.5 StartAngle=6e-16 EndAngle=1.15928
    g32: ArcOfCircle CenterX=18 CenterY=89.1 CenterZ=0 NormalX=0 NormalY=0 NormalZ=1 AngleXU=0 Radius=2.5 StartAngle=5.12391 EndAngle=6.28319
    g33: LineSegment StartX=20.5 StartY=89.1 StartZ=0 EndX=20.5 EndY=94.1 EndZ=0
    g34: LineSegment StartX=-19 StartY=96.3913 StartZ=0 EndX=-19 EndY=104.35 EndZ=0
    g35: LineSegment StartX=19 StartY=86.8087 StartZ=0 EndX=19 EndY=83.1 EndZ=0
  constraints (94):
    c: Coincident(g-3,g0)
    c: Coincident(g0,g-3)
    c: Coincident(g0,g1)
    c: Vertical(g1)
    c: Tangent(g1,g2) = 1.5708
    c: Vertical(g3)
    c: Coincident(g0,g4)
    c: Vertical(g4)
    c: Coincident(g4,g5)
    c: Horizontal(g5)
    c: Coincident(g5,g6)
    c: Vertical(g6)
    c: Coincident(g6,g7)
    c: Horizontal(g7)
    c: Radius(g2) = 1.5
    c: Angle(g2) = 1.5708
    c: DistanceX(g-2,g3) = -5
    c: DistanceY(g3,g26) = 3.5
    c: Tangent(g2,g8) = 1.5708
    c: Tangent(g8,g9) = -1.5708
    c: Tangent(g9,g3) = -1.5708
    c: Equal(g9,g2)
    c: Equal(g0,g5)
    c: DistanceY(g5,g-5) = 2.5
    c: DistanceY(g6,g6) = 3.1
    c: PointOnObject(g7,g-2)
    c: Horizontal(g10)
    c: Coincident(g10,g11)
    c: Coincident(g11,g-4)
    c: Vertical(g11)
    c: Coincident(g11,g12)
    c: Coincident(g12,g-4)
    c: Coincident(g12,g13)
    c: Vertical(g13)
    c: Tangent(g13,g14) = -1.5708
    c: Horizontal(g15)
    c: Tangent(g15,g16) = 1.5708
    c: Vertical(g17)
    c: Tangent(g14,g15) = -1.5708
    c: Equal(g14,g16)
    c: Equal(g16,g2)
    c: Tangent(g16,g17) = 1.5708
    c: Equal(g13,g1)
    c: Equal(g15,g8)
    c: Equal(g11,g4)
    c: Equal(g10,g5)
    c: Coincident(g10,g18)
    c: Vertical(g18)
    c: Coincident(g18,g19)
    c: Coincident(g19,g7)
    c: Horizontal(g19)
    c: PointOnObject(g-9,g8)
    c: Coincident(g20,g21)
    c: Coincident(g35,g22)
    c: Coincident(g24,g23)
    c: Coincident(g34,g20)
    c: Horizontal(g20)
    c: Vertical(g21)
    c: Vertical(g23)
    c: DistanceY(g23,g34) = 21.25
    c: DistanceX(g24,g22) = 38
    c: Symmetric(g24,g35,g-2)
    c: Horizontal(g24)
    c: Horizontal(g22)
    c: PointOnObject(g26,g24)
    c: PointOnObject(g26,g3)
    c: Tangent(g24,g25) = -1.5708
    c: Tangent(g3,g25) = -1.5708
    c: Tangent(g22,g27) = -1.5708
    c: Tangent(g17,g27) = 1.5708
    c: Equal(g25,g27)
    c: Equal(g27,g9)
    c: Tangent(g28,g30) = -1.5708
    c: Tangent(g30,g29) = -1.5708
    c: Equal(g28,g29)
    c: Vertical(g30)
    c: Tangent(g32,g33) = -1.5708
    c: Tangent(g33,g31) = -1.5708
    c: Equal(g31,g32)
    c: Symmetric(g28,g31,g-2)
    c: Symmetric(g29,g32,g-2)
    c: DistanceY(g29,g28) = 5
    c: Equal(g28,g31)
    c: DistanceX(g23,g29) = 1
    c: Radius(g28) = 2.5
    c: DistanceY(g23,g29) = 6
    c: Coincident(g23,g29)
    c: Coincident(g34,g28)
    c: Coincident(g21,g31)
    c: Coincident(g35,g32)
    c: Vertical(g34)
    c: Vertical(g23,g28)
    c: Vertical(g21,g32)
    c: Vertical(g35)
FEATURE [PartDesign::Pad] Pad011
  Direction = (0,-1,2e-16)
  Length = 2.8
  Length2 = 10
  Profile = -> Sketch011
  ReferenceAxis = -> Sketch011 [N_Axis]
  Type = 0
  expr: Length = Spreadsheet.acrylic_thin
FEATURE [PartDesign::SubShapeBinder] Binder020
  BindCopyOnChange = 0
  BindMode = 0
  ClaimChildren = false
  Context = -> Body023 [Binder020.]
  Fuse = false
  MakeFace = true
  OffsetFill = false
  OffsetIntersection = false
  OffsetJoinType = 0
  OffsetOpenResult = false
  PartialLoad = false
  Relative = true
  Support = -> [Body020]
  _Version = 2
FEATURE [PartDesign::SubShapeBinder] Binder021
  BindCopyOnChange = 0
  BindMode = 0
  ClaimChildren = false
  Context = -> Body023 [Binder021.]
  Fuse = false
  MakeFace = true
  OffsetFill = false
  OffsetIntersection = false
  OffsetJoinType = 0
  OffsetOpenResult = false
  PartialLoad = false
  Relative = true
  Support = -> [Body002]
  _Version = 2
FEATURE [PartDesign::Plane] DatumPlane004
  AttachmentOffset = pos=(0,0,0.1) rot=(0,0,1;0rad)
  Length = 148.256
  MapMode = 5
  Placement = pos=(-27.2,9e-15,1.36e-14) rot=(0.57735,-0.57735,-0.57735;2.0944rad)
  ResizeMode = 0
  Support = -> [Binder021]
  Width = 130.375
FEATURE [Sketcher::SketchObject] Sketch012
  ExternalGeometry = -> [Binder020,Binder021]
  FullyConstrained = true
  MapMode = 5
  Placement = pos=(-27.2,9e-15,1.36e-14) rot=(-0.57735,0.57735,0.57735;4.18879rad)
  Support = -> [DatumPlane004]
  sketch-geometry (34):
    g0: LineSegment StartX=-44.0703 StartY=62.2032 StartZ=0 EndX=-2.75559 EndY=81.4686 EndZ=0
    g1: LineSegment StartX=7.87582 StartY=77.5991 StartZ=0 EndX=23.7603 EndY=43.5348 EndZ=0
    g2: LineSegment StartX=27.747 StartY=42.0837 StartZ=0 EndX=61.2804 EndY=57.7206 EndZ=0
    g3: LineSegment StartX=61.2804 StartY=57.7206 StartZ=0 EndX=65.5066 EndY=48.6575 EndZ=0
    g4: LineSegment StartX=65.5066 StartY=48.6575 StartZ=0 EndX=31.9732 EndY=33.0207 EndZ=0
    g5: LineSegment StartX=14.6972 StartY=39.3086 StartZ=0 EndX=2.64634 EndY=65.1517 EndZ=0
    g6: LineSegment StartX=-6.75058 StartY=68.5719 StartZ=0 EndX=-39.8442 EndY=53.1402 EndZ=0
    g7: ArcOfCircle CenterX=-41.9572 CenterY=57.6717 CenterZ=0 NormalX=0 NormalY=0 NormalZ=1 AngleXU=0 Radius=5 StartAngle=2.00713 EndAngle=5.14872
    g8: ArcOfCircle CenterX=26.4792 CenterY=44.8027 CenterZ=0 NormalX=0 NormalY=0 NormalZ=1 AngleXU=0 Radius=3 StartAngle=3.57792 EndAngle=5.14872
    g9: LineSegment StartX=-44.0703 StartY=62.2032 StartZ=0 EndX=-39.8442 EndY=53.1402 EndZ=0
    g10: LineSegment StartX=-6.75058 StartY=68.5719 StartZ=0 EndX=2.64634 EndY=65.1517 EndZ=0
    g11: ArcOfCircle CenterX=26.4792 CenterY=44.8027 CenterZ=0 NormalX=0 NormalY=0 NormalZ=1 AngleXU=0 Radius=13 StartAngle=3.57792 EndAngle=5.14872
    g12: LineSegment StartX=-41.9572 StartY=57.6717 StartZ=0 EndX=-5.70494 EndY=74.5764 EndZ=0
    g13: LineSegment StartX=5.70494 StartY=70.4236 StartZ=0 EndX=22.6097 EndY=34.1713 EndZ=0
    g14: LineSegment StartX=22.6097 StartY=34.1713 StartZ=0 EndX=63.3935 EndY=53.1891 EndZ=0
    g15: LineSegment StartX=-5.70494 StartY=74.5764 StartZ=0 EndX=5.70494 EndY=70.4236 EndZ=0
    g16: LineSegment StartX=-1.92e-14 StartY=72.5 StartZ=0 EndX=-2.05212 EndY=66.8618 EndZ=0
    g17: Circle CenterX=-1.92e-14 CenterY=72.5 CenterZ=0 NormalX=0 NormalY=0 NormalZ=1 AngleXU=0 Radius=3
    g18: ArcOfCircle CenterX=0.625359 CenterY=74.2182 CenterZ=0 NormalX=0 NormalY=0 NormalZ=1 AngleXU=0 Radius=8 StartAngle=0.436332 EndAngle=2.00713
    g19: LineSegment StartX=71.0274 StartY=51.0155 StartZ=0 EndX=76.4652 EndY=53.5512 EndZ=0
    g20: LineSegment StartX=76.4652 StartY=53.5512 StartZ=0 EndX=76.9881 EndY=59.5284 EndZ=0
    g21: LineSegment StartX=76.9881 StartY=59.5284 StartZ=0 EndX=72.0732 EndY=62.9698 EndZ=0
    g22: LineSegment StartX=72.0732 StartY=62.9698 StartZ=0 EndX=66.6354 EndY=60.4341 EndZ=0
    g23: LineSegment StartX=66.6354 StartY=60.4341 StartZ=0 EndX=66.1124 EndY=54.4569 EndZ=0
    g24: LineSegment StartX=66.1124 StartY=54.4569 StartZ=0 EndX=71.0274 EndY=51.0155 EndZ=0
    g25: Circle CenterX=71.5503 CenterY=56.9926 CenterZ=0 NormalX=0 NormalY=0 NormalZ=1 AngleXU=0 Radius=6
    g26: LineSegment StartX=63.3935 StartY=53.1891 StartZ=0 EndX=66.1124 EndY=54.4569 EndZ=0
    g27: LineSegment StartX=72.0732 StartY=62.9698 StartZ=0 EndX=70.3828 EndY=66.595 EndZ=0
    g28: LineSegment StartX=70.3828 StartY=66.595 StartZ=0 EndX=61.7027 EndY=62.5475 EndZ=0
    g29: LineSegment StartX=61.7027 StartY=62.5475 StartZ=0 EndX=61.2804 EndY=57.7206 EndZ=0
    g30: LineSegment StartX=65.5066 StartY=48.6575 StartZ=0 EndX=69.4756 EndY=45.8784 EndZ=0
    g31: LineSegment StartX=69.4756 StartY=45.8784 StartZ=0 EndX=78.1557 EndY=49.926 EndZ=0
    g32: LineSegment StartX=78.1557 StartY=49.926 StartZ=0 EndX=76.4652 EndY=53.5512 EndZ=0
    g33: Circle CenterX=-41.9572 CenterY=57.6717 CenterZ=0 NormalX=0 NormalY=0 NormalZ=1 AngleXU=0 Radius=0.6
  constraints (84):
    c: Coincident(g2,g3)
    c: Coincident(g3,g4)
    c: Tangent(g6,g7) = 1.5708
    c: Tangent(g1,g8) = -1.5708
    c: Tangent(g2,g8) = -1.5708
    c: Perpendicular(g2,g3)
    c: Perpendicular(g4,g3)
    c: Perpendicular(g5,g4)
    c: Perpendicular(g2,g1)
    c: Tangent(g7,g0) = 1.5708
    c: Perpendicular(g5,g6)
    c: Angle(g7) = 3.14159
    c: Coincident(g9,g0)
    c: Coincident(g9,g6)
    c: Distance(g9) = 10
    c: Coincident(g10,g6)
    c: Coincident(g10,g5)
    c: Tangent(g11,g5) = 1.5708
    c: Tangent(g11,g4) = 1.5708
    c: Coincident(g11,g8)
    c: Symmetric(g2,g3,g14)
    c: Perpendicular(g14,g3)
    c: Coincident(g14,g13)
    c: Distance(g14) = 45
    c: Perpendicular(g13,g14)
    c: Perpendicular(g12,g13)
    c: Coincident(g12,g7)
    c: Angle(g10,g5) = 2.35619
    c: Coincident(g12,g15)
    c: Coincident(g13,g15)
    c: Perpendicular(g16,g10)
    c: Perpendicular(g16,g15)
    c: Symmetric(g6,g5,g16)
    c: Symmetric(g12,g13,g16)
    c: Coincident(g16,g-3)
    c: Equal(g12,g13)
    c: Distance(g12) = 40
    c: Coincident(g17,g16)
    c: Equal(g17,g-3)
    c: Tangent(g18,g1) = 1.5708
    c: Tangent(g18,g0) = 1.5708
    c: Equal(g3,g9)
    c: Coincident(g19,g20)
    c: Coincident(g20,g21)
    c: Coincident(g21,g22)
    c: Coincident(g22,g23)
    c: Coincident(g23,g24)
    c: Coincident(g24,g19)
    c: Equal(g19, g20-g24) x5
    c: PointOnObject(g19,g25)
    c: PointOnObject(g20,g25)
    c: PointOnObject(g21,g25)
    c: PointOnObject(g22,g25)
    c: PointOnObject(g23,g25)
    c: PointOnObject(g24,g25)
    c: Parallel(g22,g14)
    c: Coincident(g26,g14)
    c: Coincident(g26,g23)
    c: Perpendicular(g3,g26)
    c: Distance(g23) = 6
    c: Distance(g26) = 3
    c: Coincident(g22,g27)
    c: Coincident(g27,g28)
    c: Coincident(g28,g29)
    c: Coincident(g29,g2)
    c: Coincident(g4,g30)
    c: Coincident(g30,g31)
    c: Coincident(g31,g32)
    c: Coincident(g32,g19)
    c: Equal(g27,g32)
    c: Perpendicular(g22,g27)
    c: Perpendicular(g32,g19)
    c: Distance(g27) = 4
    c: Perpendicular(g28,g27)
    c: Perpendicular(g31,g32)
    c: Parallel(g24,g30)
    c: Parallel(g29,g23)
    c: Distance(g10) = 10
    c: Distance(g16) = 6
    c: Radius(g18) = 8
    c: Radius(g8) = 3
    c: Coincident(g33,g7)
    c: Diameter(g33) = 1.2
    c: Angle(g16) = -1.91986
FEATURE [PartDesign::Pad] Pad012
  Direction = (-1,-2e-16,-8e-16)
  Length = 2.8
  Length2 = 10
  Placement = pos=(-27.2,-1.2e-14,-2.9e-14) rot=(0.57735,-0.57735,-0.57735;2.0944rad)
  Profile = -> Sketch012
  ReferenceAxis = -> Sketch012 [N_Axis]
  Type = 0
  expr: Length = Spreadsheet.acrylic_thin
FEATURE [PartDesign::Body] Body023  label="arm_right"
  Group = -> [Binder020,Binder021,DatumPlane004,Sketch012,Pad012]
  Origin = -> Origin026
  Tip = -> Pad012
FEATURE [PartDesign::FeatureBase] Clone010
  BaseFeature = -> Body023
FEATURE [PartDesign::Body] Body024  label="arm_left"
  Group = -> [Clone010]
  Origin = -> Origin027
  Placement = pos=(57.2,30.65,6.9) rot=(1,0,0;0.436332rad)
  Tip = -> Clone010
FEATURE [Part::FeaturePython] Washer  label="M3-Washer"  # Fasteners workbench fastener (typed FeaturePython)
  Placement = pos=(-30.3,1.6e-14,72.5) rot=(0,-1,0;1.5708rad)
  baseObject = -> Body020 [Edge11]
  diameter = 1
  invert = false
  matchOuter = false
  offset = 0
  type = 11
FEATURE [Part::FeaturePython] Nut001  label="M3-Nut063"  # Fasteners workbench fastener (typed FeaturePython)
  Placement = pos=(-31.1,1.6e-14,72.5) rot=(0,-1,0;1.5708rad)
  baseObject = -> Washer [Edge1]
  diameter = 4
  invert = false
  leftHanded = false
  matchOuter = false
  offset = 0
  thread = false
  type = 25
FEATURE [Part::FeaturePython] Washer001  label="M3-Washer001"  # Fasteners workbench fastener (typed FeaturePython)
  Placement = pos=(30.3,-1.6e-14,72.5) rot=(0,1,0;1.5708rad)
  baseObject = -> Body021 [Edge11]
  diameter = 1
  invert = false
  matchOuter = false
  offset = 0
  type = 11
FEATURE [Part::FeaturePython] Nut002  label="M3-Nut064"  # Fasteners workbench fastener (typed FeaturePython)
  Placement = pos=(31.1,-1.6e-14,72.5) rot=(0,1,0;1.5708rad)
  baseObject = -> Washer001 [Edge1]
  diameter = 4
  invert = false
  leftHanded = false
  matchOuter = false
  offset = 0
  thread = false
  type = 25
FEATURE [Part::FeaturePython] Screw001  label="M2x10-Screw"  # Fasteners workbench fastener (typed FeaturePython)
  Placement = pos=(-21.3,1e-14,-9e-15) rot=(0,-1,0;1.5708rad)
  baseObject = -> Body003 [Edge18]
  diameter = 2
  invert = false
  leftHanded = false
  length = 5
  lengthCustom = 10
  matchOuter = false
  offset = 0
  thread = false
  type = 49
FEATURE [Part::FeaturePython] Screw002  label="M2x10-Screw001"  # Fasteners workbench fastener (typed FeaturePython)
  Placement = pos=(21.3,1e-14,1e-14) rot=(0,1,0;1.5708rad)
  baseObject = -> Body009 [Edge18]
  diameter = 2
  invert = false
  leftHanded = false
  length = 5
  lengthCustom = 10
  matchOuter = false
  offset = 0
  thread = false
  type = 49
FEATURE [Part::FeaturePython] Screw003  label="M3x14-Screw021"  # Fasteners workbench fastener (typed FeaturePython)
  Placement = pos=(-25.7,-1.09e-13,-53) rot=(0.969846,0.243717,0;3.14159rad)
  baseObject = -> Body007 [Edge86]
  diameter = 1
  invert = true
  leftHanded = false
  length = 6
  lengthCustom = 14
  matchOuter = false
  offset = 0
  thread = false
  type = 25
FEATURE [Part::FeaturePython] Nut003  label="M3-Nut060"  # Fasteners workbench fastener (typed FeaturePython)
  Placement = pos=(-25.7,-1.08e-13,-44.75) rot=(1,0,0;3.14159rad)
  baseObject = -> Screw003 [Edge71]
  diameter = 4
  invert = false
  leftHanded = false
  matchOuter = false
  offset = 5.75
  thread = false
  type = 25
FEATURE [Part::FeaturePython] Screw004  label="M3x14-Screw022"  # Fasteners workbench fastener (typed FeaturePython)
  Placement = pos=(25.7,-1.03e-13,-33) rot=(0.969846,-0.243717,0;3.14159rad)
  baseObject = -> Body015 [Edge87]
  diameter = 1
  invert = false
  leftHanded = false
  length = 6
  lengthCustom = 14
  matchOuter = false
  offset = 0
  thread = false
  type = 25
FEATURE [Part::FeaturePython] Nut004  label="M3-Nut061"  # Fasteners workbench fastener (typed FeaturePython)
  Placement = pos=(25.7,-1.04e-13,-24.75) rot=(1,0,0;3.14159rad)
  baseObject = -> Screw004 [Edge71]
  diameter = 4
  invert = false
  leftHanded = false
  matchOuter = false
  offset = 5.75
  thread = false
  type = 25
FEATURE [Part::FeaturePython] Screw005  label="M3x30-Screw"  # Fasteners workbench fastener (typed FeaturePython)
  Placement = pos=(-12.2,-8.9,20.85) rot=(0,-1,0;1.5708rad)
  baseObject = -> Body017 [Edge105]
  diameter = 1
  invert = false
  leftHanded = false
  length = 10
  lengthCustom = 30
  matchOuter = false
  offset = 0
  thread = false
  type = 25
FEATURE [Part::FeaturePython] Nut005  label="M3-Nut065"  # Fasteners workbench fastener (typed FeaturePython)
  Placement = pos=(12.2,-8.9,20.85) rot=(0,1,0;1.5708rad)
  baseObject = -> Body018 [Edge104]
  diameter = 4
  invert = true
  leftHanded = false
  matchOuter = false
  offset = 0
  thread = false
  type = 25
FEATURE [Part::FeaturePython] Screw006  label="M3x30-Screw001"  # Fasteners workbench fastener (typed FeaturePython)
  Placement = pos=(-12.2,8.9,20.85) rot=(0,-1,0;1.5708rad)
  baseObject = -> Body017 [Edge108]
  diameter = 1
  invert = false
  leftHanded = false
  length = 10
  lengthCustom = 30
  matchOuter = false
  offset = 0
  thread = false
  type = 25
FEATURE [Part::FeaturePython] Nut006  label="M3-Nut066"  # Fasteners workbench fastener (typed FeaturePython)
  Placement = pos=(12.2,8.9,20.85) rot=(0,1,0;1.5708rad)
  baseObject = -> Body018 [Edge107]
  diameter = 4
  invert = true
  leftHanded = false
  matchOuter = false
  offset = 0
  thread = false
  type = 25
FEATURE [App::DocumentObjectGroup] Group001  label="3D_prints"
  Group = -> [Body005,Body011,Body019,Body020,Body021]
FEATURE [Part::FeaturePython] Screw007  label="M3x14-Screw023"  # Fasteners workbench fastener (typed FeaturePython)
  Placement = pos=(15.5,-2.165e-12,10) rot=(0,-1,0;1.5708rad)
  baseObject = -> Body011 [Edge6]
  diameter = 1
  invert = false
  leftHanded = false
  length = 6
  lengthCustom = 14
  matchOuter = false
  offset = 0
  thread = false
  type = 25
FEATURE [Part::FeaturePython] Nut007  label="M3-Nut062"  # Fasteners workbench fastener (typed FeaturePython)
  Placement = pos=(29.5,-2.168e-12,10) rot=(0,-1,0;1.5708rad)
  baseObject = -> Screw007 [Edge71]
  diameter = 4
  invert = false
  leftHanded = false
  matchOuter = false
  offset = 0
  thread = false
  type = 25
FEATURE [App::DocumentObjectGroup] Group  label="Fasteners"
  Group = -> [Washer,Nut001,Washer001,Nut002,ThreadedRod,Screw,Nut,Screw001,Screw002,Screw003,Nut003,Screw004,Nut004,Screw005,Nut005,Screw006,Nut006,Screw007,Nut007]
FEATURE [PartDesign::SubShapeBinder] Binder022
  BindCopyOnChange = 0
  BindMode = 0
  ClaimChildren = false
  Context = -> Body025 [Binder022.]
  Fuse = false
  MakeFace = true
  OffsetFill = false
  OffsetIntersection = false
  OffsetJoinType = 0
  OffsetOpenResult = false
  PartialLoad = false
  Relative = true
  Support = -> [Body017[Pad007.]]
  _Version = 2
FEATURE [Sketcher::SketchObject] Sketch013
  ExternalGeometry = -> [Binder022]
  FullyConstrained = true
  MapMode = 5
  Placement = pos=(0,0,0) rot=(0.57735,0.57735,0.57735;2.0944rad)
  Support = -> [YZ_Plane026]
  sketch-geometry (4):
    g0: LineSegment StartX=38.15 StartY=36.85 StartZ=0 EndX=40.15 EndY=36.85 EndZ=0
    g1: LineSegment StartX=40.15 StartY=36.85 StartZ=0 EndX=40.15 EndY=35.85 EndZ=0
    g2: LineSegment StartX=40.15 StartY=35.85 StartZ=0 EndX=38.15 EndY=35.85 EndZ=0
    g3: LineSegment StartX=38.15 StartY=35.85 StartZ=0 EndX=38.15 EndY=36.85 EndZ=0
  constraints (11):
    c: Coincident(g0,g1)
    c: Coincident(g1,g2)
    c: Coincident(g2,g3)
    c: Coincident(g3,g0)
    c: Horizontal(g0)
    c: Horizontal(g2)
    c: Vertical(g1)
    c: Vertical(g3)
    c: DistanceX(g0,g0) = 2
    c: DistanceY(g1,g1) = 1
    c: Symmetric(g2,g1,g-3)
FEATURE [PartDesign::Pad] Pad013
  Direction = (1,-2e-16,3e-16)
  Length = 22.5
  Length2 = 10
  Midplane = true
  Placement = pos=(0,0,0) rot=(0.57735,0.57735,0.57735;2.0944rad)
  Profile = -> Sketch013
  ReferenceAxis = -> Sketch013 [N_Axis]
  Type = 0
FEATURE [PartDesign::FeaturePython] Bend  # WARN: FeaturePython — macro-defined, semantics opaque (R4)
  AutoMiter = true
  BaseFeature = -> Pad013
  BendType = 0
  LengthList = [26]
  LengthSpec = 0
  ReliefFactor = 0.7
  UseReliefFactor = false
  angle = 90
  baseObject = -> Pad013 [Face5]
  bendAList = [90]
  extend1 = 0
  extend2 = 0
  gap1 = 0
  gap2 = 0
  invert = false
  kfactor = 0.5
  length = 26
  maxExtendDist = 5
  minGap = 0.2
  minReliefGap = 1
  miterangle1 = 0
  miterangle2 = 0
  offset = 0
  radius = 1
  reliefType = 0
  reliefd = 1
  reliefw = 0.8
  sketchflip = false
  sketchinvert = false
  unfold = false
FEATURE [PartDesign::FeaturePython] Bend001  # WARN: FeaturePython — macro-defined, semantics opaque (R4)
  AutoMiter = true
  BaseFeature = -> Bend
  BendType = 0
  LengthList = [22.5]
  LengthSpec = 0
  ReliefFactor = 0.7
  UseReliefFactor = false
  angle = 90
  baseObject = -> Bend [Face3]
  bendAList = [90]
  extend1 = 0
  extend2 = 0
  gap1 = 0
  gap2 = 0
  invert = false
  kfactor = 0.5
  length = 22.5
  maxExtendDist = 5
  minGap = 0.2
  minReliefGap = 1
  miterangle1 = 0
  miterangle2 = 0
  offset = 0
  radius = 1
  reliefType = 0
  reliefd = 1
  reliefw = 0.8
  sketchflip = false
  sketchinvert = false
  unfold = false
FEATURE [PartDesign::SubShapeBinder] Binder023
  BindCopyOnChange = 0
  BindMode = 0
  ClaimChildren = false
  Context = -> Body025 [Binder023.]
  Fuse = false
  MakeFace = true
  OffsetFill = false
  OffsetIntersection = false
  OffsetJoinType = 0
  OffsetOpenResult = false
  PartialLoad = false
  Relative = true
  Support = -> [Body018[Clone008.]]
  _Version = 2
FEATURE [PartDesign::FeaturePython] Bend002  # WARN: FeaturePython — macro-defined, semantics opaque (R4)
  AutoMiter = true
  BaseFeature = -> Bend001
  BendType = 0
  LengthList = [26]
  LengthSpec = 0
  ReliefFactor = 0.7
  UseReliefFactor = false
  angle = 90
  baseObject = -> Bend001 [Face3]
  bendAList = [90]
  extend1 = 0
  extend2 = 0
  gap1 = 0
  gap2 = 0
  invert = false
  kfactor = 0.5
  length = 26
  maxExtendDist = 5
  minGap = 0.2
  minReliefGap = 1
  miterangle1 = 0
  miterangle2 = 0
  offset = 0
  radius = 1
  reliefType = 0
  reliefd = 1
  reliefw = 0.8
  sketchflip = false
  sketchinvert = false
  unfold = false
FEATURE [PartDesign::FeaturePython] Bend003  # WARN: FeaturePython — macro-defined, semantics opaque (R4)
  AutoMiter = true
  BaseFeature = -> Bend002
  BendType = 0
  LengthList = [0.1]
  LengthSpec = 0
  ReliefFactor = 0.7
  UseReliefFactor = false
  angle = 90
  baseObject = -> Bend002 [Face3]
  bendAList = [90]
  extend1 = 0
  extend2 = 0
  gap1 = 0
  gap2 = 0
  invert = false
  kfactor = 0.5
  length = 0.1
  maxExtendDist = 5
  minGap = 0.2
  minReliefGap = 1
  miterangle1 = 0
  miterangle2 = 0
  offset = 0
  radius = 1
  reliefType = 0
  reliefd = 1
  reliefw = 0.8
  sketchflip = false
  sketchinvert = false
  unfold = false
FEATURE [PartDesign::Fillet] Fillet002
  Base = -> Bend003 [Edge1,Edge2,Edge3,Edge4,Edge5,Edge6,Edge7,Edge8,Edge9,Edge10,Edge11,Edge12,Edge13,Edge14,Edge15,Edge16,Edge17,Edge18,Edge19,Edge20,Edge21,Edge22,Edge23,Edge24,Edge25,Edge26,Edge27,Edge28,Edge29,Edge30,Edge31,Edge32,Edge33,Edge34,Edge35,Edge36,Edge37,Edge38,Edge39,Edge40,+32 more]
  BaseFeature = -> Bend003
  Radius = 0.4
  Refine = true
  SupportTransform = false
  UseAllEdges = true
FEATURE [PartDesign::Body] Body025  label="elastic_band"
  Group = -> [Binder022,Sketch013,Pad013,Bend,Bend001,Binder023,Bend002,Bend003,Fillet002]
  Origin = -> Origin028
  Tip = -> Fillet002
FEATURE [PartDesign::SubShapeBinder] Binder024
  BindCopyOnChange = 0
  BindMode = 0
  ClaimChildren = false
  Context = -> Body026 [Binder024.]
  Fuse = false
  MakeFace = true
  OffsetFill = false
  OffsetIntersection = false
  OffsetJoinType = 0
  OffsetOpenResult = false
  PartialLoad = false
  Relative = true
  Support = -> [Body017[Pad007.]]
  _Version = 2
FEATURE [Sketcher::SketchObject] Sketch014
  ExternalGeometry = -> [Binder024]
  FullyConstrained = true
  MapMode = 5
  Placement = pos=(-9.4,0,0) rot=(0.57735,0.57735,0.57735;2.0944rad)
  Support = -> [Binder024]
  sketch-geometry (10):
    g0: ArcOfCircle CenterX=14.15 CenterY=31.85 CenterZ=0 NormalX=0 NormalY=0 NormalZ=1 AngleXU=0 Radius=3 StartAngle=1.5708 EndAngle=3.14159
    g1: LineSegment StartX=14.15 StartY=34.85 StartZ=0 EndX=39.15 EndY=34.85 EndZ=0
    g2: ArcOfCircle CenterX=39.15 CenterY=31.85 CenterZ=0 NormalX=0 NormalY=0 NormalZ=1 AngleXU=0 Radius=3 StartAngle=1e-16 EndAngle=1.5708
    g3: LineSegment StartX=42.15 StartY=31.85 StartZ=0 EndX=42.15 EndY=11.85 EndZ=0
    g4: ArcOfCircle CenterX=39.15 CenterY=11.85 CenterZ=0 NormalX=0 NormalY=0 NormalZ=1 AngleXU=0 Radius=3 StartAngle=4.71239 EndAngle=6.28319
    g5: LineSegment StartX=39.15 StartY=8.85 StartZ=0 EndX=14.15 EndY=8.85 EndZ=0
    g6: ArcOfCircle CenterX=14.15 CenterY=11.85 CenterZ=0 NormalX=0 NormalY=0 NormalZ=1 AngleXU=0 Radius=3 StartAngle=3.14159 EndAngle=4.71239
    g7: LineSegment StartX=11.15 StartY=11.85 StartZ=0 EndX=11.15 EndY=31.85 EndZ=0
    g8: GeomPoint X=11.15 Y=34.85 Z=0
    g9: GeomPoint X=42.15 Y=8.85 Z=0
  constraints (24):
    c: Tangent(g0,g1) = 1.5708
    c: Tangent(g1,g2) = 1.5708
    c: Tangent(g2,g3) = 1.5708
    c: Tangent(g3,g4) = 1.5708
    c: Tangent(g4,g5) = 1.5708
    c: Tangent(g5,g6) = 1.5708
    c: Tangent(g6,g7) = 1.5708
    c: Tangent(g7,g0) = 1.5708
    c: Horizontal(g1)
    c: Horizontal(g5)
    c: Vertical(g3)
    c: Vertical(g7)
    c: Equal(g0,g2)
    c: Equal(g2,g4)
    c: Equal(g4,g6)
    c: PointOnObject(g8,g1)
    c: PointOnObject(g8,g7)
    c: PointOnObject(g9,g3)
    c: PointOnObject(g9,g5)
    c: Radius(g0) = 3
    c: PointOnObject(g2,g-4)
    c: Vertical(g0,g-3)
    c: PointOnObject(g1,g-5)
    c: PointOnObject(g4,g-6)
FEATURE [PartDesign::Pad] Pad014
  Direction = (1,0,0)
  Length = 1
  Length2 = 10
  Profile = -> Sketch014
  ReferenceAxis = -> Sketch014 [N_Axis]
  Type = 0
FEATURE [PartDesign::Body] Body026  label="foam_battery_right"
  Group = -> [Binder024,Sketch014,Pad014]
  Origin = -> Origin029
  Tip = -> Pad014
FEATURE [PartDesign::FeatureBase] Clone011
  BaseFeature = -> Body026
FEATURE [PartDesign::Body] Body027  label="foam_battery_left"
  Group = -> [Clone011]
  Origin = -> Origin030
  Placement = pos=(17.8,0,0) rot=(0,0,1;0rad)
  Tip = -> Clone011
FEATURE [PartDesign::SubShapeBinder] Binder025
  BindCopyOnChange = 0
  BindMode = 0
  ClaimChildren = false
  Context = -> Body028 [Binder025.]
  Fuse = false
  MakeFace = true
  OffsetFill = false
  OffsetIntersection = false
  OffsetJoinType = 0
  OffsetOpenResult = false
  PartialLoad = false
  Relative = true
  Support = -> [Body007[Pad006.]]
  _Version = 2
FEATURE [Sketcher::SketchObject] Sketch015
  ExternalGeometry = -> [Binder025]
  FullyConstrained = true
  MapMode = 5
  Placement = pos=(2.92e-14,-1.081e-13,-53) rot=(1,0,0;3.14159rad)
  Support = -> [Binder025]
  sketch-geometry (21):
    g0: LineSegment StartX=-25.7 StartY=44 StartZ=0 EndX=12.3 EndY=44 EndZ=0
    g1: ArcOfCircle CenterX=12.3 CenterY=40 CenterZ=0 NormalX=0 NormalY=0 NormalZ=1 AngleXU=0 Radius=4 StartAngle=4.71239 EndAngle=7.85398
    g2: LineSegment StartX=12.3 StartY=36 StartZ=0 EndX=-15.7 EndY=36 EndZ=0
    g3: ArcOfCircle CenterX=-15.7 CenterY=31 CenterZ=0 NormalX=0 NormalY=0 NormalZ=1 AngleXU=0 Radius=5 StartAngle=1.5708 EndAngle=3.14159
    g4: LineSegment StartX=-20.7 StartY=31 StartZ=0 EndX=-20.7 EndY=16.345 EndZ=0
    g5: ArcOfCircle CenterX=-25.7 CenterY=10.1 CenterZ=0 NormalX=0 NormalY=0 NormalZ=1 AngleXU=0 Radius=8 StartAngle=1e-16 EndAngle=0.895665
    g6: LineSegment StartX=-17.7 StartY=10.1 StartZ=0 EndX=-17.7 EndY=-9.9 EndZ=0
    g7: ArcOfCircle CenterX=-25.7 CenterY=-9.9 CenterZ=0 NormalX=0 NormalY=0 NormalZ=1 AngleXU=0 Radius=8 StartAngle=5.38752 EndAngle=6.28319
    g8: LineSegment StartX=-20.7 StartY=-16.145 StartZ=0 EndX=-20.7 EndY=-47 EndZ=0
    g9: ArcOfCircle CenterX=-15.7 CenterY=-47 CenterZ=0 NormalX=0 NormalY=0 NormalZ=1 AngleXU=0 Radius=5 StartAngle=3.14159 EndAngle=4.71239
    g10: LineSegment StartX=-15.7 StartY=-52 StartZ=0 EndX=12.3 EndY=-52 EndZ=0
    g11: ArcOfCircle CenterX=12.3 CenterY=-56 CenterZ=0 NormalX=0 NormalY=0 NormalZ=1 AngleXU=0 Radius=4 StartAngle=4.71239 EndAngle=7.85398
    g12: LineSegment StartX=12.3 StartY=-60 StartZ=0 EndX=-25.7 EndY=-60 EndZ=0
    g13: ArcOfCircle CenterX=-25.7 CenterY=-55 CenterZ=0 NormalX=0 NormalY=0 NormalZ=1 AngleXU=0 Radius=5 StartAngle=3.14159 EndAngle=4.71239
    g14: LineSegment StartX=-30.7 StartY=-55 StartZ=0 EndX=-30.7 EndY=-16.145 EndZ=0
    g15: ArcOfCircle CenterX=-25.7 CenterY=-9.9 CenterZ=0 NormalX=0 NormalY=0 NormalZ=1 AngleXU=0 Radius=8 StartAngle=3.14159 EndAngle=4.03726
    g16: LineSegment StartX=-33.7 StartY=-9.9 StartZ=0 EndX=-33.7 EndY=10.1 EndZ=0
    g17: ArcOfCircle CenterX=-25.7 CenterY=10.1 CenterZ=0 NormalX=0 NormalY=0 NormalZ=1 AngleXU=0 Radius=8 StartAngle=2.24593 EndAngle=3.14159
    g18: LineSegment StartX=-30.7 StartY=16.345 StartZ=0 EndX=-30.7 EndY=39 EndZ=0
    g19: ArcOfCircle CenterX=-25.7 CenterY=39 CenterZ=0 NormalX=0 NormalY=0 NormalZ=1 AngleXU=0 Radius=5 StartAngle=1.5708 EndAngle=3.14159
    g20: Circle CenterX=-25.7 CenterY=0 CenterZ=0 NormalX=0 NormalY=0 NormalZ=1 AngleXU=0 Radius=4.5
  constraints (46):
    c: Horizontal(g0)
    c: Tangent(g0,g1) = 1.5708
    c: Horizontal(g2)
    c: Tangent(g2,g3) = -1.5708
    c: Vertical(g6)
    c: Tangent(g6,g7) = 1.5708
    c: Vertical(g8)
    c: Tangent(g8,g9) = -1.5708
    c: Horizontal(g10)
    c: Tangent(g10,g11) = 1.5708
    c: Tangent(g11,g12) = 1.5708
    c: Vertical(g14)
    c: Vertical(g16)
    c: Tangent(g16,g17) = 1.5708
    c: Vertical(g18)
    c: Tangent(g18,g19) = 1.5708
    c: Tangent(g19,g0) = 1.5708
    c: Tangent(g1,g2) = 1.5708
    c: Tangent(g3,g4) = -1.5708
    c: Tangent(g5,g6) = 1.5708
    c: Coincident(g17,g18)
    c: Coincident(g4,g5)
    c: Vertical(g4)
    c: Coincident(g7,g8)
    c: Tangent(g9,g10) = -1.5708
    c: Tangent(g13,g14) = 1.5708
    c: Coincident(g14,g15)
    c: Tangent(g15,g16) = 1.5708
    c: Coincident(g19,g-7)
    c: Coincident(g1,g-3)
    c: Coincident(g3,g-8)
    c: Coincident(g5,g-11)
    c: Coincident(g5,g17)
    c: Coincident(g7,g-13)
    c: Coincident(g15,g7)
    c: Coincident(g9,g-5)
    c: Coincident(g11,g-4)
    c: Coincident(g13,g-6)
    c: Equal(g1,g-3)
    c: Equal(g-11,g5)
    c: Equal(g-5,g9)
    c: Tangent(g12,g13) = 1.5708
    c: Equal(g13,g-6)
    c: Equal(g15,g-13)
    c: Coincident(g20,g-9)
    c: Diameter(g20) = 9
FEATURE [PartDesign::Pad] Pad015
  Direction = (5e-16,-2.2e-15,-1)
  Length = 2
  Length2 = 10
  Profile = -> Sketch015
  ReferenceAxis = -> Sketch015 [N_Axis]
  Type = 0
FEATURE [PartDesign::Body] Body028  label="foam_feet_right"
  Group = -> [Binder025,Sketch015,Pad015]
  Origin = -> Origin031
  Tip = -> Pad015
FEATURE [PartDesign::FeatureBase] Clone012
  BaseFeature = -> Body028
FEATURE [PartDesign::Body] Body029  label="foam_feet_left"
  Group = -> [Clone012]
  Origin = -> Origin032
  Placement = pos=(1.1e-14,0,-88) rot=(0,1,0;3.14159rad)
  Tip = -> Clone012
FEATURE [Part::Part2DObjectPython] Shape2DView  label="foam_battery_right_DXF"  # Draft 2D object (typed FeaturePython)
  AutoUpdate = true
  Base = -> Body026
  Clip = false
  FuseArch = false
  HiddenLines = false
  InPlace = true
  OnlySolids = false
  Projection = (-1,0,0)
  ProjectionMode = 0
  SegmentLength = 0.05
  Tessellation = false
  VisibleOnly = false
FEATURE [Part::Part2DObjectPython] Shape2DView001  label="foam_feet_right_DXF"  # Draft 2D object (typed FeaturePython)
  AutoUpdate = true
  Base = -> Body028
  Clip = false
  FuseArch = false
  HiddenLines = false
  InPlace = true
  OnlySolids = false
  Projection = (0,0,1)
  ProjectionMode = 0
  SegmentLength = 0.05
  Tessellation = false
  VisibleOnly = false
FEATURE [Part::Part2DObjectPython] Shape2DView002  label="foam_feet_left_DXF"  # Draft 2D object (typed FeaturePython)
  AutoUpdate = true
  Base = -> Body029
  Clip = false
  FuseArch = false
  HiddenLines = false
  InPlace = true
  OnlySolids = false
  Projection = (0,0,1)
  ProjectionMode = 0
  SegmentLength = 0.05
  Tessellation = false
  VisibleOnly = false
FEATURE [Part::Part2DObjectPython] Shape2DView003  label="foam_battery_left_DXF"  # Draft 2D object (typed FeaturePython)
  AutoUpdate = true
  Base = -> Body027
  Clip = false
  FuseArch = false
  HiddenLines = false
  InPlace = true
  OnlySolids = false
  Projection = (-1,0,0)
  ProjectionMode = 0
  SegmentLength = 0.05
  Tessellation = false
  VisibleOnly = false
FEATURE [Part::Part2DObjectPython] Shape2DView004  label="cam_right_1_DXF"  # Draft 2D object (typed FeaturePython)
  AutoUpdate = true
  Base = -> Body
  Clip = false
  FuseArch = false
  HiddenLines = false
  InPlace = true
  OnlySolids = false
  Projection = (-1,0,0)
  ProjectionMode = 0
  SegmentLength = 0.05
  Tessellation = false
  VisibleOnly = false
FEATURE [Part::Part2DObjectPython] Shape2DView005  label="cam_right_2_DXF"  # Draft 2D object (typed FeaturePython)
  AutoUpdate = true
  Base = -> Body003
  Clip = false
  FuseArch = false
  HiddenLines = false
  InPlace = true
  OnlySolids = false
  Projection = (-1,0,0)
  ProjectionMode = 0
  SegmentLength = 0.05
  Tessellation = false
  VisibleOnly = false
FEATURE [Part::Part2DObjectPython] Shape2DView006  label="cam_right_3_DXF"  # Draft 2D object (typed FeaturePython)
  AutoUpdate = true
  Base = -> Body004
  Clip = false
  FuseArch = false
  HiddenLines = false
  InPlace = true
  OnlySolids = false
  Projection = (-1,0,0)
  ProjectionMode = 0
  SegmentLength = 0.05
  Tessellation = false
  VisibleOnly = false
FEATURE [Part::Part2DObjectPython] Shape2DView008  label="cam_left_1_DXF"  # Draft 2D object (typed FeaturePython)
  AutoUpdate = true
  Base = -> Body008
  Clip = false
  FuseArch = false
  HiddenLines = false
  InPlace = true
  OnlySolids = false
  Projection = (1,0,0)
  ProjectionMode = 0
  SegmentLength = 0.05
  Tessellation = false
  VisibleOnly = false
FEATURE [Part::Part2DObjectPython] Shape2DView009  label="cam_left_2_DXF"  # Draft 2D object (typed FeaturePython)
  AutoUpdate = true
  Base = -> Body009
  Clip = false
  FuseArch = false
  HiddenLines = false
  InPlace = true
  OnlySolids = false
  Projection = (1,0,0)
  ProjectionMode = 0
  SegmentLength = 0.05
  Tessellation = false
  VisibleOnly = false
FEATURE [Part::Part2DObjectPython] Shape2DView010  label="cam_left_3_DXF"  # Draft 2D object (typed FeaturePython)
  AutoUpdate = true
  Base = -> Body010
  Clip = false
  FuseArch = false
  HiddenLines = false
  InPlace = true
  OnlySolids = false
  Projection = (1,0,0)
  ProjectionMode = 0
  SegmentLength = 0.05
  Tessellation = false
  VisibleOnly = false
FEATURE [Part::Part2DObjectPython] Shape2DView012  label="feet_right_DXF"  # Draft 2D object (typed FeaturePython)
  AutoUpdate = true
  Base = -> Body007
  Clip = false
  FuseArch = false
  HiddenLines = false
  InPlace = true
  OnlySolids = false
  Projection = (0,0,1)
  ProjectionMode = 0
  SegmentLength = 0.05
  Tessellation = false
  VisibleOnly = false
FEATURE [Part::Part2DObjectPython] Shape2DView013  label="feet_left_DXF"  # Draft 2D object (typed FeaturePython)
  AutoUpdate = true
  Base = -> Body015
  Clip = false
  FuseArch = false
  HiddenLines = false
  InPlace = true
  OnlySolids = false
  Projection = (0,0,1)
  ProjectionMode = 0
  SegmentLength = 0.05
  Tessellation = false
  VisibleOnly = false
FEATURE [Part::Part2DObjectPython] Shape2DView014  label="body_right_DXF"  # Draft 2D object (typed FeaturePython)
  AutoUpdate = true
  Base = -> Body017
  Clip = false
  FuseArch = false
  HiddenLines = false
  InPlace = true
  OnlySolids = false
  Projection = (-1,0,0)
  ProjectionMode = 0
  SegmentLength = 0.05
  Tessellation = false
  VisibleOnly = false
FEATURE [Part::Part2DObjectPython] Shape2DView015  label="body_left_DXF"  # Draft 2D object (typed FeaturePython)
  AutoUpdate = true
  Base = -> Body018
  Clip = false
  FuseArch = false
  HiddenLines = false
  InPlace = true
  OnlySolids = false
  Projection = (1,0,0)
  ProjectionMode = 0
  SegmentLength = 0.05
  Tessellation = false
  VisibleOnly = false
FEATURE [Part::Part2DObjectPython] Shape2DView016  label="arm_right_DXF"  # Draft 2D object (typed FeaturePython)
  AutoUpdate = true
  Base = -> Body024
  Clip = false
  FuseArch = false
  HiddenLines = false
  InPlace = true
  OnlySolids = false
  Projection = (1,0,0)
  ProjectionMode = 0
  SegmentLength = 0.05
  Tessellation = false
  VisibleOnly = false
FEATURE [Part::Part2DObjectPython] Shape2DView019  label="arm_left_DXF"  # Draft 2D object (typed FeaturePython)
  AutoUpdate = true
  Base = -> Body024
  Clip = false
  FuseArch = false
  HiddenLines = false
  InPlace = true
  OnlySolids = false
  Projection = (-1,0,0)
  ProjectionMode = 0
  SegmentLength = 0.05
  Tessellation = false
  VisibleOnly = false
FEATURE [PartDesign::SubShapeBinder] Binder028
  BindCopyOnChange = 0
  BindMode = 0
  ClaimChildren = false
  Context = -> Body030 [Binder028.]
  Fuse = false
  MakeFace = true
  OffsetFill = false
  OffsetIntersection = false
  OffsetJoinType = 0
  OffsetOpenResult = false
  PartialLoad = false
  Relative = true
  Support = -> [Body024]
  _Version = 2
FEATURE [PartDesign::SubShapeBinder] Binder029
  BindCopyOnChange = 0
  BindMode = 0
  ClaimChildren = false
  Context = -> Body030 [Binder029.]
  Fuse = false
  MakeFace = true
  OffsetFill = false
  OffsetIntersection = false
  OffsetJoinType = 0
  OffsetOpenResult = false
  PartialLoad = false
  Relative = true
  Support = -> [Body014]
  _Version = 2
FEATURE [Sketcher::SketchObject] Sketch016
  ExternalGeometry = -> [Binder028,Binder029]
  FullyConstrained = true
  MapMode = 5
  Placement = pos=(27.1,3.3e-15,1.4e-15) rot=(0.57735,0.57735,0.57735;2.0944rad)
  Support = -> [Binder029]
  sketch-geometry (3):
    g0: LineSegment StartX=43.8765 StartY=76.4783 StartZ=0 EndX=7.42656 EndY=40.422 EndZ=0
    g1: LineSegment StartX=7.42656 StartY=40.422 StartZ=0 EndX=7 EndY=40 EndZ=0
    g2: LineSegment StartX=43.8765 StartY=76.4783 StartZ=0 EndX=44.3031 EndY=76.9002 EndZ=0
  constraints (8):
    c: Coincident(g1,g0)
    c: Parallel(g1,g0)
    c: Coincident(g2,g0)
    c: Parallel(g2,g0)
    c: Coincident(g1,g-4)
    c: PointOnObject(g0,g-4)
    c: Coincident(g2,g-3)
    c: PointOnObject(g0,g-3)
FEATURE [PartDesign::Plane] DatumPlane005
  AttachmentOffset = pos=(0,0,0) rot=(1,0,0;1.5708rad)
  Length = 72.3981
  MapMode = 7
  Placement = pos=(27.1,43.8765,76.4783) rot=(0,0.924915,0.380174;3.14159rad)
  ResizeMode = 0
  Support = -> [Sketch016]
  Width = 138.227
FEATURE [Sketcher::SketchObject] Sketch017
  ExternalGeometry = -> [Binder028,Binder029]
  FullyConstrained = true
  MapMode = 5
  Placement = pos=(27.1,43.8765,76.4783) rot=(0,0.924915,0.380174;3.14159rad)
  Support = -> [DatumPlane005]
  sketch-geometry (9):
    g0: LineSegment StartX=-3.3e-14 StartY=-52.3704 StartZ=0 EndX=2.8 EndY=-52.3704 EndZ=0
    g1: LineSegment StartX=-2.9 StartY=0.6 StartZ=0 EndX=-0.1 EndY=0.6 EndZ=0
    g2: ArcOfCircle CenterX=2.8 CenterY=-51.8704 CenterZ=0 NormalX=0 NormalY=0 NormalZ=1 AngleXU=0 Radius=0.5 StartAngle=4.71239 EndAngle=6.28319
    g3: LineSegment StartX=3.3 StartY=-51.8704 StartZ=0 EndX=3.3 EndY=-47.8704 EndZ=0
    g4: ArcOfCircle CenterX=-2.9 CenterY=0.1 CenterZ=0 NormalX=0 NormalY=0 NormalZ=1 AngleXU=0 Radius=0.5 StartAngle=1.5708 EndAngle=3.14159
    g5: LineSegment StartX=-3.4 StartY=0.1 StartZ=0 EndX=-3.4 EndY=-3.9 EndZ=0
    g6: ArcOfCircle CenterX=-0.1 CenterY=0.1 CenterZ=0 NormalX=0 NormalY=0 NormalZ=1 AngleXU=0 Radius=0.5 StartAngle=6.26587 EndAngle=7.85398
    g7: ArcOfCircle CenterX=-3.55e-14 CenterY=-51.8704 CenterZ=0 NormalX=0 NormalY=0 NormalZ=1 AngleXU=0 Radius=0.5 StartAngle=3.12427 EndAngle=4.71239
    g8: LineSegment StartX=-0.499925 StartY=-51.8618 StartZ=0 EndX=0.399925 EndY=0.0913411 EndZ=0
  constraints (20):
    c: Tangent(g2,g0) = -1.5708
    c: Tangent(g3,g2) = -1.5708
    c: Radius(g2) = 0.5
    c: Perpendicular(g0,g3)
    c: Distance(g3) = 4
    c: Tangent(g4,g1) = 1.5708
    c: Perpendicular(g5,g1)
    c: Equal(g4,g2)
    c: Equal(g3,g5)
    c: Tangent(g4,g5) = -1.5708
    c: Tangent(g0,g7) = -1.5708
    c: Tangent(g6,g1) = 1.5708
    c: Equal(g6,g4)
    c: Equal(g7,g2)
    c: Tangent(g6,g8) = -1.5708
    c: Tangent(g8,g7) = 1.5708
    c: Symmetric(g-5,g-5,g7)
    c: Symmetric(g-6,g-6,g2)
    c: Symmetric(g-3,g-3,g1)
    c: Symmetric(g-4,g-4,g1)
FEATURE [PartDesign::Plane] DatumPlane006
  AttachmentOffset = pos=(0,0,4) rot=(0,0,1;0rad)
  Length = 72.415
  MapMode = 7
  Placement = pos=(30.5,41.1039,73.7355) rot=(1,0,0;2.35076rad)
  ResizeMode = 0
  Support = -> [Sketch017]
  Width = 138.494
FEATURE [Sketcher::SketchObject] Sketch018
  FullyConstrained = true
  MapMode = 5
  Placement = pos=(30.5,41.1039,73.7355) rot=(1,0,0;2.35076rad)
  Support = -> [DatumPlane006]
  sketch-geometry (1):
    g0: Circle CenterX=0 CenterY=0 CenterZ=0 NormalX=0 NormalY=0 NormalZ=1 AngleXU=0 Radius=0.4
  constraints (2):
    c: Diameter(g0) = 0.8
    c: Coincident(g0,g-1)
FEATURE [PartDesign::AdditivePipe] AdditivePipe
  AuxilleryCurvelinear = true
  AuxillerySpineTangent = false
  Binormal = (0,0,0)
  Mode = 0
  Placement = pos=(30.5,41.1039,73.7355) rot=(1,0,0;2.35076rad)
  Profile = -> Sketch018
  Spine = -> Sketch017 [Edge1,Edge2,Edge3,Edge4,Edge5,Edge6,Edge7,Edge8,Edge9]
  SpineTangent = false
  Transformation = 0
  Transition = 0
FEATURE [PartDesign::Body] Body030  label="brass_wire_left"
  Group = -> [Binder028,Binder029,Sketch016,DatumPlane005,Sketch017,DatumPlane006,Sketch018,AdditivePipe]
  Origin = -> Origin033
  Tip = -> AdditivePipe
FEATURE [PartDesign::FeatureBase] Clone013
  BaseFeature = -> Body030
FEATURE [PartDesign::Body] Body031  label="brass_wire_right"
  Group = -> [Clone013]
  Origin = -> Origin034
  Placement = pos=(-4e-15,-32.75,11.6) rot=(0,0.694658,0.71934;3.14159rad)
  Tip = -> Clone013
FEATURE [App::DocumentObjectGroup] Group003  label="other_parts"
  Group = -> [Part001,batt_9V005_cp_sp,Body025,Body026,Body027,Body028,Body029,Body030,Body031]
FEATURE [TechDraw::DrawSVGTemplate] Template
  Height = 210
  Orientation = 1
  Template = <userpath>/Documents/FreeCAD/Templates/A4_Landscape_blank.svg
  Width = 297
FEATURE [TechDraw::DrawViewPart] View
  CoarseView = false
  Direction = (0,-0.707107,0.707107)
  Focus = 100
  HardHidden = false
  IsoCount = 0
  IsoHidden = false
  IsoVisible = false
  LockPosition = false
  Perspective = false
  Rotation = 0
  ScaleType = 0
  ScrubCount = 0
  SeamHidden = false
  SeamVisible = false
  SmoothHidden = false
  SmoothVisible = true
  Source = -> [Body030]
  X = 148.5
  XDirection = (0,0.707107,0.707107)
  Y = 105
FEATURE [TechDraw::DrawViewDimension] Dimension001
  AngleOverride = false
  Arbitrary = false
  ArbitraryTolerances = false
  EqualTolerance = true
  ExtensionAngle = 0
  FormatSpec = %.2w
  FormatSpecOverTolerance = %+.2w
  FormatSpecUnderTolerance = %+.2w
  Inverted = false
  LineAngle = 0
  LockPosition = false
  MeasureType = 1
  OverTolerance = 0
  References2D = -> [View]
  Rotation = 0
  ScaleType = 0
  TheoreticalExact = false
  Type = 1
  UnderTolerance = 0
  X = -15.7775
  Y = 11.3138
FEATURE [TechDraw::DrawViewDimension] Dimension002
  AngleOverride = false
  Arbitrary = false
  ArbitraryTolerances = false
  EqualTolerance = true
  ExtensionAngle = 0
  FormatSpec = %.2w
  FormatSpecOverTolerance = %+.2w
  FormatSpecUnderTolerance = %+.2w
  Inverted = false
  LineAngle = 0
  LockPosition = false
  MeasureType = 1
  OverTolerance = 0
  References2D = -> [View]
  Rotation = 0
  ScaleType = 0
  TheoreticalExact = false
  Type = 2
  UnderTolerance = 0
  X = -41.2836
  Y = 11.8169
FEATURE [TechDraw::DrawViewDimension] Dimension
  AngleOverride = false
  Arbitrary = false
  ArbitraryTolerances = false
  EqualTolerance = true
  ExtensionAngle = 0
  FormatSpec = %.2w
  FormatSpecOverTolerance = %+.2w
  FormatSpecUnderTolerance = %+.2w
  Inverted = false
  LineAngle = 0
  LockPosition = false
  MeasureType = 1
  OverTolerance = 0
  References2D = -> [View]
  Rotation = 0
  ScaleType = 0
  TheoreticalExact = false
  Type = 2
  UnderTolerance = 0
  X = 36.672
  Y = 8.64568
FEATURE [TechDraw::DrawViewDimension] Dimension003
  AngleOverride = false
  Arbitrary = false
  ArbitraryTolerances = false
  EqualTolerance = true
  ExtensionAngle = 0
  FormatSpec = %.2w
  FormatSpecOverTolerance = %+.2w
  FormatSpecUnderTolerance = %+.2w
  Inverted = false
  LineAngle = 0
  LockPosition = false
  MeasureType = 1
  OverTolerance = 0
  References2D = -> [View]
  Rotation = 0
  ScaleType = 0
  TheoreticalExact = false
  Type = 1
  UnderTolerance = 0
  X = 15.7775
  Y = -14.8137
FEATURE [TechDraw::DrawViewDimension] Dimension004
  AngleOverride = false
  Arbitrary = false
  ArbitraryTolerances = false
  EqualTolerance = true
  ExtensionAngle = 0
  FormatSpec = %.2w
  FormatSpecOverTolerance = %+.2w
  FormatSpecUnderTolerance = %+.2w
  Inverted = false
  LineAngle = 0
  LockPosition = false
  MeasureType = 1
  OverTolerance = 0
  References2D = -> [View]
  Rotation = 0
  ScaleType = 0
  TheoreticalExact = false
  Type = 1
  UnderTolerance = 0
  X = 1.18251
  Y = -21.3199
FEATURE [TechDraw::DrawViewAnnotation] Annotation
  Font = Droid Sans Mono
  LineSpace = 100
  LockPosition = false
  MaxWidth = -1
  Rotation = 0
  ScaleType = 0
  Text = Brass Wire, 0.8mm dia | length  = 4+4+2.8+2.8+51.95 | length = approx 66 mm long
  TextSize = 3
  TextStyle = 0
  X = 150.297
  Y = 144.338
FEATURE [TechDraw::DrawPage] Page
  KeepUpdated = true
  NextBalloonIndex = 1
  ProjectionType = 1
  Template = -> Template
  Views = -> [View,Dimension001,Dimension002,Dimension,Dimension003,Dimension004,Annotation]
FEATURE [Sketcher::SketchObject] Sketch019
  FullyConstrained = true
  MapMode = 5
  Placement = pos=(-27.1,7.1e-15,-1.82e-14) rot=(0.57735,-0.57735,-0.57735;2.0944rad)
  Support = -> [Fillet001]
  sketch-geometry (1):
    g0: Circle CenterX=0 CenterY=0 CenterZ=0 NormalX=0 NormalY=0 NormalZ=1 AngleXU=0 Radius=3.5
  constraints (2):
    c: Coincident(g0,g-1)
    c: Diameter(g0) = 7
FEATURE [PartDesign::Pocket] Pocket
  BaseFeature = -> Fillet001
  Direction = (1,-1e-16,5e-16)
  Length = 5
  Length2 = 5
  Placement = pos=(-24.3,8e-15,-1.4e-14) rot=(0.57735,-0.57735,-0.57735;2.0944rad)
  Profile = -> Sketch019
  ReferenceAxis = -> Sketch019 [N_Axis]
  Type = 1
FEATURE [PartDesign::Body] Body002  label="leg_right"
  Group = -> [Sketch001,Binder001,Binder004,DatumPlane003,Pad004,Fillet,Fillet001,Sketch019,Pocket]
  Origin = -> Origin003
  Tip = -> Pocket
FEATURE [PartDesign::FeatureBase] Clone006
  BaseFeature = -> Body002
FEATURE [PartDesign::Body] Body014  label="leg_left"
  Group = -> [Clone006]
  Origin = -> Origin016
  Placement = pos=(0,0,20) rot=(0,0,1;3.14159rad)
  Tip = -> Clone006
FEATURE [Part::Part2DObjectPython] Shape2DView007  label="leg_right_DXF"  # Draft 2D object (typed FeaturePython)
  AutoUpdate = true
  Base = -> Body002
  Clip = false
  FuseArch = false
  HiddenLines = false
  InPlace = true
  OnlySolids = false
  Projection = (-1,0,0)
  ProjectionMode = 0
  SegmentLength = 0.05
  Tessellation = false
  VisibleOnly = false
FEATURE [Part::Part2DObjectPython] Shape2DView011  label="leg_left_DXF"  # Draft 2D object (typed FeaturePython)
  AutoUpdate = true
  Base = -> Body014
  Clip = false
  FuseArch = false
  HiddenLines = false
  InPlace = true
  OnlySolids = false
  Projection = (1,0,0)
  ProjectionMode = 0
  SegmentLength = 0.05
  Tessellation = false
  VisibleOnly = false
FEATURE [Sketcher::SketchObject] Sketch020  label="Sketch_MuSo"
  AttachmentOffset = pos=(-8.7,-37,-84) rot=(0,0,1;-1.5708rad)
  FullyConstrained = false
  MapMode = 5
  Placement = pos=(12.7,-8.7,8.53e-14) rot=(0,0,1;0rad)
  Support = -> [Pocket]
  sketch-geometry (369):
    g0: BSplineCurve PolesCount=2 KnotsCount=2 Degree=1 IsPeriodic=0
    g1: BSplineCurve PolesCount=2 KnotsCount=2 Degree=1 IsPeriodic=0
    g2: BSplineCurve PolesCount=4 KnotsCount=2 Degree=3 IsPeriodic=0
    g3: BSplineCurve PolesCount=2 KnotsCount=2 Degree=1 IsPeriodic=0
    g4: BSplineCurve PolesCount=4 KnotsCount=2 Degree=3 IsPeriodic=0
    g5: BSplineCurve PolesCount=2 KnotsCount=2 Degree=1 IsPeriodic=0
    g6: BSplineCurve PolesCount=2 KnotsCount=2 Degree=1 IsPeriodic=0
    g7: BSplineCurve PolesCount=2 KnotsCount=2 Degree=1 IsPeriodic=0
    g8: BSplineCurve PolesCount=4 KnotsCount=2 Degree=3 IsPeriodic=0
    g9: BSplineCurve PolesCount=2 KnotsCount=2 Degree=1 IsPeriodic=0
    g10: BSplineCurve PolesCount=4 KnotsCount=2 Degree=3 IsPeriodic=0
    g11: BSplineCurve PolesCount=2 KnotsCount=2 Degree=1 IsPeriodic=0
    g12: BSplineCurve PolesCount=2 KnotsCount=2 Degree=1 IsPeriodic=0
    g13: BSplineCurve PolesCount=2 KnotsCount=2 Degree=1 IsPeriodic=0
    g14: BSplineCurve PolesCount=2 KnotsCount=2 Degree=1 IsPeriodic=0
    g15: BSplineCurve PolesCount=2 KnotsCount=2 Degree=1 IsPeriodic=0
    g16: BSplineCurve PolesCount=4 KnotsCount=2 Degree=3 IsPeriodic=0
    g17: BSplineCurve PolesCount=2 KnotsCount=2 Degree=1 IsPeriodic=0
    g18: BSplineCurve PolesCount=4 KnotsCount=2 Degree=3 IsPeriodic=0
    g19: BSplineCurve PolesCount=2 KnotsCount=2 Degree=1 IsPeriodic=0
    g20: BSplineCurve PolesCount=2 KnotsCount=2 Degree=1 IsPeriodic=0
    g21: BSplineCurve PolesCount=2 KnotsCount=2 Degree=1 IsPeriodic=0
    g22: BSplineCurve PolesCount=2 KnotsCount=2 Degree=1 IsPeriodic=0
    g23: BSplineCurve PolesCount=2 KnotsCount=2 Degree=1 IsPeriodic=0
    g24: BSplineCurve PolesCount=2 KnotsCount=2 Degree=1 IsPeriodic=0
    g25: BSplineCurve PolesCount=4 KnotsCount=2 Degree=3 IsPeriodic=0
    g26: BSplineCurve PolesCount=2 KnotsCount=2 Degree=1 IsPeriodic=0
    g27: BSplineCurve PolesCount=4 KnotsCount=2 Degree=3 IsPeriodic=0
    g28: BSplineCurve PolesCount=4 KnotsCount=2 Degree=3 IsPeriodic=0
    g29: BSplineCurve PolesCount=2 KnotsCount=2 Degree=1 IsPeriodic=0
    g30: BSplineCurve PolesCount=2 KnotsCount=2 Degree=1 IsPeriodic=0
    g31: BSplineCurve PolesCount=2 KnotsCount=2 Degree=1 IsPeriodic=0
    g32: BSplineCurve PolesCount=4 KnotsCount=2 Degree=3 IsPeriodic=0
    g33: BSplineCurve PolesCount=4 KnotsCount=2 Degree=3 IsPeriodic=0
    g34: BSplineCurve PolesCount=2 KnotsCount=2 Degree=1 IsPeriodic=0
    g35: BSplineCurve PolesCount=2 KnotsCount=2 Degree=1 IsPeriodic=0
    g36: BSplineCurve PolesCount=4 KnotsCount=2 Degree=3 IsPeriodic=0
    g37: BSplineCurve PolesCount=4 KnotsCount=2 Degree=3 IsPeriodic=0
    g38: BSplineCurve PolesCount=4 KnotsCount=2 Degree=3 IsPeriodic=0
    g39: BSplineCurve PolesCount=4 KnotsCount=2 Degree=3 IsPeriodic=0
    g40: BSplineCurve PolesCount=2 KnotsCount=2 Degree=1 IsPeriodic=0
    g41: BSplineCurve PolesCount=4 KnotsCount=2 Degree=3 IsPeriodic=0
    g42: BSplineCurve PolesCount=4 KnotsCount=2 Degree=3 IsPeriodic=0
    g43: BSplineCurve PolesCount=4 KnotsCount=2 Degree=3 IsPeriodic=0
    g44: BSplineCurve PolesCount=4 KnotsCount=2 Degree=3 IsPeriodic=0
    g45: BSplineCurve PolesCount=4 KnotsCount=2 Degree=3 IsPeriodic=0
    g46: BSplineCurve PolesCount=2 KnotsCount=2 Degree=1 IsPeriodic=0
    g47: BSplineCurve PolesCount=4 KnotsCount=2 Degree=3 IsPeriodic=0
    g48: BSplineCurve PolesCount=4 KnotsCount=2 Degree=3 IsPeriodic=0
    g49: BSplineCurve PolesCount=4 KnotsCount=2 Degree=3 IsPeriodic=0
    g50: BSplineCurve PolesCount=4 KnotsCount=2 Degree=3 IsPeriodic=0
    g51: BSplineCurve PolesCount=4 KnotsCount=2 Degree=3 IsPeriodic=0
    g52: BSplineCurve PolesCount=4 KnotsCount=2 Degree=3 IsPeriodic=0
    g53: BSplineCurve PolesCount=4 KnotsCount=2 Degree=3 IsPeriodic=0
    g54: BSplineCurve PolesCount=4 KnotsCount=2 Degree=3 IsPeriodic=0
    g55: BSplineCurve PolesCount=4 KnotsCount=2 Degree=3 IsPeriodic=0
    g56: BSplineCurve PolesCount=2 KnotsCount=2 Degree=1 IsPeriodic=0
    g57: BSplineCurve PolesCount=2 KnotsCount=2 Degree=1 IsPeriodic=0
    g58: BSplineCurve PolesCount=2 KnotsCount=2 Degree=1 IsPeriodic=0
    g59: BSplineCurve PolesCount=2 KnotsCount=2 Degree=1 IsPeriodic=0
    g60: BSplineCurve PolesCount=2 KnotsCount=2 Degree=1 IsPeriodic=0
    g61: BSplineCurve PolesCount=2 KnotsCount=2 Degree=1 IsPeriodic=0
    g62: BSplineCurve PolesCount=2 KnotsCount=2 Degree=1 IsPeriodic=0
    g63: BSplineCurve PolesCount=2 KnotsCount=2 Degree=1 IsPeriodic=0
    g64: BSplineCurve PolesCount=2 KnotsCount=2 Degree=1 IsPeriodic=0
    g65: BSplineCurve PolesCount=2 KnotsCount=2 Degree=1 IsPeriodic=0
    g66: BSplineCurve PolesCount=4 KnotsCount=2 Degree=3 IsPeriodic=0
    g67: BSplineCurve PolesCount=2 KnotsCount=2 Degree=1 IsPeriodic=0
    g68: BSplineCurve PolesCount=4 KnotsCount=2 Degree=3 IsPeriodic=0
    g69: BSplineCurve PolesCount=2 KnotsCount=2 Degree=1 IsPeriodic=0
    g70: BSplineCurve PolesCount=2 KnotsCount=2 Degree=1 IsPeriodic=0
    g71: BSplineCurve PolesCount=2 KnotsCount=2 Degree=1 IsPeriodic=0
    g72: BSplineCurve PolesCount=4 KnotsCount=2 Degree=3 IsPeriodic=0
    g73: BSplineCurve PolesCount=2 KnotsCount=2 Degree=1 IsPeriodic=0
    g74: BSplineCurve PolesCount=4 KnotsCount=2 Degree=3 IsPeriodic=0
    g75: BSplineCurve PolesCount=2 KnotsCount=2 Degree=1 IsPeriodic=0
    g76: BSplineCurve PolesCount=2 KnotsCount=2 Degree=1 IsPeriodic=0
    g77: BSplineCurve PolesCount=2 KnotsCount=2 Degree=1 IsPeriodic=0
    g78: BSplineCurve PolesCount=2 KnotsCount=2 Degree=1 IsPeriodic=0
    g79: BSplineCurve PolesCount=2 KnotsCount=2 Degree=1 IsPeriodic=0
    g80: BSplineCurve PolesCount=4 KnotsCount=2 Degree=3 IsPeriodic=0
    g81: BSplineCurve PolesCount=2 KnotsCount=2 Degree=1 IsPeriodic=0
    g82: BSplineCurve PolesCount=4 KnotsCount=2 Degree=3 IsPeriodic=0
    g83: BSplineCurve PolesCount=2 KnotsCount=2 Degree=1 IsPeriodic=0
    g84: BSplineCurve PolesCount=2 KnotsCount=2 Degree=1 IsPeriodic=0
    g85: BSplineCurve PolesCount=2 KnotsCount=2 Degree=1 IsPeriodic=0
    g86: BSplineCurve PolesCount=2 KnotsCount=2 Degree=1 IsPeriodic=0
    g87: BSplineCurve PolesCount=4 KnotsCount=2 Degree=3 IsPeriodic=0
    g88: BSplineCurve PolesCount=4 KnotsCount=2 Degree=3 IsPeriodic=0
    g89: BSplineCurve PolesCount=2 KnotsCount=2 Degree=1 IsPeriodic=0
    g90: BSplineCurve PolesCount=4 KnotsCount=2 Degree=3 IsPeriodic=0
    g91: BSplineCurve PolesCount=4 KnotsCount=2 Degree=3 IsPeriodic=0
    g92: BSplineCurve PolesCount=2 KnotsCount=2 Degree=1 IsPeriodic=0
    g93: BSplineCurve PolesCount=2 KnotsCount=2 Degree=1 IsPeriodic=0
    g94: BSplineCurve PolesCount=2 KnotsCount=2 Degree=1 IsPeriodic=0
    g95: BSplineCurve PolesCount=4 KnotsCount=2 Degree=3 IsPeriodic=0
    g96: BSplineCurve PolesCount=4 KnotsCount=2 Degree=3 IsPeriodic=0
    g97: BSplineCurve PolesCount=2 KnotsCount=2 Degree=1 IsPeriodic=0
    g98: BSplineCurve PolesCount=2 KnotsCount=2 Degree=1 IsPeriodic=0
    g99: BSplineCurve PolesCount=2 KnotsCount=2 Degree=1 IsPeriodic=0
    g100: BSplineCurve PolesCount=4 KnotsCount=2 Degree=3 IsPeriodic=0
    g101: BSplineCurve PolesCount=4 KnotsCount=2 Degree=3 IsPeriodic=0
    g102: BSplineCurve PolesCount=2 KnotsCount=2 Degree=1 IsPeriodic=0
    g103: BSplineCurve PolesCount=4 KnotsCount=2 Degree=3 IsPeriodic=0
    g104: BSplineCurve PolesCount=4 KnotsCount=2 Degree=3 IsPeriodic=0
    g105: BSplineCurve PolesCount=4 KnotsCount=2 Degree=3 IsPeriodic=0
    g106: BSplineCurve PolesCount=4 KnotsCount=2 Degree=3 IsPeriodic=0
    g107: BSplineCurve PolesCount=4 KnotsCount=2 Degree=3 IsPeriodic=0
    g108: BSplineCurve PolesCount=2 KnotsCount=2 Degree=1 IsPeriodic=0
    g109: BSplineCurve PolesCount=4 KnotsCount=2 Degree=3 IsPeriodic=0
    g110: BSplineCurve PolesCount=4 KnotsCount=2 Degree=3 IsPeriodic=0
    g111: BSplineCurve PolesCount=4 KnotsCount=2 Degree=3 IsPeriodic=0
    g112: BSplineCurve PolesCount=4 KnotsCount=2 Degree=3 IsPeriodic=0
    g113: BSplineCurve PolesCount=4 KnotsCount=2 Degree=3 IsPeriodic=0
    g114: BSplineCurve PolesCount=4 KnotsCount=2 Degree=3 IsPeriodic=0
    g115: BSplineCurve PolesCount=2 KnotsCount=2 Degree=1 IsPeriodic=0
    g116: BSplineCurve PolesCount=4 KnotsCount=2 Degree=3 IsPeriodic=0
    g117: BSplineCurve PolesCount=2 KnotsCount=2 Degree=1 IsPeriodic=0
    g118: BSplineCurve PolesCount=4 KnotsCount=2 Degree=3 IsPeriodic=0
    g119: BSplineCurve PolesCount=4 KnotsCount=2 Degree=3 IsPeriodic=0
    g120: BSplineCurve PolesCount=4 KnotsCount=2 Degree=3 IsPeriodic=0
    g121: BSplineCurve PolesCount=4 KnotsCount=2 Degree=3 IsPeriodic=0
    g122: BSplineCurve PolesCount=4 KnotsCount=2 Degree=3 IsPeriodic=0
    g123: BSplineCurve PolesCount=2 KnotsCount=2 Degree=1 IsPeriodic=0
    g124: BSplineCurve PolesCount=4 KnotsCount=2 Degree=3 IsPeriodic=0
    g125: BSplineCurve PolesCount=4 KnotsCount=2 Degree=3 IsPeriodic=0
    g126: BSplineCurve PolesCount=2 KnotsCount=2 Degree=1 IsPeriodic=0
    g127: BSplineCurve PolesCount=4 KnotsCount=2 Degree=3 IsPeriodic=0
    g128: BSplineCurve PolesCount=4 KnotsCount=2 Degree=3 IsPeriodic=0
    g129: BSplineCurve PolesCount=4 KnotsCount=2 Degree=3 IsPeriodic=0
    g130: BSplineCurve PolesCount=4 KnotsCount=2 Degree=3 IsPeriodic=0
    g131: BSplineCurve PolesCount=4 KnotsCount=2 Degree=3 IsPeriodic=0
    g132: BSplineCurve PolesCount=2 KnotsCount=2 Degree=1 IsPeriodic=0
    g133: BSplineCurve PolesCount=4 KnotsCount=2 Degree=3 IsPeriodic=0
    g134: BSplineCurve PolesCount=4 KnotsCount=2 Degree=3 IsPeriodic=0
    g135: BSplineCurve PolesCount=2 KnotsCount=2 Degree=1 IsPeriodic=0
    g136: BSplineCurve PolesCount=2 KnotsCount=2 Degree=1 IsPeriodic=0
    g137: BSplineCurve PolesCount=2 KnotsCount=2 Degree=1 IsPeriodic=0
    g138: BSplineCurve PolesCount=4 KnotsCount=2 Degree=3 IsPeriodic=0
    g139: BSplineCurve PolesCount=4 KnotsCount=2 Degree=3 IsPeriodic=0
    g140: BSplineCurve PolesCount=2 KnotsCount=2 Degree=1 IsPeriodic=0
    g141: BSplineCurve PolesCount=2 KnotsCount=2 Degree=1 IsPeriodic=0
    g142: BSplineCurve PolesCount=2 KnotsCount=2 Degree=1 IsPeriodic=0
    g143: BSplineCurve PolesCount=4 KnotsCount=2 Degree=3 IsPeriodic=0
    g144: BSplineCurve PolesCount=4 KnotsCount=2 Degree=3 IsPeriodic=0
    g145: BSplineCurve PolesCount=2 KnotsCount=2 Degree=1 IsPeriodic=0
    g146: BSplineCurve PolesCount=4 KnotsCount=2 Degree=3 IsPeriodic=0
    g147: BSplineCurve PolesCount=4 KnotsCount=2 Degree=3 IsPeriodic=0
    g148: BSplineCurve PolesCount=2 KnotsCount=2 Degree=1 IsPeriodic=0
    g149: BSplineCurve PolesCount=4 KnotsCount=2 Degree=3 IsPeriodic=0
    g150: BSplineCurve PolesCount=4 KnotsCount=2 Degree=3 IsPeriodic=0
    g151: BSplineCurve PolesCount=2 KnotsCount=2 Degree=1 IsPeriodic=0
    g152: BSplineCurve PolesCount=2 KnotsCount=2 Degree=1 IsPeriodic=0
    g153: BSplineCurve PolesCount=2 KnotsCount=2 Degree=1 IsPeriodic=0
    g154: BSplineCurve PolesCount=4 KnotsCount=2 Degree=3 IsPeriodic=0
    g155: BSplineCurve PolesCount=4 KnotsCount=2 Degree=3 IsPeriodic=0
    g156: BSplineCurve PolesCount=2 KnotsCount=2 Degree=1 IsPeriodic=0
    g157: BSplineCurve PolesCount=2 KnotsCount=2 Degree=1 IsPeriodic=0
    g158: BSplineCurve PolesCount=2 KnotsCount=2 Degree=1 IsPeriodic=0
    g159: BSplineCurve PolesCount=2 KnotsCount=2 Degree=1 IsPeriodic=0
    g160: BSplineCurve PolesCount=4 KnotsCount=2 Degree=3 IsPeriodic=0
    g161: BSplineCurve PolesCount=2 KnotsCount=2 Degree=1 IsPeriodic=0
    g162: BSplineCurve PolesCount=4 KnotsCount=2 Degree=3 IsPeriodic=0
    g163: BSplineCurve PolesCount=4 KnotsCount=2 Degree=3 IsPeriodic=0
    g164: BSplineCurve PolesCount=4 KnotsCount=2 Degree=3 IsPeriodic=0
    g165: BSplineCurve PolesCount=4 KnotsCount=2 Degree=3 IsPeriodic=0
    g166: BSplineCurve PolesCount=2 KnotsCount=2 Degree=1 IsPeriodic=0
    g167: BSplineCurve PolesCount=4 KnotsCount=2 Degree=3 IsPeriodic=0
    g168: BSplineCurve PolesCount=4 KnotsCount=2 Degree=3 IsPeriodic=0
    g169: BSplineCurve PolesCount=2 KnotsCount=2 Degree=1 IsPeriodic=0
    g170: BSplineCurve PolesCount=4 KnotsCount=2 Degree=3 IsPeriodic=0
    g171: BSplineCurve PolesCount=4 KnotsCount=2 Degree=3 IsPeriodic=0
    g172: BSplineCurve PolesCount=4 KnotsCount=2 Degree=3 IsPeriodic=0
    g173: BSplineCurve PolesCount=4 KnotsCount=2 Degree=3 IsPeriodic=0
    g174: BSplineCurve PolesCount=4 KnotsCount=2 Degree=3 IsPeriodic=0
    g175: BSplineCurve PolesCount=4 KnotsCount=2 Degree=3 IsPeriodic=0
    g176: BSplineCurve PolesCount=4 KnotsCount=2 Degree=3 IsPeriodic=0
    g177: BSplineCurve PolesCount=4 KnotsCount=2 Degree=3 IsPeriodic=0
    g178: BSplineCurve PolesCount=2 KnotsCount=2 Degree=1 IsPeriodic=0
    g179: BSplineCurve PolesCount=2 KnotsCount=2 Degree=1 IsPeriodic=0
    g180: BSplineCurve PolesCount=2 KnotsCount=2 Degree=1 IsPeriodic=0
    g181: BSplineCurve PolesCount=2 KnotsCount=2 Degree=1 IsPeriodic=0
    g182: BSplineCurve PolesCount=2 KnotsCount=2 Degree=1 IsPeriodic=0
    g183: BSplineCurve PolesCount=2 KnotsCount=2 Degree=1 IsPeriodic=0
    g184: BSplineCurve PolesCount=2 KnotsCount=2 Degree=1 IsPeriodic=0
    g185: BSplineCurve PolesCount=2 KnotsCount=2 Degree=1 IsPeriodic=0
    g186: BSplineCurve PolesCount=2 KnotsCount=2 Degree=1 IsPeriodic=0
    g187: BSplineCurve PolesCount=2 KnotsCount=2 Degree=1 IsPeriodic=0
    g188: BSplineCurve PolesCount=4 KnotsCount=2 Degree=3 IsPeriodic=0
    g189: BSplineCurve PolesCount=4 KnotsCount=2 Degree=3 IsPeriodic=0
    g190: BSplineCurve PolesCount=2 KnotsCount=2 Degree=1 IsPeriodic=0
    g191: BSplineCurve PolesCount=4 KnotsCount=2 Degree=3 IsPeriodic=0
    g192: BSplineCurve PolesCount=4 KnotsCount=2 Degree=3 IsPeriodic=0
    g193: BSplineCurve PolesCount=2 KnotsCount=2 Degree=1 IsPeriodic=0
    g194: BSplineCurve PolesCount=4 KnotsCount=2 Degree=3 IsPeriodic=0
    g195: BSplineCurve PolesCount=4 KnotsCount=2 Degree=3 IsPeriodic=0
    g196: BSplineCurve PolesCount=4 KnotsCount=2 Degree=3 IsPeriodic=0
    g197: BSplineCurve PolesCount=4 KnotsCount=2 Degree=3 IsPeriodic=0
    g198: BSplineCurve PolesCount=2 KnotsCount=2 Degree=1 IsPeriodic=0
    g199: BSplineCurve PolesCount=4 KnotsCount=2 Degree=3 IsPeriodic=0
    g200: BSplineCurve PolesCount=4 KnotsCount=2 Degree=3 IsPeriodic=0
    g201: BSplineCurve PolesCount=4 KnotsCount=2 Degree=3 IsPeriodic=0
    g202: BSplineCurve PolesCount=4 KnotsCount=2 Degree=3 IsPeriodic=0
    g203: BSplineCurve PolesCount=4 KnotsCount=2 Degree=3 IsPeriodic=0
    g204: BSplineCurve PolesCount=2 KnotsCount=2 Degree=1 IsPeriodic=0
    g205: BSplineCurve PolesCount=4 KnotsCount=2 Degree=3 IsPeriodic=0
    g206: BSplineCurve PolesCount=4 KnotsCount=2 Degree=3 IsPeriodic=0
    g207: BSplineCurve PolesCount=4 KnotsCount=2 Degree=3 IsPeriodic=0
    g208: BSplineCurve PolesCount=4 KnotsCount=2 Degree=3 IsPeriodic=0
    g209: BSplineCurve PolesCount=4 KnotsCount=2 Degree=3 IsPeriodic=0
    g210: BSplineCurve PolesCount=4 KnotsCount=2 Degree=3 IsPeriodic=0
    g211: BSplineCurve PolesCount=4 KnotsCount=2 Degree=3 IsPeriodic=0
    g212: BSplineCurve PolesCount=4 KnotsCount=2 Degree=3 IsPeriodic=0
    g213: BSplineCurve PolesCount=4 KnotsCount=2 Degree=3 IsPeriodic=0
    g214: BSplineCurve PolesCount=2 KnotsCount=2 Degree=1 IsPeriodic=0
    g215: BSplineCurve PolesCount=2 KnotsCount=2 Degree=1 IsPeriodic=0
    g216: BSplineCurve PolesCount=2 KnotsCount=2 Degree=1 IsPeriodic=0
    g217: BSplineCurve PolesCount=2 KnotsCount=2 Degree=1 IsPeriodic=0
    g218: BSplineCurve PolesCount=4 KnotsCount=2 Degree=3 IsPeriodic=0
    g219: BSplineCurve PolesCount=4 KnotsCount=2 Degree=3 IsPeriodic=0
    g220: BSplineCurve PolesCount=2 KnotsCount=2 Degree=1 IsPeriodic=0
    g221: BSplineCurve PolesCount=4 KnotsCount=2 Degree=3 IsPeriodic=0
    g222: BSplineCurve PolesCount=4 KnotsCount=2 Degree=3 IsPeriodic=0
    g223: BSplineCurve PolesCount=2 KnotsCount=2 Degree=1 IsPeriodic=0
    g224: BSplineCurve PolesCount=2 KnotsCount=2 Degree=1 IsPeriodic=0
    g225: BSplineCurve PolesCount=2 KnotsCount=2 Degree=1 IsPeriodic=0
    g226: BSplineCurve PolesCount=4 KnotsCount=2 Degree=3 IsPeriodic=0
    g227: BSplineCurve PolesCount=4 KnotsCount=2 Degree=3 IsPeriodic=0
    g228: BSplineCurve PolesCount=2 KnotsCount=2 Degree=1 IsPeriodic=0
    g229: BSplineCurve PolesCount=2 KnotsCount=2 Degree=1 IsPeriodic=0
    g230: BSplineCurve PolesCount=2 KnotsCount=2 Degree=1 IsPeriodic=0
    g231: BSplineCurve PolesCount=4 KnotsCount=2 Degree=3 IsPeriodic=0
    g232: BSplineCurve PolesCount=4 KnotsCount=2 Degree=3 IsPeriodic=0
    g233: BSplineCurve PolesCount=2 KnotsCount=2 Degree=1 IsPeriodic=0
    g234: BSplineCurve PolesCount=4 KnotsCount=2 Degree=3 IsPeriodic=0
    g235: BSplineCurve PolesCount=4 KnotsCount=2 Degree=3 IsPeriodic=0
    g236: BSplineCurve PolesCount=2 KnotsCount=2 Degree=1 IsPeriodic=0
    g237: BSplineCurve PolesCount=2 KnotsCount=2 Degree=1 IsPeriodic=0
    g238: BSplineCurve PolesCount=2 KnotsCount=2 Degree=1 IsPeriodic=0
    g239: BSplineCurve PolesCount=2 KnotsCount=2 Degree=1 IsPeriodic=0
    g240: BSplineCurve PolesCount=2 KnotsCount=2 Degree=1 IsPeriodic=0
    g241: BSplineCurve PolesCount=2 KnotsCount=2 Degree=1 IsPeriodic=0
    g242: BSplineCurve PolesCount=2 KnotsCount=2 Degree=1 IsPeriodic=0
    g243: BSplineCurve PolesCount=2 KnotsCount=2 Degree=1 IsPeriodic=0
    g244: BSplineCurve PolesCount=2 KnotsCount=2 Degree=1 IsPeriodic=0
    g245: BSplineCurve PolesCount=2 KnotsCount=2 Degree=1 IsPeriodic=0
    g246: BSplineCurve PolesCount=2 KnotsCount=2 Degree=1 IsPeriodic=0
    g247: BSplineCurve PolesCount=4 KnotsCount=2 Degree=3 IsPeriodic=0
    g248: BSplineCurve PolesCount=4 KnotsCount=2 Degree=3 IsPeriodic=0
    g249: BSplineCurve PolesCount=2 KnotsCount=2 Degree=1 IsPeriodic=0
    g250: BSplineCurve PolesCount=4 KnotsCount=2 Degree=3 IsPeriodic=0
    g251: BSplineCurve PolesCount=4 KnotsCount=2 Degree=3 IsPeriodic=0
    g252: BSplineCurve PolesCount=4 KnotsCount=2 Degree=3 IsPeriodic=0
    g253: BSplineCurve PolesCount=4 KnotsCount=2 Degree=3 IsPeriodic=0
    g254: BSplineCurve PolesCount=2 KnotsCount=2 Degree=1 IsPeriodic=0
    g255: BSplineCurve PolesCount=2 KnotsCount=2 Degree=1 IsPeriodic=0
    g256: BSplineCurve PolesCount=2 KnotsCount=2 Degree=1 IsPeriodic=0
    g257: BSplineCurve PolesCount=2 KnotsCount=2 Degree=1 IsPeriodic=0
    g258: BSplineCurve PolesCount=4 KnotsCount=2 Degree=3 IsPeriodic=0
    g259: BSplineCurve PolesCount=4 KnotsCount=2 Degree=3 IsPeriodic=0
    g260: BSplineCurve PolesCount=4 KnotsCount=2 Degree=3 IsPeriodic=0
    g261: BSplineCurve PolesCount=4 KnotsCount=2 Degree=3 IsPeriodic=0
    g262: BSplineCurve PolesCount=4 KnotsCount=2 Degree=3 IsPeriodic=0
    g263: BSplineCurve PolesCount=4 KnotsCount=2 Degree=3 IsPeriodic=0
    g264: BSplineCurve PolesCount=4 KnotsCount=2 Degree=3 IsPeriodic=0
    g265: BSplineCurve PolesCount=4 KnotsCount=2 Degree=3 IsPeriodic=0
    g266: BSplineCurve PolesCount=4 KnotsCount=2 Degree=3 IsPeriodic=0
    g267: BSplineCurve PolesCount=4 KnotsCount=2 Degree=3 IsPeriodic=0
    g268: BSplineCurve PolesCount=2 KnotsCount=2 Degree=1 IsPeriodic=0
    g269: BSplineCurve PolesCount=4 KnotsCount=2 Degree=3 IsPeriodic=0
    g270: BSplineCurve PolesCount=4 KnotsCount=2 Degree=3 IsPeriodic=0
    g271: BSplineCurve PolesCount=2 KnotsCount=2 Degree=1 IsPeriodic=0
    g272: BSplineCurve PolesCount=2 KnotsCount=2 Degree=1 IsPeriodic=0
    g273: BSplineCurve PolesCount=2 KnotsCount=2 Degree=1 IsPeriodic=0
    g274: BSplineCurve PolesCount=2 KnotsCount=2 Degree=1 IsPeriodic=0
    g275: BSplineCurve PolesCount=4 KnotsCount=2 Degree=3 IsPeriodic=0
    g276: BSplineCurve PolesCount=2 KnotsCount=2 Degree=1 IsPeriodic=0
    g277: BSplineCurve PolesCount=4 KnotsCount=2 Degree=3 IsPeriodic=0
    g278: BSplineCurve PolesCount=4 KnotsCount=2 Degree=3 IsPeriodic=0
    g279: BSplineCurve PolesCount=2 KnotsCount=2 Degree=1 IsPeriodic=0
    g280: BSplineCurve PolesCount=4 KnotsCount=2 Degree=3 IsPeriodic=0
    g281: BSplineCurve PolesCount=4 KnotsCount=2 Degree=3 IsPeriodic=0
    g282: BSplineCurve PolesCount=2 KnotsCount=2 Degree=1 IsPeriodic=0
    g283: BSplineCurve PolesCount=4 KnotsCount=2 Degree=3 IsPeriodic=0
    g284: BSplineCurve PolesCount=4 KnotsCount=2 Degree=3 IsPeriodic=0
    g285: BSplineCurve PolesCount=4 KnotsCount=2 Degree=3 IsPeriodic=0
    g286: BSplineCurve PolesCount=4 KnotsCount=2 Degree=3 IsPeriodic=0
    g287: BSplineCurve PolesCount=4 KnotsCount=2 Degree=3 IsPeriodic=0
    g288: BSplineCurve PolesCount=2 KnotsCount=2 Degree=1 IsPeriodic=0
    g289: BSplineCurve PolesCount=4 KnotsCount=2 Degree=3 IsPeriodic=0
    g290: BSplineCurve PolesCount=4 KnotsCount=2 Degree=3 IsPeriodic=0
    g291: BSplineCurve PolesCount=4 KnotsCount=2 Degree=3 IsPeriodic=0
    g292: BSplineCurve PolesCount=4 KnotsCount=2 Degree=3 IsPeriodic=0
    g293: BSplineCurve PolesCount=4 KnotsCount=2 Degree=3 IsPeriodic=0
    g294: BSplineCurve PolesCount=4 KnotsCount=2 Degree=3 IsPeriodic=0
    g295: BSplineCurve PolesCount=2 KnotsCount=2 Degree=1 IsPeriodic=0
    g296: BSplineCurve PolesCount=4 KnotsCount=2 Degree=3 IsPeriodic=0
    g297: BSplineCurve PolesCount=4 KnotsCount=2 Degree=3 IsPeriodic=0
    g298: BSplineCurve PolesCount=4 KnotsCount=2 Degree=3 IsPeriodic=0
    g299: BSplineCurve PolesCount=4 KnotsCount=2 Degree=3 IsPeriodic=0
    g300: BSplineCurve PolesCount=4 KnotsCount=2 Degree=3 IsPeriodic=0
    g301: BSplineCurve PolesCount=4 KnotsCount=2 Degree=3 IsPeriodic=0
    g302: BSplineCurve PolesCount=4 KnotsCount=2 Degree=3 IsPeriodic=0
    g303: BSplineCurve PolesCount=4 KnotsCount=2 Degree=3 IsPeriodic=0
    g304: BSplineCurve PolesCount=4 KnotsCount=2 Degree=3 IsPeriodic=0
    g305: BSplineCurve PolesCount=4 KnotsCount=2 Degree=3 IsPeriodic=0
    g306: BSplineCurve PolesCount=4 KnotsCount=2 Degree=3 IsPeriodic=0
    g307: BSplineCurve PolesCount=4 KnotsCount=2 Degree=3 IsPeriodic=0
    g308: BSplineCurve PolesCount=4 KnotsCount=2 Degree=3 IsPeriodic=0
    g309: BSplineCurve PolesCount=4 KnotsCount=2 Degree=3 IsPeriodic=0
    g310: BSplineCurve PolesCount=4 KnotsCount=2 Degree=3 IsPeriodic=0
    g311: BSplineCurve PolesCount=4 KnotsCount=2 Degree=3 IsPeriodic=0
    g312: BSplineCurve PolesCount=4 KnotsCount=2 Degree=3 IsPeriodic=0
    g313: BSplineCurve PolesCount=4 KnotsCount=2 Degree=3 IsPeriodic=0
    g314: BSplineCurve PolesCount=4 KnotsCount=2 Degree=3 IsPeriodic=0
    g315: BSplineCurve PolesCount=4 KnotsCount=2 Degree=3 IsPeriodic=0
    g316: BSplineCurve PolesCount=4 KnotsCount=2 Degree=3 IsPeriodic=0
    g317: BSplineCurve PolesCount=4 KnotsCount=2 Degree=3 IsPeriodic=0
    g318: BSplineCurve PolesCount=4 KnotsCount=2 Degree=3 IsPeriodic=0
    g319: BSplineCurve PolesCount=4 KnotsCount=2 Degree=3 IsPeriodic=0
    g320: BSplineCurve PolesCount=4 KnotsCount=2 Degree=3 IsPeriodic=0
    g321: BSplineCurve PolesCount=4 KnotsCount=2 Degree=3 IsPeriodic=0
    g322: BSplineCurve PolesCount=4 KnotsCount=2 Degree=3 IsPeriodic=0
    g323: BSplineCurve PolesCount=4 KnotsCount=2 Degree=3 IsPeriodic=0
    g324: BSplineCurve PolesCount=4 KnotsCount=2 Degree=3 IsPeriodic=0
    g325: BSplineCurve PolesCount=4 KnotsCount=2 Degree=3 IsPeriodic=0
    g326: BSplineCurve PolesCount=2 KnotsCount=2 Degree=1 IsPeriodic=0
    g327: BSplineCurve PolesCount=4 KnotsCount=2 Degree=3 IsPeriodic=0
    g328: BSplineCurve PolesCount=4 KnotsCount=2 Degree=3 IsPeriodic=0
    g329: BSplineCurve PolesCount=4 KnotsCount=2 Degree=3 IsPeriodic=0
    g330: BSplineCurve PolesCount=4 KnotsCount=2 Degree=3 IsPeriodic=0
    g331: BSplineCurve PolesCount=4 KnotsCount=2 Degree=3 IsPeriodic=0
    g332: BSplineCurve PolesCount=4 KnotsCount=2 Degree=3 IsPeriodic=0
    g333: BSplineCurve PolesCount=4 KnotsCount=2 Degree=3 IsPeriodic=0
    g334: BSplineCurve PolesCount=4 KnotsCount=2 Degree=3 IsPeriodic=0
    g335: BSplineCurve PolesCount=4 KnotsCount=2 Degree=3 IsPeriodic=0
    g336: BSplineCurve PolesCount=2 KnotsCount=2 Degree=1 IsPeriodic=0
    g337: BSplineCurve PolesCount=4 KnotsCount=2 Degree=3 IsPeriodic=0
    g338: BSplineCurve PolesCount=4 KnotsCount=2 Degree=3 IsPeriodic=0
    g339: BSplineCurve PolesCount=4 KnotsCount=2 Degree=3 IsPeriodic=0
    g340: BSplineCurve PolesCount=4 KnotsCount=2 Degree=3 IsPeriodic=0
    g341: BSplineCurve PolesCount=4 KnotsCount=2 Degree=3 IsPeriodic=0
    g342: BSplineCurve PolesCount=4 KnotsCount=2 Degree=3 IsPeriodic=0
    g343: BSplineCurve PolesCount=4 KnotsCount=2 Degree=3 IsPeriodic=0
    g344: BSplineCurve PolesCount=4 KnotsCount=2 Degree=3 IsPeriodic=0
    g345: BSplineCurve PolesCount=4 KnotsCount=2 Degree=3 IsPeriodic=0
    g346: BSplineCurve PolesCount=4 KnotsCount=2 Degree=3 IsPeriodic=0
    g347: BSplineCurve PolesCount=4 KnotsCount=2 Degree=3 IsPeriodic=0
    g348: BSplineCurve PolesCount=4 KnotsCount=2 Degree=3 IsPeriodic=0
    g349: BSplineCurve PolesCount=4 KnotsCount=2 Degree=3 IsPeriodic=0
    g350: BSplineCurve PolesCount=4 KnotsCount=2 Degree=3 IsPeriodic=0
    g351: BSplineCurve PolesCount=4 KnotsCount=2 Degree=3 IsPeriodic=0
    g352: BSplineCurve PolesCount=4 KnotsCount=2 Degree=3 IsPeriodic=0
    g353: BSplineCurve PolesCount=4 KnotsCount=2 Degree=3 IsPeriodic=0
    g354: BSplineCurve PolesCount=4 KnotsCount=2 Degree=3 IsPeriodic=0
    g355: BSplineCurve PolesCount=4 KnotsCount=2 Degree=3 IsPeriodic=0
    g356: BSplineCurve PolesCount=4 KnotsCount=2 Degree=3 IsPeriodic=0
    g357: BSplineCurve PolesCount=4 KnotsCount=2 Degree=3 IsPeriodic=0
    g358: BSplineCurve PolesCount=4 KnotsCount=2 Degree=3 IsPeriodic=0
    g359: BSplineCurve PolesCount=4 KnotsCount=2 Degree=3 IsPeriodic=0
    g360: BSplineCurve PolesCount=4 KnotsCount=2 Degree=3 IsPeriodic=0
    g361: BSplineCurve PolesCount=4 KnotsCount=2 Degree=3 IsPeriodic=0
    g362: BSplineCurve PolesCount=4 KnotsCount=2 Degree=3 IsPeriodic=0
    g363: BSplineCurve PolesCount=4 KnotsCount=2 Degree=3 IsPeriodic=0
    g364: BSplineCurve PolesCount=4 KnotsCount=2 Degree=3 IsPeriodic=0
    g365: BSplineCurve PolesCount=4 KnotsCount=2 Degree=3 IsPeriodic=0
    g366: BSplineCurve PolesCount=4 KnotsCount=2 Degree=3 IsPeriodic=0
    g367: BSplineCurve PolesCount=4 KnotsCount=2 Degree=3 IsPeriodic=0
    g368: BSplineCurve PolesCount=4 KnotsCount=2 Degree=3 IsPeriodic=0
  constraints (369):
    c: Coincident(g0,g1)
    c: Coincident(g1,g2)
    c: Coincident(g2,g3)
    c: Coincident(g3,g4)
    c: Coincident(g4,g5)
    c: Coincident(g5,g6)
    c: Coincident(g6,g7)
    c: Coincident(g7,g8)
    c: Coincident(g8,g9)
    c: Coincident(g9,g10)
    c: Coincident(g10,g11)
    c: Coincident(g11,g12)
    c: Coincident(g12,g13)
    c: Coincident(g13,g14)
    c: Coincident(g14,g15)
    c: Coincident(g15,g16)
    c: Coincident(g16,g17)
    c: Coincident(g17,g18)
    c: Coincident(g18,g19)
    c: Coincident(g19,g20)
    c: Coincident(g20,g21)
    c: Coincident(g21,g22)
    c: Coincident(g22,g0)
    c: Coincident(g23,g24)
    c: Coincident(g24,g25)
    c: Coincident(g25,g26)
    c: Coincident(g26,g27)
    c: Coincident(g27,g28)
    c: Coincident(g28,g29)
    c: Coincident(g29,g30)
    c: Coincident(g30,g31)
    c: Coincident(g31,g32)
    c: Coincident(g32,g33)
    c: Coincident(g33,g34)
    c: Coincident(g34,g35)
    c: Coincident(g35,g23)
    c: Coincident(g36,g37)
    c: Coincident(g37,g38)
    c: Coincident(g38,g39)
    c: Coincident(g39,g40)
    c: Coincident(g40,g41)
    c: Coincident(g41,g42)
    c: Coincident(g42,g43)
    c: Coincident(g43,g44)
    c: Coincident(g44,g45)
    c: Coincident(g45,g46)
    c: Coincident(g46,g47)
    c: Coincident(g47,g36)
    c: Coincident(g48,g49)
    c: Coincident(g49,g50)
    c: Coincident(g50,g51)
    c: Coincident(g51,g48)
    c: Coincident(g52,g53)
    c: Coincident(g53,g54)
    c: Coincident(g54,g55)
    c: Coincident(g55,g52)
    c: Coincident(g56,g57)
    c: Coincident(g57,g58)
    c: Coincident(g58,g59)
    c: Coincident(g59,g56)
    c: Coincident(g60,g61)
    c: Coincident(g61,g62)
    c: Coincident(g62,g63)
    c: Coincident(g63,g60)
    c: Coincident(g64,g65)
    c: Coincident(g65,g66)
    c: Coincident(g66,g67)
    c: Coincident(g67,g68)
    c: Coincident(g68,g69)
    c: Coincident(g69,g70)
    c: Coincident(g70,g71)
    c: Coincident(g71,g72)
    c: Coincident(g72,g73)
    c: Coincident(g73,g74)
    c: Coincident(g74,g75)
    c: Coincident(g75,g76)
    c: Coincident(g76,g77)
    c: Coincident(g77,g78)
    c: Coincident(g78,g79)
    c: Coincident(g79,g80)
    c: Coincident(g80,g81)
    c: Coincident(g81,g82)
    c: Coincident(g82,g83)
    c: Coincident(g83,g84)
    c: Coincident(g84,g85)
    c: Coincident(g85,g86)
    c: Coincident(g86,g64)
    c: Coincident(g87,g88)
    c: Coincident(g88,g89)
    c: Coincident(g89,g90)
    c: Coincident(g90,g91)
    c: Coincident(g91,g92)
    c: Coincident(g92,g93)
    c: Coincident(g93,g94)
    c: Coincident(g94,g95)
    c: Coincident(g95,g96)
    c: Coincident(g96,g97)
    c: Coincident(g97,g98)
    c: Coincident(g98,g99)
    c: Coincident(g99,g100)
    c: Coincident(g100,g101)
    c: Coincident(g101,g102)
    c: Coincident(g102,g87)
    c: Coincident(g103,g104)
    c: Coincident(g104,g105)
    c: Coincident(g105,g106)
    c: Coincident(g106,g107)
    c: Coincident(g107,g108)
    c: Coincident(g108,g109)
    c: Coincident(g109,g110)
    c: Coincident(g110,g111)
    c: Coincident(g111,g112)
    c: Coincident(g112,g113)
    c: Coincident(g113,g114)
    c: Coincident(g114,g115)
    c: Coincident(g115,g116)
    c: Coincident(g116,g103)
    c: Coincident(g117,g118)
    c: Coincident(g118,g119)
    c: Coincident(g119,g120)
    c: Coincident(g120,g121)
    c: Coincident(g121,g122)
    c: Coincident(g122,g123)
    c: Coincident(g123,g124)
    c: Coincident(g124,g125)
    c: Coincident(g125,g117)
    c: Coincident(g126,g127)
    c: Coincident(g127,g128)
    c: Coincident(g128,g129)
    c: Coincident(g129,g126)
    c: Coincident(g130,g131)
    c: Coincident(g131,g132)
    c: Coincident(g132,g133)
    c: Coincident(g133,g134)
    c: Coincident(g134,g135)
    c: Coincident(g135,g136)
    c: Coincident(g136,g137)
    c: Coincident(g137,g138)
    c: Coincident(g138,g139)
    c: Coincident(g139,g140)
    c: Coincident(g140,g141)
    c: Coincident(g141,g142)
    c: Coincident(g142,g143)
    c: Coincident(g143,g144)
    c: Coincident(g144,g145)
    c: Coincident(g145,g130)
    c: Coincident(g146,g147)
    c: Coincident(g147,g148)
    c: Coincident(g148,g149)
    c: Coincident(g149,g150)
    c: Coincident(g150,g151)
    c: Coincident(g151,g152)
    c: Coincident(g152,g153)
    c: Coincident(g153,g154)
    c: Coincident(g154,g155)
    c: Coincident(g155,g156)
    c: Coincident(g156,g157)
    c: Coincident(g157,g158)
    c: Coincident(g158,g159)
    c: Coincident(g159,g160)
    c: Coincident(g160,g161)
    c: Coincident(g161,g162)
    c: Coincident(g162,g163)
    c: Coincident(g163,g164)
    c: Coincident(g164,g165)
    c: Coincident(g165,g166)
    c: Coincident(g166,g167)
    c: Coincident(g167,g168)
    c: Coincident(g168,g169)
    c: Coincident(g169,g146)
    c: Coincident(g170,g171)
    c: Coincident(g171,g172)
    c: Coincident(g172,g173)
    c: Coincident(g173,g170)
    c: Coincident(g174,g175)
    c: Coincident(g175,g176)
    c: Coincident(g176,g177)
    c: Coincident(g177,g174)
    c: Coincident(g178,g179)
    c: Coincident(g179,g180)
    c: Coincident(g180,g181)
    c: Coincident(g181,g182)
    c: Coincident(g182,g183)
    c: Coincident(g183,g184)
    c: Coincident(g184,g185)
    c: Coincident(g185,g186)
    c: Coincident(g186,g187)
    c: Coincident(g187,g188)
    c: Coincident(g188,g189)
    c: Coincident(g189,g190)
    c: Coincident(g190,g191)
    c: Coincident(g191,g192)
    c: Coincident(g192,g193)
    c: Coincident(g193,g178)
    c: Coincident(g194,g195)
    c: Coincident(g195,g196)
    c: Coincident(g196,g197)
    c: Coincident(g197,g198)
    c: Coincident(g198,g199)
    c: Coincident(g199,g200)
    c: Coincident(g200,g201)
    c: Coincident(g201,g202)
    c: Coincident(g202,g203)
    c: Coincident(g203,g204)
    c: Coincident(g204,g205)
    c: Coincident(g205,g194)
    c: Coincident(g206,g207)
    c: Coincident(g207,g208)
    c: Coincident(g208,g209)
    c: Coincident(g209,g206)
    c: Coincident(g210,g211)
    c: Coincident(g211,g212)
    c: Coincident(g212,g213)
    c: Coincident(g213,g210)
    c: Coincident(g214,g215)
    c: Coincident(g215,g216)
    c: Coincident(g216,g217)
    c: Coincident(g217,g214)
    c: Coincident(g218,g219)
    c: Coincident(g219,g220)
    c: Coincident(g220,g221)
    c: Coincident(g221,g222)
    c: Coincident(g222,g223)
    c: Coincident(g223,g224)
    c: Coincident(g224,g225)
    c: Coincident(g225,g226)
    c: Coincident(g226,g227)
    c: Coincident(g227,g228)
    c: Coincident(g228,g229)
    c: Coincident(g229,g230)
    c: Coincident(g230,g231)
    c: Coincident(g231,g232)
    c: Coincident(g232,g233)
    c: Coincident(g233,g218)
    c: Coincident(g234,g235)
    c: Coincident(g235,g236)
    c: Coincident(g236,g237)
    c: Coincident(g237,g238)
    c: Coincident(g238,g239)
    c: Coincident(g239,g240)
    c: Coincident(g240,g241)
    c: Coincident(g241,g242)
    c: Coincident(g242,g243)
    c: Coincident(g243,g244)
    c: Coincident(g244,g245)
    c: Coincident(g245,g246)
    c: Coincident(g246,g247)
    c: Coincident(g247,g248)
    c: Coincident(g248,g249)
    c: Coincident(g249,g234)
    c: Coincident(g250,g251)
    c: Coincident(g251,g252)
    c: Coincident(g252,g253)
    c: Coincident(g253,g250)
    c: Coincident(g254,g255)
    c: Coincident(g255,g256)
    c: Coincident(g256,g257)
    c: Coincident(g257,g254)
    c: Coincident(g258,g259)
    c: Coincident(g259,g260)
    c: Coincident(g260,g261)
    c: Coincident(g261,g258)
    c: Coincident(g262,g263)
    c: Coincident(g263,g264)
    c: Coincident(g264,g265)
    c: Coincident(g265,g262)
    c: Coincident(g266,g267)
    c: Coincident(g267,g268)
    c: Coincident(g268,g269)
    c: Coincident(g269,g270)
    c: Coincident(g270,g271)
    c: Coincident(g271,g272)
    c: Coincident(g272,g273)
    c: Coincident(g273,g274)
    c: Coincident(g274,g275)
    c: Coincident(g275,g276)
    c: Coincident(g276,g277)
    c: Coincident(g277,g278)
    c: Coincident(g278,g279)
    c: Coincident(g279,g280)
    c: Coincident(g280,g281)
    c: Coincident(g281,g282)
    c: Coincident(g282,g266)
    c: Coincident(g283,g284)
    c: Coincident(g284,g285)
    c: Coincident(g285,g286)
    c: Coincident(g286,g287)
    c: Coincident(g287,g288)
    c: Coincident(g288,g289)
    c: Coincident(g289,g290)
    c: Coincident(g290,g291)
    c: Coincident(g291,g292)
    c: Coincident(g292,g293)
    c: Coincident(g293,g294)
    c: Coincident(g294,g295)
    c: Coincident(g295,g296)
    c: Coincident(g296,g283)
    c: Coincident(g297,g298)
    c: Coincident(g298,g299)
    c: Coincident(g299,g300)
    c: Coincident(g300,g301)
    c: Coincident(g301,g302)
    c: Coincident(g302,g303)
    c: Coincident(g303,g297)
    c: Coincident(g304,g305)
    c: Coincident(g305,g306)
    c: Coincident(g306,g307)
    c: Coincident(g307,g308)
    c: Coincident(g308,g309)
    c: Coincident(g309,g310)
    c: Coincident(g310,g311)
    c: Coincident(g311,g312)
    c: Coincident(g312,g313)
    c: Coincident(g313,g314)
    c: Coincident(g314,g315)
    c: Coincident(g315,g304)
    c: Coincident(g316,g317)
    c: Coincident(g317,g318)
    c: Coincident(g318,g319)
    c: Coincident(g319,g320)
    c: Coincident(g320,g321)
    c: Coincident(g321,g322)
    c: Coincident(g322,g323)
    c: Coincident(g323,g324)
    c: Coincident(g324,g325)
    c: Coincident(g325,g326)
    c: Coincident(g326,g316)
    c: Coincident(g327,g328)
    c: Coincident(g328,g329)
    c: Coincident(g329,g330)
    c: Coincident(g330,g331)
    c: Coincident(g331,g332)
    c: Coincident(g332,g333)
    c: Coincident(g333,g334)
    c: Coincident(g334,g335)
    c: Coincident(g335,g336)
    c: Coincident(g336,g327)
    c: Coincident(g337,g338)
    c: Coincident(g338,g339)
    c: Coincident(g339,g340)
    c: Coincident(g340,g341)
    c: Coincident(g341,g342)
    c: Coincident(g342,g337)
    c: Coincident(g343,g344)
    c: Coincident(g344,g345)
    c: Coincident(g345,g346)
    c: Coincident(g346,g347)
    c: Coincident(g347,g348)
    c: Coincident(g348,g343)
    c: Coincident(g349,g350)
    c: Coincident(g350,g351)
    c: Coincident(g351,g352)
    c: Coincident(g352,g353)
    c: Coincident(g353,g354)
    c: Coincident(g354,g355)
    c: Coincident(g355,g356)
    c: Coincident(g356,g357)
    c: Coincident(g357,g358)
    c: Coincident(g358,g359)
    c: Coincident(g359,g360)
    c: Coincident(g360,g361)
    c: Coincident(g361,g362)
    c: Coincident(g362,g363)
    c: Coincident(g363,g364)
    c: Coincident(g364,g365)
    c: Coincident(g365,g366)
    c: Coincident(g366,g367)
    c: Coincident(g367,g368)
    c: Coincident(g368,g349)
FEATURE [Sketcher::SketchObject] Sketch021  label="Sketch_MA"
  AttachmentOffset = pos=(0.5,-21,-84) rot=(0,0,1;-3.14159rad)
  FullyConstrained = false
  MapMode = 5
  Placement = pos=(-3.3,0.5,4.26e-14) rot=(0,0,1;4.71239rad)
  Support = -> [Pocket]
  sketch-geometry (775):
    g0: BSplineCurve PolesCount=4 KnotsCount=2 Degree=3 IsPeriodic=0
    g1: BSplineCurve PolesCount=4 KnotsCount=2 Degree=3 IsPeriodic=0
    g2: BSplineCurve PolesCount=2 KnotsCount=2 Degree=1 IsPeriodic=0
    g3: BSplineCurve PolesCount=4 KnotsCount=2 Degree=3 IsPeriodic=0
    g4: BSplineCurve PolesCount=2 KnotsCount=2 Degree=1 IsPeriodic=0
    g5: BSplineCurve PolesCount=2 KnotsCount=2 Degree=1 IsPeriodic=0
    g6: BSplineCurve PolesCount=2 KnotsCount=2 Degree=1 IsPeriodic=0
    g7: BSplineCurve PolesCount=4 KnotsCount=2 Degree=3 IsPeriodic=0
    g8: BSplineCurve PolesCount=2 KnotsCount=2 Degree=1 IsPeriodic=0
    g9: BSplineCurve PolesCount=4 KnotsCount=2 Degree=3 IsPeriodic=0
    g10: BSplineCurve PolesCount=4 KnotsCount=2 Degree=3 IsPeriodic=0
    g11: BSplineCurve PolesCount=4 KnotsCount=2 Degree=3 IsPeriodic=0
    g12: BSplineCurve PolesCount=4 KnotsCount=2 Degree=3 IsPeriodic=0
    g13: BSplineCurve PolesCount=4 KnotsCount=2 Degree=3 IsPeriodic=0
    g14: BSplineCurve PolesCount=4 KnotsCount=2 Degree=3 IsPeriodic=0
    g15: BSplineCurve PolesCount=4 KnotsCount=2 Degree=3 IsPeriodic=0
    g16: BSplineCurve PolesCount=4 KnotsCount=2 Degree=3 IsPeriodic=0
    g17: BSplineCurve PolesCount=4 KnotsCount=2 Degree=3 IsPeriodic=0
    g18: BSplineCurve PolesCount=4 KnotsCount=2 Degree=3 IsPeriodic=0
    g19: BSplineCurve PolesCount=4 KnotsCount=2 Degree=3 IsPeriodic=0
    g20: BSplineCurve PolesCount=4 KnotsCount=2 Degree=3 IsPeriodic=0
    g21: BSplineCurve PolesCount=4 KnotsCount=2 Degree=3 IsPeriodic=0
    g22: BSplineCurve PolesCount=4 KnotsCount=2 Degree=3 IsPeriodic=0
    g23: BSplineCurve PolesCount=4 KnotsCount=2 Degree=3 IsPeriodic=0
    g24: BSplineCurve PolesCount=2 KnotsCount=2 Degree=1 IsPeriodic=0
    g25: BSplineCurve PolesCount=2 KnotsCount=2 Degree=1 IsPeriodic=0
    g26: BSplineCurve PolesCount=2 KnotsCount=2 Degree=1 IsPeriodic=0
    g27: BSplineCurve PolesCount=2 KnotsCount=2 Degree=1 IsPeriodic=0
    g28: BSplineCurve PolesCount=2 KnotsCount=2 Degree=1 IsPeriodic=0
    g29: BSplineCurve PolesCount=2 KnotsCount=2 Degree=1 IsPeriodic=0
    g30: BSplineCurve PolesCount=2 KnotsCount=2 Degree=1 IsPeriodic=0
    g31: BSplineCurve PolesCount=2 KnotsCount=2 Degree=1 IsPeriodic=0
    g32: BSplineCurve PolesCount=2 KnotsCount=2 Degree=1 IsPeriodic=0
    g33: BSplineCurve PolesCount=2 KnotsCount=2 Degree=1 IsPeriodic=0
    g34: BSplineCurve PolesCount=2 KnotsCount=2 Degree=1 IsPeriodic=0
    g35: BSplineCurve PolesCount=2 KnotsCount=2 Degree=1 IsPeriodic=0
    g36: BSplineCurve PolesCount=2 KnotsCount=2 Degree=1 IsPeriodic=0
    g37: BSplineCurve PolesCount=2 KnotsCount=2 Degree=1 IsPeriodic=0
    g38: BSplineCurve PolesCount=2 KnotsCount=2 Degree=1 IsPeriodic=0
    g39: BSplineCurve PolesCount=2 KnotsCount=2 Degree=1 IsPeriodic=0
    g40: BSplineCurve PolesCount=2 KnotsCount=2 Degree=1 IsPeriodic=0
    g41: BSplineCurve PolesCount=2 KnotsCount=2 Degree=1 IsPeriodic=0
    g42: BSplineCurve PolesCount=2 KnotsCount=2 Degree=1 IsPeriodic=0
    g43: BSplineCurve PolesCount=2 KnotsCount=2 Degree=1 IsPeriodic=0
    g44: BSplineCurve PolesCount=2 KnotsCount=2 Degree=1 IsPeriodic=0
    g45: BSplineCurve PolesCount=2 KnotsCount=2 Degree=1 IsPeriodic=0
    g46: BSplineCurve PolesCount=2 KnotsCount=2 Degree=1 IsPeriodic=0
    g47: BSplineCurve PolesCount=2 KnotsCount=2 Degree=1 IsPeriodic=0
    g48: BSplineCurve PolesCount=2 KnotsCount=2 Degree=1 IsPeriodic=0
    g49: BSplineCurve PolesCount=2 KnotsCount=2 Degree=1 IsPeriodic=0
    g50: BSplineCurve PolesCount=2 KnotsCount=2 Degree=1 IsPeriodic=0
    g51: BSplineCurve PolesCount=2 KnotsCount=2 Degree=1 IsPeriodic=0
    g52: BSplineCurve PolesCount=2 KnotsCount=2 Degree=1 IsPeriodic=0
    g53: BSplineCurve PolesCount=2 KnotsCount=2 Degree=1 IsPeriodic=0
    g54: BSplineCurve PolesCount=2 KnotsCount=2 Degree=1 IsPeriodic=0
    g55: BSplineCurve PolesCount=2 KnotsCount=2 Degree=1 IsPeriodic=0
    g56: BSplineCurve PolesCount=2 KnotsCount=2 Degree=1 IsPeriodic=0
    g57: BSplineCurve PolesCount=2 KnotsCount=2 Degree=1 IsPeriodic=0
    g58: BSplineCurve PolesCount=2 KnotsCount=2 Degree=1 IsPeriodic=0
    g59: BSplineCurve PolesCount=2 KnotsCount=2 Degree=1 IsPeriodic=0
    g60: BSplineCurve PolesCount=2 KnotsCount=2 Degree=1 IsPeriodic=0
    g61: BSplineCurve PolesCount=4 KnotsCount=2 Degree=3 IsPeriodic=0
    g62: BSplineCurve PolesCount=2 KnotsCount=2 Degree=1 IsPeriodic=0
    g63: BSplineCurve PolesCount=2 KnotsCount=2 Degree=1 IsPeriodic=0
    g64: BSplineCurve PolesCount=2 KnotsCount=2 Degree=1 IsPeriodic=0
    g65: BSplineCurve PolesCount=4 KnotsCount=2 Degree=3 IsPeriodic=0
    g66: BSplineCurve PolesCount=2 KnotsCount=2 Degree=1 IsPeriodic=0
    g67: BSplineCurve PolesCount=2 KnotsCount=2 Degree=1 IsPeriodic=0
    g68: BSplineCurve PolesCount=4 KnotsCount=2 Degree=3 IsPeriodic=0
    g69: BSplineCurve PolesCount=4 KnotsCount=2 Degree=3 IsPeriodic=0
    g70: BSplineCurve PolesCount=2 KnotsCount=2 Degree=1 IsPeriodic=0
    g71: BSplineCurve PolesCount=2 KnotsCount=2 Degree=1 IsPeriodic=0
    g72: BSplineCurve PolesCount=2 KnotsCount=2 Degree=1 IsPeriodic=0
    g73: BSplineCurve PolesCount=2 KnotsCount=2 Degree=1 IsPeriodic=0
    g74: BSplineCurve PolesCount=2 KnotsCount=2 Degree=1 IsPeriodic=0
    g75: BSplineCurve PolesCount=2 KnotsCount=2 Degree=1 IsPeriodic=0
    g76: BSplineCurve PolesCount=2 KnotsCount=2 Degree=1 IsPeriodic=0
    g77: BSplineCurve PolesCount=2 KnotsCount=2 Degree=1 IsPeriodic=0
    g78: BSplineCurve PolesCount=2 KnotsCount=2 Degree=1 IsPeriodic=0
    g79: BSplineCurve PolesCount=2 KnotsCount=2 Degree=1 IsPeriodic=0
    g80: BSplineCurve PolesCount=4 KnotsCount=2 Degree=3 IsPeriodic=0
    g81: BSplineCurve PolesCount=4 KnotsCount=2 Degree=3 IsPeriodic=0
    g82: BSplineCurve PolesCount=4 KnotsCount=2 Degree=3 IsPeriodic=0
    g83: BSplineCurve PolesCount=4 KnotsCount=2 Degree=3 IsPeriodic=0
    g84: BSplineCurve PolesCount=4 KnotsCount=2 Degree=3 IsPeriodic=0
    g85: BSplineCurve PolesCount=4 KnotsCount=2 Degree=3 IsPeriodic=0
    g86: BSplineCurve PolesCount=2 KnotsCount=2 Degree=1 IsPeriodic=0
    g87: BSplineCurve PolesCount=4 KnotsCount=2 Degree=3 IsPeriodic=0
    g88: BSplineCurve PolesCount=4 KnotsCount=2 Degree=3 IsPeriodic=0
    g89: BSplineCurve PolesCount=4 KnotsCount=2 Degree=3 IsPeriodic=0
    g90: BSplineCurve PolesCount=4 KnotsCount=2 Degree=3 IsPeriodic=0
    g91: BSplineCurve PolesCount=4 KnotsCount=2 Degree=3 IsPeriodic=0
    g92: BSplineCurve PolesCount=4 KnotsCount=2 Degree=3 IsPeriodic=0
    g93: BSplineCurve PolesCount=2 KnotsCount=2 Degree=1 IsPeriodic=0
    g94: BSplineCurve PolesCount=2 KnotsCount=2 Degree=1 IsPeriodic=0
    g95: BSplineCurve PolesCount=2 KnotsCount=2 Degree=1 IsPeriodic=0
    g96: BSplineCurve PolesCount=2 KnotsCount=2 Degree=1 IsPeriodic=0
    g97: BSplineCurve PolesCount=2 KnotsCount=2 Degree=1 IsPeriodic=0
    g98: BSplineCurve PolesCount=2 KnotsCount=2 Degree=1 IsPeriodic=0
    g99: BSplineCurve PolesCount=2 KnotsCount=2 Degree=1 IsPeriodic=0
    g100: BSplineCurve PolesCount=2 KnotsCount=2 Degree=1 IsPeriodic=0
    g101: BSplineCurve PolesCount=2 KnotsCount=2 Degree=1 IsPeriodic=0
    g102: BSplineCurve PolesCount=2 KnotsCount=2 Degree=1 IsPeriodic=0
    g103: BSplineCurve PolesCount=2 KnotsCount=2 Degree=1 IsPeriodic=0
    g104: BSplineCurve PolesCount=2 KnotsCount=2 Degree=1 IsPeriodic=0
    g105: BSplineCurve PolesCount=2 KnotsCount=2 Degree=1 IsPeriodic=0
    g106: BSplineCurve PolesCount=4 KnotsCount=2 Degree=3 IsPeriodic=0
    g107: BSplineCurve PolesCount=4 KnotsCount=2 Degree=3 IsPeriodic=0
    g108: BSplineCurve PolesCount=4 KnotsCount=2 Degree=3 IsPeriodic=0
    g109: BSplineCurve PolesCount=4 KnotsCount=2 Degree=3 IsPeriodic=0
    g110: BSplineCurve PolesCount=4 KnotsCount=2 Degree=3 IsPeriodic=0
    g111: BSplineCurve PolesCount=4 KnotsCount=2 Degree=3 IsPeriodic=0
    g112: BSplineCurve PolesCount=2 KnotsCount=2 Degree=1 IsPeriodic=0
    g113: BSplineCurve PolesCount=4 KnotsCount=2 Degree=3 IsPeriodic=0
    g114: BSplineCurve PolesCount=4 KnotsCount=2 Degree=3 IsPeriodic=0
    g115: BSplineCurve PolesCount=4 KnotsCount=2 Degree=3 IsPeriodic=0
    g116: BSplineCurve PolesCount=4 KnotsCount=2 Degree=3 IsPeriodic=0
    g117: BSplineCurve PolesCount=4 KnotsCount=2 Degree=3 IsPeriodic=0
    g118: BSplineCurve PolesCount=4 KnotsCount=2 Degree=3 IsPeriodic=0
    g119: BSplineCurve PolesCount=2 KnotsCount=2 Degree=1 IsPeriodic=0
    g120: BSplineCurve PolesCount=2 KnotsCount=2 Degree=1 IsPeriodic=0
    g121: BSplineCurve PolesCount=2 KnotsCount=2 Degree=1 IsPeriodic=0
    g122: BSplineCurve PolesCount=2 KnotsCount=2 Degree=1 IsPeriodic=0
    g123: BSplineCurve PolesCount=2 KnotsCount=2 Degree=1 IsPeriodic=0
    g124: BSplineCurve PolesCount=2 KnotsCount=2 Degree=1 IsPeriodic=0
    g125: BSplineCurve PolesCount=2 KnotsCount=2 Degree=1 IsPeriodic=0
    g126: BSplineCurve PolesCount=2 KnotsCount=2 Degree=1 IsPeriodic=0
    g127: BSplineCurve PolesCount=2 KnotsCount=2 Degree=1 IsPeriodic=0
    g128: BSplineCurve PolesCount=2 KnotsCount=2 Degree=1 IsPeriodic=0
    g129: BSplineCurve PolesCount=2 KnotsCount=2 Degree=1 IsPeriodic=0
    g130: BSplineCurve PolesCount=2 KnotsCount=2 Degree=1 IsPeriodic=0
    g131: BSplineCurve PolesCount=2 KnotsCount=2 Degree=1 IsPeriodic=0
    g132: BSplineCurve PolesCount=2 KnotsCount=2 Degree=1 IsPeriodic=0
    g133: BSplineCurve PolesCount=2 KnotsCount=2 Degree=1 IsPeriodic=0
    g134: BSplineCurve PolesCount=2 KnotsCount=2 Degree=1 IsPeriodic=0
    g135: BSplineCurve PolesCount=2 KnotsCount=2 Degree=1 IsPeriodic=0
    g136: BSplineCurve PolesCount=2 KnotsCount=2 Degree=1 IsPeriodic=0
    g137: BSplineCurve PolesCount=4 KnotsCount=2 Degree=3 IsPeriodic=0
    g138: BSplineCurve PolesCount=4 KnotsCount=2 Degree=3 IsPeriodic=0
    g139: BSplineCurve PolesCount=2 KnotsCount=2 Degree=1 IsPeriodic=0
    g140: BSplineCurve PolesCount=2 KnotsCount=2 Degree=1 IsPeriodic=0
    g141: BSplineCurve PolesCount=2 KnotsCount=2 Degree=1 IsPeriodic=0
    g142: BSplineCurve PolesCount=4 KnotsCount=2 Degree=3 IsPeriodic=0
    g143: BSplineCurve PolesCount=4 KnotsCount=2 Degree=3 IsPeriodic=0
    g144: BSplineCurve PolesCount=2 KnotsCount=2 Degree=1 IsPeriodic=0
    g145: BSplineCurve PolesCount=2 KnotsCount=2 Degree=1 IsPeriodic=0
    g146: BSplineCurve PolesCount=2 KnotsCount=2 Degree=1 IsPeriodic=0
    g147: BSplineCurve PolesCount=2 KnotsCount=2 Degree=1 IsPeriodic=0
    g148: BSplineCurve PolesCount=2 KnotsCount=2 Degree=1 IsPeriodic=0
    g149: BSplineCurve PolesCount=2 KnotsCount=2 Degree=1 IsPeriodic=0
    g150: BSplineCurve PolesCount=2 KnotsCount=2 Degree=1 IsPeriodic=0
    g151: BSplineCurve PolesCount=2 KnotsCount=2 Degree=1 IsPeriodic=0
    g152: BSplineCurve PolesCount=2 KnotsCount=2 Degree=1 IsPeriodic=0
    g153: BSplineCurve PolesCount=2 KnotsCount=2 Degree=1 IsPeriodic=0
    g154: BSplineCurve PolesCount=2 KnotsCount=2 Degree=1 IsPeriodic=0
    g155: BSplineCurve PolesCount=2 KnotsCount=2 Degree=1 IsPeriodic=0
    g156: BSplineCurve PolesCount=2 KnotsCount=2 Degree=1 IsPeriodic=0
    g157: BSplineCurve PolesCount=2 KnotsCount=2 Degree=1 IsPeriodic=0
    g158: BSplineCurve PolesCount=2 KnotsCount=2 Degree=1 IsPeriodic=0
    g159: BSplineCurve PolesCount=2 KnotsCount=2 Degree=1 IsPeriodic=0
    g160: BSplineCurve PolesCount=2 KnotsCount=2 Degree=1 IsPeriodic=0
    g161: BSplineCurve PolesCount=2 KnotsCount=2 Degree=1 IsPeriodic=0
    g162: BSplineCurve PolesCount=2 KnotsCount=2 Degree=1 IsPeriodic=0
    g163: BSplineCurve PolesCount=2 KnotsCount=2 Degree=1 IsPeriodic=0
    g164: BSplineCurve PolesCount=2 KnotsCount=2 Degree=1 IsPeriodic=0
    g165: BSplineCurve PolesCount=2 KnotsCount=2 Degree=1 IsPeriodic=0
    g166: BSplineCurve PolesCount=2 KnotsCount=2 Degree=1 IsPeriodic=0
    g167: BSplineCurve PolesCount=2 KnotsCount=2 Degree=1 IsPeriodic=0
    g168: BSplineCurve PolesCount=2 KnotsCount=2 Degree=1 IsPeriodic=0
    g169: BSplineCurve PolesCount=2 KnotsCount=2 Degree=1 IsPeriodic=0
    g170: BSplineCurve PolesCount=2 KnotsCount=2 Degree=1 IsPeriodic=0
    g171: BSplineCurve PolesCount=2 KnotsCount=2 Degree=1 IsPeriodic=0
    g172: BSplineCurve PolesCount=2 KnotsCount=2 Degree=1 IsPeriodic=0
    g173: BSplineCurve PolesCount=2 KnotsCount=2 Degree=1 IsPeriodic=0
    g174: BSplineCurve PolesCount=2 KnotsCount=2 Degree=1 IsPeriodic=0
    g175: BSplineCurve PolesCount=2 KnotsCount=2 Degree=1 IsPeriodic=0
    g176: BSplineCurve PolesCount=2 KnotsCount=2 Degree=1 IsPeriodic=0
    g177: BSplineCurve PolesCount=2 KnotsCount=2 Degree=1 IsPeriodic=0
    g178: BSplineCurve PolesCount=2 KnotsCount=2 Degree=1 IsPeriodic=0
    g179: BSplineCurve PolesCount=2 KnotsCount=2 Degree=1 IsPeriodic=0
    g180: BSplineCurve PolesCount=2 KnotsCount=2 Degree=1 IsPeriodic=0
    g181: BSplineCurve PolesCount=2 KnotsCount=2 Degree=1 IsPeriodic=0
    g182: BSplineCurve PolesCount=2 KnotsCount=2 Degree=1 IsPeriodic=0
    g183: BSplineCurve PolesCount=4 KnotsCount=2 Degree=3 IsPeriodic=0
    g184: BSplineCurve PolesCount=4 KnotsCount=2 Degree=3 IsPeriodic=0
    g185: BSplineCurve PolesCount=2 KnotsCount=2 Degree=1 IsPeriodic=0
    g186: BSplineCurve PolesCount=2 KnotsCount=2 Degree=1 IsPeriodic=0
    g187: BSplineCurve PolesCount=4 KnotsCount=2 Degree=3 IsPeriodic=0
    g188: BSplineCurve PolesCount=2 KnotsCount=2 Degree=1 IsPeriodic=0
    g189: BSplineCurve PolesCount=4 KnotsCount=2 Degree=3 IsPeriodic=0
    g190: BSplineCurve PolesCount=4 KnotsCount=2 Degree=3 IsPeriodic=0
    g191: BSplineCurve PolesCount=4 KnotsCount=2 Degree=3 IsPeriodic=0
    g192: BSplineCurve PolesCount=4 KnotsCount=2 Degree=3 IsPeriodic=0
    g193: BSplineCurve PolesCount=4 KnotsCount=2 Degree=3 IsPeriodic=0
    g194: BSplineCurve PolesCount=2 KnotsCount=2 Degree=1 IsPeriodic=0
    g195: BSplineCurve PolesCount=4 KnotsCount=2 Degree=3 IsPeriodic=0
    g196: BSplineCurve PolesCount=4 KnotsCount=2 Degree=3 IsPeriodic=0
    g197: BSplineCurve PolesCount=4 KnotsCount=2 Degree=3 IsPeriodic=0
    g198: BSplineCurve PolesCount=4 KnotsCount=2 Degree=3 IsPeriodic=0
    g199: BSplineCurve PolesCount=2 KnotsCount=2 Degree=1 IsPeriodic=0
    g200: BSplineCurve PolesCount=4 KnotsCount=2 Degree=3 IsPeriodic=0
    g201: BSplineCurve PolesCount=4 KnotsCount=2 Degree=3 IsPeriodic=0
    g202: BSplineCurve PolesCount=4 KnotsCount=2 Degree=3 IsPeriodic=0
    g203: BSplineCurve PolesCount=4 KnotsCount=2 Degree=3 IsPeriodic=0
    g204: BSplineCurve PolesCount=2 KnotsCount=2 Degree=1 IsPeriodic=0
    g205: BSplineCurve PolesCount=4 KnotsCount=2 Degree=3 IsPeriodic=0
    g206: BSplineCurve PolesCount=4 KnotsCount=2 Degree=3 IsPeriodic=0
    g207: BSplineCurve PolesCount=4 KnotsCount=2 Degree=3 IsPeriodic=0
    g208: BSplineCurve PolesCount=4 KnotsCount=2 Degree=3 IsPeriodic=0
    g209: BSplineCurve PolesCount=2 KnotsCount=2 Degree=1 IsPeriodic=0
    g210: BSplineCurve PolesCount=4 KnotsCount=2 Degree=3 IsPeriodic=0
    g211: BSplineCurve PolesCount=4 KnotsCount=2 Degree=3 IsPeriodic=0
    g212: BSplineCurve PolesCount=4 KnotsCount=2 Degree=3 IsPeriodic=0
    g213: BSplineCurve PolesCount=4 KnotsCount=2 Degree=3 IsPeriodic=0
    g214: BSplineCurve PolesCount=2 KnotsCount=2 Degree=1 IsPeriodic=0
    g215: BSplineCurve PolesCount=4 KnotsCount=2 Degree=3 IsPeriodic=0
    g216: BSplineCurve PolesCount=4 KnotsCount=2 Degree=3 IsPeriodic=0
    g217: BSplineCurve PolesCount=4 KnotsCount=2 Degree=3 IsPeriodic=0
    g218: BSplineCurve PolesCount=4 KnotsCount=2 Degree=3 IsPeriodic=0
    g219: BSplineCurve PolesCount=2 KnotsCount=2 Degree=1 IsPeriodic=0
    g220: BSplineCurve PolesCount=4 KnotsCount=2 Degree=3 IsPeriodic=0
    g221: BSplineCurve PolesCount=4 KnotsCount=2 Degree=3 IsPeriodic=0
    g222: BSplineCurve PolesCount=4 KnotsCount=2 Degree=3 IsPeriodic=0
    g223: BSplineCurve PolesCount=4 KnotsCount=2 Degree=3 IsPeriodic=0
    g224: BSplineCurve PolesCount=2 KnotsCount=2 Degree=1 IsPeriodic=0
    g225: BSplineCurve PolesCount=4 KnotsCount=2 Degree=3 IsPeriodic=0
    g226: BSplineCurve PolesCount=2 KnotsCount=2 Degree=1 IsPeriodic=0
    g227: BSplineCurve PolesCount=4 KnotsCount=2 Degree=3 IsPeriodic=0
    g228: BSplineCurve PolesCount=2 KnotsCount=2 Degree=1 IsPeriodic=0
    g229: BSplineCurve PolesCount=4 KnotsCount=2 Degree=3 IsPeriodic=0
    g230: BSplineCurve PolesCount=2 KnotsCount=2 Degree=1 IsPeriodic=0
    g231: BSplineCurve PolesCount=2 KnotsCount=2 Degree=1 IsPeriodic=0
    g232: BSplineCurve PolesCount=4 KnotsCount=2 Degree=3 IsPeriodic=0
    g233: BSplineCurve PolesCount=4 KnotsCount=2 Degree=3 IsPeriodic=0
    g234: BSplineCurve PolesCount=4 KnotsCount=2 Degree=3 IsPeriodic=0
    g235: BSplineCurve PolesCount=4 KnotsCount=2 Degree=3 IsPeriodic=0
    g236: BSplineCurve PolesCount=2 KnotsCount=2 Degree=1 IsPeriodic=0
    g237: BSplineCurve PolesCount=4 KnotsCount=2 Degree=3 IsPeriodic=0
    g238: BSplineCurve PolesCount=4 KnotsCount=2 Degree=3 IsPeriodic=0
    g239: BSplineCurve PolesCount=4 KnotsCount=2 Degree=3 IsPeriodic=0
    g240: BSplineCurve PolesCount=4 KnotsCount=2 Degree=3 IsPeriodic=0
    g241: BSplineCurve PolesCount=2 KnotsCount=2 Degree=1 IsPeriodic=0
    g242: BSplineCurve PolesCount=4 KnotsCount=2 Degree=3 IsPeriodic=0
    g243: BSplineCurve PolesCount=4 KnotsCount=2 Degree=3 IsPeriodic=0
    g244: BSplineCurve PolesCount=4 KnotsCount=2 Degree=3 IsPeriodic=0
    g245: BSplineCurve PolesCount=4 KnotsCount=2 Degree=3 IsPeriodic=0
    g246: BSplineCurve PolesCount=2 KnotsCount=2 Degree=1 IsPeriodic=0
    g247: BSplineCurve PolesCount=4 KnotsCount=2 Degree=3 IsPeriodic=0
    g248: BSplineCurve PolesCount=4 KnotsCount=2 Degree=3 IsPeriodic=0
    g249: BSplineCurve PolesCount=4 KnotsCount=2 Degree=3 IsPeriodic=0
    g250: BSplineCurve PolesCount=4 KnotsCount=2 Degree=3 IsPeriodic=0
    g251: BSplineCurve PolesCount=2 KnotsCount=2 Degree=1 IsPeriodic=0
    g252: BSplineCurve PolesCount=4 KnotsCount=2 Degree=3 IsPeriodic=0
    g253: BSplineCurve PolesCount=4 KnotsCount=2 Degree=3 IsPeriodic=0
    g254: BSplineCurve PolesCount=4 KnotsCount=2 Degree=3 IsPeriodic=0
    g255: BSplineCurve PolesCount=4 KnotsCount=2 Degree=3 IsPeriodic=0
    g256: BSplineCurve PolesCount=2 KnotsCount=2 Degree=1 IsPeriodic=0
    g257: BSplineCurve PolesCount=4 KnotsCount=2 Degree=3 IsPeriodic=0
    g258: BSplineCurve PolesCount=2 KnotsCount=2 Degree=1 IsPeriodic=0
    g259: BSplineCurve PolesCount=4 KnotsCount=2 Degree=3 IsPeriodic=0
    g260: BSplineCurve PolesCount=4 KnotsCount=2 Degree=3 IsPeriodic=0
    g261: BSplineCurve PolesCount=2 KnotsCount=2 Degree=1 IsPeriodic=0
    g262: BSplineCurve PolesCount=4 KnotsCount=2 Degree=3 IsPeriodic=0
    g263: BSplineCurve PolesCount=4 KnotsCount=2 Degree=3 IsPeriodic=0
    g264: BSplineCurve PolesCount=4 KnotsCount=2 Degree=3 IsPeriodic=0
    g265: BSplineCurve PolesCount=2 KnotsCount=2 Degree=1 IsPeriodic=0
    g266: BSplineCurve PolesCount=2 KnotsCount=2 Degree=1 IsPeriodic=0
    g267: BSplineCurve PolesCount=2 KnotsCount=2 Degree=1 IsPeriodic=0
    g268: BSplineCurve PolesCount=4 KnotsCount=2 Degree=3 IsPeriodic=0
    g269: BSplineCurve PolesCount=2 KnotsCount=2 Degree=1 IsPeriodic=0
    g270: BSplineCurve PolesCount=4 KnotsCount=2 Degree=3 IsPeriodic=0
    g271: BSplineCurve PolesCount=4 KnotsCount=2 Degree=3 IsPeriodic=0
    g272: BSplineCurve PolesCount=4 KnotsCount=2 Degree=3 IsPeriodic=0
    g273: BSplineCurve PolesCount=4 KnotsCount=2 Degree=3 IsPeriodic=0
    g274: BSplineCurve PolesCount=2 KnotsCount=2 Degree=1 IsPeriodic=0
    g275: BSplineCurve PolesCount=2 KnotsCount=2 Degree=1 IsPeriodic=0
    g276: BSplineCurve PolesCount=4 KnotsCount=2 Degree=3 IsPeriodic=0
    g277: BSplineCurve PolesCount=2 KnotsCount=2 Degree=1 IsPeriodic=0
    g278: BSplineCurve PolesCount=4 KnotsCount=2 Degree=3 IsPeriodic=0
    g279: BSplineCurve PolesCount=2 KnotsCount=2 Degree=1 IsPeriodic=0
    g280: BSplineCurve PolesCount=2 KnotsCount=2 Degree=1 IsPeriodic=0
    g281: BSplineCurve PolesCount=4 KnotsCount=2 Degree=3 IsPeriodic=0
    g282: BSplineCurve PolesCount=4 KnotsCount=2 Degree=3 IsPeriodic=0
    g283: BSplineCurve PolesCount=4 KnotsCount=2 Degree=3 IsPeriodic=0
    g284: BSplineCurve PolesCount=4 KnotsCount=2 Degree=3 IsPeriodic=0
    g285: BSplineCurve PolesCount=2 KnotsCount=2 Degree=1 IsPeriodic=0
    g286: BSplineCurve PolesCount=4 KnotsCount=2 Degree=3 IsPeriodic=0
    g287: BSplineCurve PolesCount=2 KnotsCount=2 Degree=1 IsPeriodic=0
    g288: BSplineCurve PolesCount=4 KnotsCount=2 Degree=3 IsPeriodic=0
    g289: BSplineCurve PolesCount=4 KnotsCount=2 Degree=3 IsPeriodic=0
    g290: BSplineCurve PolesCount=2 KnotsCount=2 Degree=1 IsPeriodic=0
    g291: BSplineCurve PolesCount=4 KnotsCount=2 Degree=3 IsPeriodic=0
    g292: BSplineCurve PolesCount=4 KnotsCount=2 Degree=3 IsPeriodic=0
    g293: BSplineCurve PolesCount=4 KnotsCount=2 Degree=3 IsPeriodic=0
    g294: BSplineCurve PolesCount=2 KnotsCount=2 Degree=1 IsPeriodic=0
    g295: BSplineCurve PolesCount=2 KnotsCount=2 Degree=1 IsPeriodic=0
    g296: BSplineCurve PolesCount=2 KnotsCount=2 Degree=1 IsPeriodic=0
    g297: BSplineCurve PolesCount=4 KnotsCount=2 Degree=3 IsPeriodic=0
    g298: BSplineCurve PolesCount=2 KnotsCount=2 Degree=1 IsPeriodic=0
    g299: BSplineCurve PolesCount=4 KnotsCount=2 Degree=3 IsPeriodic=0
    g300: BSplineCurve PolesCount=4 KnotsCount=2 Degree=3 IsPeriodic=0
    g301: BSplineCurve PolesCount=4 KnotsCount=2 Degree=3 IsPeriodic=0
    g302: BSplineCurve PolesCount=4 KnotsCount=2 Degree=3 IsPeriodic=0
    g303: BSplineCurve PolesCount=4 KnotsCount=2 Degree=3 IsPeriodic=0
    g304: BSplineCurve PolesCount=2 KnotsCount=2 Degree=1 IsPeriodic=0
    g305: BSplineCurve PolesCount=4 KnotsCount=2 Degree=3 IsPeriodic=0
    g306: BSplineCurve PolesCount=4 KnotsCount=2 Degree=3 IsPeriodic=0
    g307: BSplineCurve PolesCount=4 KnotsCount=2 Degree=3 IsPeriodic=0
    g308: BSplineCurve PolesCount=4 KnotsCount=2 Degree=3 IsPeriodic=0
    g309: BSplineCurve PolesCount=2 KnotsCount=2 Degree=1 IsPeriodic=0
    g310: BSplineCurve PolesCount=4 KnotsCount=2 Degree=3 IsPeriodic=0
    g311: BSplineCurve PolesCount=4 KnotsCount=2 Degree=3 IsPeriodic=0
    g312: BSplineCurve PolesCount=4 KnotsCount=2 Degree=3 IsPeriodic=0
    g313: BSplineCurve PolesCount=4 KnotsCount=2 Degree=3 IsPeriodic=0
    g314: BSplineCurve PolesCount=2 KnotsCount=2 Degree=1 IsPeriodic=0
    g315: BSplineCurve PolesCount=4 KnotsCount=2 Degree=3 IsPeriodic=0
    g316: BSplineCurve PolesCount=4 KnotsCount=2 Degree=3 IsPeriodic=0
    g317: BSplineCurve PolesCount=2 KnotsCount=2 Degree=1 IsPeriodic=0
    g318: BSplineCurve PolesCount=4 KnotsCount=2 Degree=3 IsPeriodic=0
    g319: BSplineCurve PolesCount=2 KnotsCount=2 Degree=1 IsPeriodic=0
    g320: BSplineCurve PolesCount=4 KnotsCount=2 Degree=3 IsPeriodic=0
    g321: BSplineCurve PolesCount=2 KnotsCount=2 Degree=1 IsPeriodic=0
    g322: BSplineCurve PolesCount=4 KnotsCount=2 Degree=3 IsPeriodic=0
    g323: BSplineCurve PolesCount=2 KnotsCount=2 Degree=1 IsPeriodic=0
    g324: BSplineCurve PolesCount=4 KnotsCount=2 Degree=3 IsPeriodic=0
    g325: BSplineCurve PolesCount=2 KnotsCount=2 Degree=1 IsPeriodic=0
    g326: BSplineCurve PolesCount=2 KnotsCount=2 Degree=1 IsPeriodic=0
    g327: BSplineCurve PolesCount=2 KnotsCount=2 Degree=1 IsPeriodic=0
    g328: BSplineCurve PolesCount=2 KnotsCount=2 Degree=1 IsPeriodic=0
    g329: BSplineCurve PolesCount=2 KnotsCount=2 Degree=1 IsPeriodic=0
    g330: BSplineCurve PolesCount=2 KnotsCount=2 Degree=1 IsPeriodic=0
    g331: BSplineCurve PolesCount=2 KnotsCount=2 Degree=1 IsPeriodic=0
    g332: BSplineCurve PolesCount=2 KnotsCount=2 Degree=1 IsPeriodic=0
    g333: BSplineCurve PolesCount=2 KnotsCount=2 Degree=1 IsPeriodic=0
    g334: BSplineCurve PolesCount=2 KnotsCount=2 Degree=1 IsPeriodic=0
    g335: BSplineCurve PolesCount=2 KnotsCount=2 Degree=1 IsPeriodic=0
    g336: BSplineCurve PolesCount=2 KnotsCount=2 Degree=1 IsPeriodic=0
    g337: BSplineCurve PolesCount=2 KnotsCount=2 Degree=1 IsPeriodic=0
    g338: BSplineCurve PolesCount=2 KnotsCount=2 Degree=1 IsPeriodic=0
    g339: BSplineCurve PolesCount=2 KnotsCount=2 Degree=1 IsPeriodic=0
    g340: BSplineCurve PolesCount=2 KnotsCount=2 Degree=1 IsPeriodic=0
    g341: BSplineCurve PolesCount=2 KnotsCount=2 Degree=1 IsPeriodic=0
    g342: BSplineCurve PolesCount=2 KnotsCount=2 Degree=1 IsPeriodic=0
    g343: BSplineCurve PolesCount=2 KnotsCount=2 Degree=1 IsPeriodic=0
    g344: BSplineCurve PolesCount=2 KnotsCount=2 Degree=1 IsPeriodic=0
    g345: BSplineCurve PolesCount=2 KnotsCount=2 Degree=1 IsPeriodic=0
    g346: BSplineCurve PolesCount=2 KnotsCount=2 Degree=1 IsPeriodic=0
    g347: BSplineCurve PolesCount=2 KnotsCount=2 Degree=1 IsPeriodic=0
    g348: BSplineCurve PolesCount=2 KnotsCount=2 Degree=1 IsPeriodic=0
    g349: BSplineCurve PolesCount=2 KnotsCount=2 Degree=1 IsPeriodic=0
    g350: BSplineCurve PolesCount=2 KnotsCount=2 Degree=1 IsPeriodic=0
    g351: BSplineCurve PolesCount=2 KnotsCount=2 Degree=1 IsPeriodic=0
    g352: BSplineCurve PolesCount=2 KnotsCount=2 Degree=1 IsPeriodic=0
    g353: BSplineCurve PolesCount=2 KnotsCount=2 Degree=1 IsPeriodic=0
    g354: BSplineCurve PolesCount=2 KnotsCount=2 Degree=1 IsPeriodic=0
    g355: BSplineCurve PolesCount=2 KnotsCount=2 Degree=1 IsPeriodic=0
    g356: BSplineCurve PolesCount=2 KnotsCount=2 Degree=1 IsPeriodic=0
    g357: BSplineCurve PolesCount=2 KnotsCount=2 Degree=1 IsPeriodic=0
    g358: BSplineCurve PolesCount=2 KnotsCount=2 Degree=1 IsPeriodic=0
    g359: BSplineCurve PolesCount=2 KnotsCount=2 Degree=1 IsPeriodic=0
    g360: BSplineCurve PolesCount=2 KnotsCount=2 Degree=1 IsPeriodic=0
    g361: BSplineCurve PolesCount=2 KnotsCount=2 Degree=1 IsPeriodic=0
    g362: BSplineCurve PolesCount=2 KnotsCount=2 Degree=1 IsPeriodic=0
    g363: BSplineCurve PolesCount=2 KnotsCount=2 Degree=1 IsPeriodic=0
    g364: BSplineCurve PolesCount=2 KnotsCount=2 Degree=1 IsPeriodic=0
    g365: BSplineCurve PolesCount=2 KnotsCount=2 Degree=1 IsPeriodic=0
    g366: BSplineCurve PolesCount=2 KnotsCount=2 Degree=1 IsPeriodic=0
    g367: BSplineCurve PolesCount=2 KnotsCount=2 Degree=1 IsPeriodic=0
    g368: BSplineCurve PolesCount=2 KnotsCount=2 Degree=1 IsPeriodic=0
    g369: BSplineCurve PolesCount=2 KnotsCount=2 Degree=1 IsPeriodic=0
    g370: BSplineCurve PolesCount=2 KnotsCount=2 Degree=1 IsPeriodic=0
    g371: BSplineCurve PolesCount=2 KnotsCount=2 Degree=1 IsPeriodic=0
    g372: BSplineCurve PolesCount=2 KnotsCount=2 Degree=1 IsPeriodic=0
    g373: BSplineCurve PolesCount=2 KnotsCount=2 Degree=1 IsPeriodic=0
    g374: BSplineCurve PolesCount=2 KnotsCount=2 Degree=1 IsPeriodic=0
    g375: BSplineCurve PolesCount=2 KnotsCount=2 Degree=1 IsPeriodic=0
    g376: BSplineCurve PolesCount=2 KnotsCount=2 Degree=1 IsPeriodic=0
    g377: BSplineCurve PolesCount=2 KnotsCount=2 Degree=1 IsPeriodic=0
    g378: BSplineCurve PolesCount=2 KnotsCount=2 Degree=1 IsPeriodic=0
    g379: BSplineCurve PolesCount=2 KnotsCount=2 Degree=1 IsPeriodic=0
    g380: BSplineCurve PolesCount=2 KnotsCount=2 Degree=1 IsPeriodic=0
    g381: BSplineCurve PolesCount=2 KnotsCount=2 Degree=1 IsPeriodic=0
    g382: BSplineCurve PolesCount=2 KnotsCount=2 Degree=1 IsPeriodic=0
    g383: BSplineCurve PolesCount=2 KnotsCount=2 Degree=1 IsPeriodic=0
    g384: BSplineCurve PolesCount=2 KnotsCount=2 Degree=1 IsPeriodic=0
    g385: BSplineCurve PolesCount=2 KnotsCount=2 Degree=1 IsPeriodic=0
    g386: BSplineCurve PolesCount=2 KnotsCount=2 Degree=1 IsPeriodic=0
    g387: BSplineCurve PolesCount=4 KnotsCount=2 Degree=3 IsPeriodic=0
    g388: BSplineCurve PolesCount=4 KnotsCount=2 Degree=3 IsPeriodic=0
    g389: BSplineCurve PolesCount=2 KnotsCount=2 Degree=1 IsPeriodic=0
    g390: BSplineCurve PolesCount=2 KnotsCount=2 Degree=1 IsPeriodic=0
    g391: BSplineCurve PolesCount=2 KnotsCount=2 Degree=1 IsPeriodic=0
    g392: BSplineCurve PolesCount=2 KnotsCount=2 Degree=1 IsPeriodic=0
    g393: BSplineCurve PolesCount=4 KnotsCount=2 Degree=3 IsPeriodic=0
    g394: BSplineCurve PolesCount=2 KnotsCount=2 Degree=1 IsPeriodic=0
    g395: BSplineCurve PolesCount=2 KnotsCount=2 Degree=1 IsPeriodic=0
    g396: BSplineCurve PolesCount=2 KnotsCount=2 Degree=1 IsPeriodic=0
    g397: BSplineCurve PolesCount=2 KnotsCount=2 Degree=1 IsPeriodic=0
    g398: BSplineCurve PolesCount=2 KnotsCount=2 Degree=1 IsPeriodic=0
    g399: BSplineCurve PolesCount=2 KnotsCount=2 Degree=1 IsPeriodic=0
    ... +375 more geometry lines
  constraints (775):
    c: Coincident(g0,g1)
    c: Coincident(g1,g2)
    c: Coincident(g2,g3)
    c: Coincident(g3,g4)
    c: Coincident(g4,g5)
    c: Coincident(g5,g6)
    c: Coincident(g6,g7)
    c: Coincident(g7,g8)
    c: Coincident(g8,g9)
    c: Coincident(g9,g10)
    c: Coincident(g10,g11)
    c: Coincident(g11,g12)
    c: Coincident(g12,g13)
    c: Coincident(g13,g14)
    c: Coincident(g14,g15)
    c: Coincident(g15,g16)
    c: Coincident(g16,g17)
    c: Coincident(g17,g18)
    c: Coincident(g18,g19)
    c: Coincident(g19,g20)
    c: Coincident(g20,g21)
    c: Coincident(g21,g22)
    c: Coincident(g22,g23)
    c: Coincident(g23,g0)
    c: Coincident(g24,g25)
    c: Coincident(g25,g26)
    c: Coincident(g26,g27)
    c: Coincident(g27,g24)
    c: Coincident(g28,g29)
    c: Coincident(g29,g30)
    c: Coincident(g30,g31)
    c: Coincident(g31,g32)
    c: Coincident(g32,g33)
    c: Coincident(g33,g34)
    c: Coincident(g34,g35)
    c: Coincident(g35,g28)
    c: Coincident(g36,g37)
    c: Coincident(g37,g38)
    c: Coincident(g38,g39)
    c: Coincident(g39,g40)
    c: Coincident(g40,g41)
    c: Coincident(g41,g42)
    c: Coincident(g42,g43)
    c: Coincident(g43,g44)
    c: Coincident(g44,g45)
    c: Coincident(g45,g46)
    c: Coincident(g46,g47)
    c: Coincident(g47,g48)
    c: Coincident(g48,g36)
    c: Coincident(g49,g50)
    c: Coincident(g50,g51)
    c: Coincident(g51,g52)
    c: Coincident(g52,g53)
    c: Coincident(g53,g54)
    c: Coincident(g54,g55)
    c: Coincident(g55,g56)
    c: Coincident(g56,g57)
    c: Coincident(g57,g58)
    c: Coincident(g58,g59)
    c: Coincident(g59,g60)
    c: Coincident(g60,g49)
    c: Coincident(g61,g62)
    c: Coincident(g62,g63)
    c: Coincident(g63,g64)
    c: Coincident(g64,g65)
    c: Coincident(g65,g61)
    c: Coincident(g66,g67)
    c: Coincident(g67,g68)
    c: Coincident(g68,g69)
    c: Coincident(g69,g70)
    c: Coincident(g70,g71)
    c: Coincident(g71,g72)
    c: Coincident(g72,g73)
    c: Coincident(g73,g74)
    c: Coincident(g74,g75)
    c: Coincident(g75,g66)
    c: Coincident(g76,g77)
    c: Coincident(g77,g78)
    c: Coincident(g78,g79)
    c: Coincident(g79,g76)
    c: Coincident(g80,g81)
    c: Coincident(g81,g82)
    c: Coincident(g82,g83)
    c: Coincident(g83,g84)
    c: Coincident(g84,g85)
    c: Coincident(g85,g86)
    c: Coincident(g86,g87)
    c: Coincident(g87,g88)
    c: Coincident(g88,g89)
    c: Coincident(g89,g90)
    c: Coincident(g90,g91)
    c: Coincident(g91,g92)
    c: Coincident(g92,g93)
    c: Coincident(g93,g80)
    c: Coincident(g94,g95)
    c: Coincident(g95,g96)
    c: Coincident(g96,g97)
    c: Coincident(g97,g94)
    c: Coincident(g98,g99)
    c: Coincident(g99,g100)
    c: Coincident(g100,g101)
    c: Coincident(g101,g102)
    c: Coincident(g102,g103)
    c: Coincident(g103,g104)
    c: Coincident(g104,g105)
    c: Coincident(g105,g98)
    c: Coincident(g106,g107)
    c: Coincident(g107,g108)
    c: Coincident(g108,g109)
    c: Coincident(g109,g110)
    c: Coincident(g110,g111)
    c: Coincident(g111,g112)
    c: Coincident(g112,g113)
    c: Coincident(g113,g114)
    c: Coincident(g114,g115)
    c: Coincident(g115,g116)
    c: Coincident(g116,g117)
    c: Coincident(g117,g118)
    c: Coincident(g118,g119)
    c: Coincident(g119,g106)
    c: Coincident(g120,g121)
    c: Coincident(g121,g122)
    c: Coincident(g122,g123)
    c: Coincident(g123,g124)
    c: Coincident(g124,g125)
    c: Coincident(g125,g126)
    c: Coincident(g126,g127)
    c: Coincident(g127,g128)
    c: Coincident(g128,g120)
    c: Coincident(g129,g130)
    c: Coincident(g130,g131)
    c: Coincident(g131,g132)
    c: Coincident(g132,g133)
    c: Coincident(g133,g134)
    c: Coincident(g134,g129)
    c: Coincident(g135,g136)
    c: Coincident(g136,g137)
    c: Coincident(g137,g138)
    c: Coincident(g138,g139)
    c: Coincident(g139,g140)
    c: Coincident(g140,g141)
    c: Coincident(g141,g142)
    c: Coincident(g142,g143)
    c: Coincident(g143,g144)
    c: Coincident(g144,g145)
    c: Coincident(g145,g135)
    c: Coincident(g146,g147)
    c: Coincident(g147,g148)
    c: Coincident(g148,g149)
    c: Coincident(g149,g150)
    c: Coincident(g150,g151)
    c: Coincident(g151,g152)
    c: Coincident(g152,g153)
    c: Coincident(g153,g154)
    c: Coincident(g154,g155)
    c: Coincident(g155,g156)
    c: Coincident(g156,g157)
    c: Coincident(g157,g158)
    c: Coincident(g158,g159)
    c: Coincident(g159,g160)
    c: Coincident(g160,g146)
    c: Coincident(g161,g162)
    c: Coincident(g162,g163)
    c: Coincident(g163,g164)
    c: Coincident(g164,g165)
    c: Coincident(g165,g166)
    c: Coincident(g166,g167)
    c: Coincident(g167,g168)
    c: Coincident(g168,g169)
    c: Coincident(g169,g170)
    c: Coincident(g170,g171)
    c: Coincident(g171,g172)
    c: Coincident(g172,g173)
    c: Coincident(g173,g161)
    c: Coincident(g174,g175)
    c: Coincident(g175,g176)
    c: Coincident(g176,g177)
    c: Coincident(g177,g178)
    c: Coincident(g178,g179)
    c: Coincident(g179,g180)
    c: Coincident(g180,g181)
    c: Coincident(g181,g174)
    c: Coincident(g182,g183)
    c: Coincident(g183,g184)
    c: Coincident(g184,g185)
    c: Coincident(g185,g186)
    c: Coincident(g186,g187)
    c: Coincident(g187,g188)
    c: Coincident(g188,g189)
    c: Coincident(g189,g190)
    c: Coincident(g190,g191)
    c: Coincident(g191,g192)
    c: Coincident(g192,g193)
    c: Coincident(g193,g194)
    c: Coincident(g194,g195)
    c: Coincident(g195,g196)
    c: Coincident(g196,g197)
    c: Coincident(g197,g198)
    c: Coincident(g198,g199)
    c: Coincident(g199,g200)
    c: Coincident(g200,g201)
    c: Coincident(g201,g202)
    c: Coincident(g202,g203)
    c: Coincident(g203,g204)
    c: Coincident(g204,g205)
    c: Coincident(g205,g206)
    c: Coincident(g206,g207)
    c: Coincident(g207,g208)
    c: Coincident(g208,g209)
    c: Coincident(g209,g210)
    c: Coincident(g210,g211)
    c: Coincident(g211,g212)
    c: Coincident(g212,g213)
    c: Coincident(g213,g214)
    c: Coincident(g214,g215)
    c: Coincident(g215,g216)
    c: Coincident(g216,g217)
    c: Coincident(g217,g218)
    c: Coincident(g218,g219)
    c: Coincident(g219,g220)
    c: Coincident(g220,g221)
    c: Coincident(g221,g222)
    c: Coincident(g222,g223)
    c: Coincident(g223,g224)
    c: Coincident(g224,g225)
    c: Coincident(g225,g226)
    c: Coincident(g226,g227)
    c: Coincident(g227,g228)
    c: Coincident(g228,g229)
    c: Coincident(g229,g230)
    c: Coincident(g230,g231)
    c: Coincident(g231,g232)
    c: Coincident(g232,g233)
    c: Coincident(g233,g234)
    c: Coincident(g234,g235)
    c: Coincident(g235,g236)
    c: Coincident(g236,g237)
    c: Coincident(g237,g238)
    c: Coincident(g238,g239)
    c: Coincident(g239,g240)
    c: Coincident(g240,g241)
    c: Coincident(g241,g242)
    c: Coincident(g242,g243)
    c: Coincident(g243,g244)
    c: Coincident(g244,g245)
    c: Coincident(g245,g246)
    c: Coincident(g246,g247)
    c: Coincident(g247,g248)
    c: Coincident(g248,g249)
    c: Coincident(g249,g250)
    c: Coincident(g250,g251)
    c: Coincident(g251,g252)
    c: Coincident(g252,g253)
    c: Coincident(g253,g254)
    c: Coincident(g254,g255)
    c: Coincident(g255,g256)
    c: Coincident(g256,g257)
    c: Coincident(g257,g258)
    c: Coincident(g258,g259)
    c: Coincident(g259,g260)
    c: Coincident(g260,g261)
    c: Coincident(g261,g262)
    c: Coincident(g262,g263)
    c: Coincident(g263,g264)
    c: Coincident(g264,g265)
    c: Coincident(g265,g266)
    c: Coincident(g266,g267)
    c: Coincident(g267,g268)
    c: Coincident(g268,g269)
    c: Coincident(g269,g270)
    c: Coincident(g270,g271)
    c: Coincident(g271,g272)
    c: Coincident(g272,g273)
    c: Coincident(g273,g274)
    c: Coincident(g274,g275)
    c: Coincident(g275,g276)
    c: Coincident(g276,g277)
    c: Coincident(g277,g278)
    c: Coincident(g278,g279)
    c: Coincident(g279,g280)
    c: Coincident(g280,g281)
    c: Coincident(g281,g282)
    c: Coincident(g282,g283)
    c: Coincident(g283,g284)
    c: Coincident(g284,g285)
    c: Coincident(g285,g286)
    c: Coincident(g286,g287)
    c: Coincident(g287,g288)
    c: Coincident(g288,g289)
    c: Coincident(g289,g290)
    c: Coincident(g290,g291)
    c: Coincident(g291,g292)
    c: Coincident(g292,g293)
    c: Coincident(g293,g294)
    c: Coincident(g294,g295)
    c: Coincident(g295,g296)
    c: Coincident(g296,g297)
    c: Coincident(g297,g298)
    c: Coincident(g298,g299)
    c: Coincident(g299,g300)
    c: Coincident(g300,g301)
    c: Coincident(g301,g302)
    c: Coincident(g302,g303)
    c: Coincident(g303,g304)
    c: Coincident(g304,g305)
    c: Coincident(g305,g306)
    c: Coincident(g306,g307)
    c: Coincident(g307,g308)
    c: Coincident(g308,g309)
    c: Coincident(g309,g310)
    c: Coincident(g310,g311)
    c: Coincident(g311,g312)
    c: Coincident(g312,g313)
    c: Coincident(g313,g314)
    c: Coincident(g314,g315)
    c: Coincident(g315,g316)
    c: Coincident(g316,g317)
    c: Coincident(g317,g318)
    c: Coincident(g318,g182)
    c: Coincident(g319,g320)
    c: Coincident(g320,g321)
    c: Coincident(g321,g322)
    c: Coincident(g322,g323)
    c: Coincident(g323,g324)
    c: Coincident(g324,g319)
    c: Coincident(g325,g326)
    c: Coincident(g326,g327)
    c: Coincident(g327,g328)
    c: Coincident(g328,g329)
    c: Coincident(g329,g330)
    c: Coincident(g330,g331)
    c: Coincident(g331,g332)
    c: Coincident(g332,g333)
    c: Coincident(g333,g334)
    c: Coincident(g334,g335)
    c: Coincident(g335,g336)
    c: Coincident(g336,g337)
    c: Coincident(g337,g338)
    c: Coincident(g338,g339)
    c: Coincident(g339,g340)
    c: Coincident(g340,g341)
    c: Coincident(g341,g342)
    c: Coincident(g342,g343)
    c: Coincident(g343,g344)
    c: Coincident(g344,g345)
    c: Coincident(g345,g346)
    c: Coincident(g346,g347)
    c: Coincident(g347,g348)
    c: Coincident(g348,g349)
    c: Coincident(g349,g350)
    c: Coincident(g350,g351)
    c: Coincident(g351,g352)
    c: Coincident(g352,g353)
    c: Coincident(g353,g354)
    c: Coincident(g354,g355)
    c: Coincident(g355,g356)
    c: Coincident(g356,g357)
    c: Coincident(g357,g358)
    c: Coincident(g358,g359)
    c: Coincident(g359,g360)
    c: Coincident(g360,g361)
    c: Coincident(g361,g362)
    c: Coincident(g362,g363)
    c: Coincident(g363,g364)
    c: Coincident(g364,g365)
    c: Coincident(g365,g366)
    c: Coincident(g366,g367)
    c: Coincident(g367,g368)
    c: Coincident(g368,g369)
    c: Coincident(g369,g370)
    c: Coincident(g370,g371)
    c: Coincident(g371,g372)
    c: Coincident(g372,g373)
    c: Coincident(g373,g374)
    c: Coincident(g374,g375)
    c: Coincident(g375,g376)
    c: Coincident(g376,g377)
    c: Coincident(g377,g378)
    c: Coincident(g378,g379)
    c: Coincident(g379,g380)
    c: Coincident(g380,g381)
    c: Coincident(g381,g382)
    c: Coincident(g382,g383)
    c: Coincident(g383,g384)
    c: Coincident(g384,g385)
    c: Coincident(g385,g386)
    c: Coincident(g386,g387)
    c: Coincident(g387,g388)
    c: Coincident(g388,g325)
    c: Coincident(g389,g390)
    c: Coincident(g390,g391)
    c: Coincident(g391,g392)
    c: Coincident(g392,g393)
    c: Coincident(g393,g394)
    c: Coincident(g394,g395)
    c: Coincident(g395,g396)
    c: Coincident(g396,g397)
    c: Coincident(g397,g398)
    c: Coincident(g398,g399)
    c: Coincident(g399,g400)
    c: Coincident(g400,g401)
    c: Coincident(g401,g402)
    c: Coincident(g402,g403)
    c: Coincident(g403,g404)
    c: Coincident(g404,g405)
    c: Coincident(g405,g406)
    c: Coincident(g406,g407)
    c: Coincident(g407,g408)
    c: Coincident(g408,g409)
    c: Coincident(g409,g410)
    c: Coincident(g410,g411)
    c: Coincident(g411,g412)
    c: Coincident(g412,g413)
    c: Coincident(g413,g414)
    c: Coincident(g414,g415)
    c: Coincident(g415,g416)
    c: Coincident(g416,g417)
    c: Coincident(g417,g418)
    c: Coincident(g418,g419)
    c: Coincident(g419,g420)
    c: Coincident(g420,g421)
    c: Coincident(g421,g422)
    c: Coincident(g422,g423)
    c: Coincident(g423,g424)
    c: Coincident(g424,g425)
    c: Coincident(g425,g426)
    c: Coincident(g426,g427)
    c: Coincident(g427,g428)
    c: Coincident(g428,g429)
    c: Coincident(g429,g430)
    c: Coincident(g430,g431)
    c: Coincident(g431,g432)
    c: Coincident(g432,g433)
    c: Coincident(g433,g434)
    c: Coincident(g434,g435)
    c: Coincident(g435,g436)
    c: Coincident(g436,g437)
    c: Coincident(g437,g438)
    c: Coincident(g438,g439)
    c: Coincident(g439,g440)
    c: Coincident(g440,g441)
    c: Coincident(g441,g442)
    c: Coincident(g442,g443)
    c: Coincident(g443,g444)
    c: Coincident(g444,g389)
    c: Coincident(g445,g446)
    c: Coincident(g446,g447)
    c: Coincident(g447,g448)
    c: Coincident(g448,g449)
    c: Coincident(g449,g450)
    c: Coincident(g450,g451)
    c: Coincident(g451,g452)
    c: Coincident(g452,g453)
    c: Coincident(g453,g454)
    c: Coincident(g454,g455)
    c: Coincident(g455,g456)
    c: Coincident(g456,g457)
    c: Coincident(g457,g458)
    c: Coincident(g458,g459)
    c: Coincident(g459,g460)
    c: Coincident(g460,g461)
    c: Coincident(g461,g462)
    c: Coincident(g462,g463)
    c: Coincident(g463,g464)
    c: Coincident(g464,g465)
    c: Coincident(g465,g466)
    c: Coincident(g466,g467)
    c: Coincident(g467,g468)
    c: Coincident(g468,g469)
    c: Coincident(g469,g470)
    c: Coincident(g470,g471)
    c: Coincident(g471,g472)
    c: Coincident(g472,g473)
    c: Coincident(g473,g474)
    c: Coincident(g474,g475)
    c: Coincident(g475,g476)
    c: Coincident(g476,g477)
    c: Coincident(g477,g478)
    c: Coincident(g478,g479)
    c: Coincident(g479,g480)
    c: Coincident(g480,g481)
    c: Coincident(g481,g482)
    c: Coincident(g482,g483)
    c: Coincident(g483,g484)
    c: Coincident(g484,g485)
    c: Coincident(g485,g486)
    c: Coincident(g486,g487)
    c: Coincident(g487,g488)
    c: Coincident(g488,g445)
    c: Coincident(g489,g490)
    c: Coincident(g490,g491)
    c: Coincident(g491,g492)
    c: Coincident(g492,g493)
    c: Coincident(g493,g494)
    c: Coincident(g494,g495)
    c: Coincident(g495,g496)
    c: Coincident(g496,g489)
    c: Coincident(g497,g498)
    c: Coincident(g498,g499)
    c: Coincident(g499,g500)
    c: Coincident(g500,g501)
    c: Coincident(g501,g502)
    c: Coincident(g502,g503)
    c: Coincident(g503,g504)
    c: Coincident(g504,g505)
    c: Coincident(g505,g506)
    c: Coincident(g506,g507)
    c: Coincident(g507,g508)
    c: Coincident(g508,g509)
    c: Coincident(g509,g510)
    c: Coincident(g510,g511)
    c: Coincident(g511,g512)
    c: Coincident(g512,g513)
    c: Coincident(g513,g514)
    c: Coincident(g514,g515)
    c: Coincident(g515,g516)
    c: Coincident(g516,g517)
    c: Coincident(g517,g497)
    c: Coincident(g518,g519)
    c: Coincident(g519,g520)
    c: Coincident(g520,g521)
    c: Coincident(g521,g522)
    c: Coincident(g522,g523)
    c: Coincident(g523,g524)
    c: Coincident(g524,g525)
    c: Coincident(g525,g526)
    c: Coincident(g526,g527)
    c: Coincident(g527,g528)
    c: Coincident(g528,g529)
    c: Coincident(g529,g530)
    c: Coincident(g530,g518)
    c: Coincident(g531,g532)
    c: Coincident(g532,g533)
    c: Coincident(g533,g534)
    c: Coincident(g534,g535)
    c: Coincident(g535,g536)
    c: Coincident(g536,g537)
    c: Coincident(g537,g538)
    c: Coincident(g538,g539)
    c: Coincident(g539,g540)
    c: Coincident(g540,g541)
    c: Coincident(g541,g542)
    c: Coincident(g542,g543)
    c: Coincident(g543,g544)
    c: Coincident(g544,g545)
    c: Coincident(g545,g546)
    c: Coincident(g546,g547)
    c: Coincident(g547,g548)
    c: Coincident(g548,g549)
    c: Coincident(g549,g550)
    c: Coincident(g550,g551)
    c: Coincident(g551,g552)
    c: Coincident(g552,g553)
    c: Coincident(g553,g554)
    c: Coincident(g554,g555)
    c: Coincident(g555,g556)
    c: Coincident(g556,g557)
    c: Coincident(g557,g558)
    c: Coincident(g558,g559)
    c: Coincident(g559,g560)
    c: Coincident(g560,g561)
    c: Coincident(g561,g562)
    c: Coincident(g562,g563)
    c: Coincident(g563,g564)
    c: Coincident(g564,g565)
    c: Coincident(g565,g566)
    c: Coincident(g566,g567)
    c: Coincident(g567,g568)
    c: Coincident(g568,g569)
    c: Coincident(g569,g570)
    c: Coincident(g570,g571)
    c: Coincident(g571,g572)
    c: Coincident(g572,g573)
    c: Coincident(g573,g574)
    c: Coincident(g574,g575)
    c: Coincident(g575,g576)
    c: Coincident(g576,g577)
    c: Coincident(g577,g578)
    c: Coincident(g578,g579)
    c: Coincident(g579,g580)
    c: Coincident(g580,g581)
    c: Coincident(g581,g582)
    c: Coincident(g582,g583)
    c: Coincident(g583,g584)
    c: Coincident(g584,g585)
    c: Coincident(g585,g586)
    c: Coincident(g586,g587)
    c: Coincident(g587,g588)
    c: Coincident(g588,g589)
    c: Coincident(g589,g590)
    c: Coincident(g590,g591)
    c: Coincident(g591,g592)
    c: Coincident(g592,g593)
    c: Coincident(g593,g594)
    c: Coincident(g594,g595)
    c: Coincident(g595,g596)
    c: Coincident(g596,g597)
    c: Coincident(g597,g598)
    c: Coincident(g598,g599)
    c: Coincident(g599,g600)
    c: Coincident(g600,g601)
    c: Coincident(g601,g602)
    c: Coincident(g602,g603)
    c: Coincident(g603,g604)
    c: Coincident(g604,g605)
    c: Coincident(g605,g606)
    c: Coincident(g606,g607)
    c: Coincident(g607,g608)
    c: Coincident(g608,g609)
    c: Coincident(g609,g610)
    c: Coincident(g610,g611)
    c: Coincident(g611,g612)
    c: Coincident(g612,g613)
    c: Coincident(g613,g614)
    c: Coincident(g614,g615)
    c: Coincident(g615,g616)
    c: Coincident(g616,g617)
    c: Coincident(g617,g618)
    c: Coincident(g618,g619)
    c: Coincident(g619,g620)
    c: Coincident(g620,g621)
    c: Coincident(g621,g622)
    c: Coincident(g622,g623)
    c: Coincident(g623,g624)
    c: Coincident(g624,g625)
    c: Coincident(g625,g626)
    c: Coincident(g626,g627)
    c: Coincident(g627,g628)
    c: Coincident(g628,g629)
    c: Coincident(g629,g630)
    c: Coincident(g630,g631)
    c: Coincident(g631,g632)
    c: Coincident(g632,g633)
    c: Coincident(g633,g634)
    c: Coincident(g634,g635)
    c: Coincident(g635,g636)
    c: Coincident(g636,g637)
    c: Coincident(g637,g638)
    c: Coincident(g638,g639)
    c: Coincident(g639,g640)
    c: Coincident(g640,g641)
    c: Coincident(g641,g642)
    c: Coincident(g642,g643)
    c: Coincident(g643,g644)
    c: Coincident(g644,g645)
    c: Coincident(g645,g646)
    c: Coincident(g646,g647)
    c: Coincident(g647,g648)
    c: Coincident(g648,g649)
    c: Coincident(g649,g650)
    c: Coincident(g650,g651)
    c: Coincident(g651,g652)
    c: Coincident(g652,g653)
    c: Coincident(g653,g654)
    c: Coincident(g654,g655)
    c: Coincident(g655,g656)
    c: Coincident(g656,g657)
    c: Coincident(g657,g658)
    c: Coincident(g658,g659)
    c: Coincident(g659,g660)
    c: Coincident(g660,g661)
    c: Coincident(g661,g662)
    c: Coincident(g662,g663)
    c: Coincident(g663,g664)
    c: Coincident(g664,g665)
    c: Coincident(g665,g666)
    c: Coincident(g666,g667)
    c: Coincident(g667,g668)
    c: Coincident(g668,g669)
    c: Coincident(g669,g670)
    c: Coincident(g670,g671)
    c: Coincident(g671,g672)
    c: Coincident(g672,g673)
    c: Coincident(g673,g674)
    c: Coincident(g674,g675)
    c: Coincident(g675,g676)
    c: Coincident(g676,g677)
    c: Coincident(g677,g678)
    c: Coincident(g678,g679)
    c: Coincident(g679,g680)
    c: Coincident(g680,g681)
    c: Coincident(g681,g682)
    c: Coincident(g682,g683)
    c: Coincident(g683,g684)
    c: Coincident(g684,g685)
    c: Coincident(g685,g686)
    c: Coincident(g686,g687)
    c: Coincident(g687,g688)
    c: Coincident(g688,g689)
    c: Coincident(g689,g690)
    c: Coincident(g690,g691)
    c: Coincident(g691,g692)
    c: Coincident(g692,g693)
    c: Coincident(g693,g694)
    c: Coincident(g694,g695)
    c: Coincident(g695,g696)
    c: Coincident(g696,g697)
    c: Coincident(g697,g698)
    c: Coincident(g698,g699)
    c: Coincident(g699,g700)
    c: Coincident(g700,g701)
    c: Coincident(g701,g702)
    c: Coincident(g702,g703)
    c: Coincident(g703,g704)
    c: Coincident(g704,g705)
    c: Coincident(g705,g706)
    c: Coincident(g706,g707)
    c: Coincident(g707,g708)
    c: Coincident(g708,g709)
    c: Coincident(g709,g710)
    c: Coincident(g710,g711)
    c: Coincident(g711,g712)
    c: Coincident(g712,g713)
    c: Coincident(g713,g714)
    c: Coincident(g714,g715)
    c: Coincident(g715,g716)
    c: Coincident(g716,g717)
    c: Coincident(g717,g718)
    c: Coincident(g718,g719)
    c: Coincident(g719,g720)
    c: Coincident(g720,g721)
    c: Coincident(g721,g722)
    c: Coincident(g722,g723)
    c: Coincident(g723,g724)
    c: Coincident(g724,g725)
    c: Coincident(g725,g726)
    c: Coincident(g726,g727)
    c: Coincident(g727,g728)
    c: Coincident(g728,g729)
    c: Coincident(g729,g730)
    c: Coincident(g730,g731)
    c: Coincident(g731,g732)
    c: Coincident(g732,g733)
    c: Coincident(g733,g734)
    c: Coincident(g734,g735)
    c: Coincident(g735,g736)
    c: Coincident(g736,g737)
    c: Coincident(g737,g738)
    c: Coincident(g738,g739)
    c: Coincident(g739,g740)
    c: Coincident(g740,g741)
    c: Coincident(g741,g742)
    c: Coincident(g742,g743)
    c: Coincident(g743,g744)
    c: Coincident(g744,g745)
    c: Coincident(g745,g746)
    c: Coincident(g746,g747)
    c: Coincident(g747,g748)
    c: Coincident(g748,g749)
    c: Coincident(g749,g750)
    c: Coincident(g750,g751)
    c: Coincident(g751,g752)
    c: Coincident(g752,g753)
    c: Coincident(g753,g754)
    c: Coincident(g754,g755)
    c: Coincident(g755,g756)
    c: Coincident(g756,g757)
    c: Coincident(g757,g758)
    c: Coincident(g758,g759)
    c: Coincident(g759,g531)
    c: Coincident(g760,g761)
    c: Coincident(g761,g762)
    c: Coincident(g762,g763)
    c: Coincident(g763,g764)
    c: Coincident(g764,g765)
    c: Coincident(g765,g766)
    c: Coincident(g766,g767)
    c: Coincident(g767,g768)
    c: Coincident(g768,g769)
    c: Coincident(g769,g770)
    c: Coincident(g770,g771)
    c: Coincident(g771,g772)
    c: Coincident(g772,g773)
    c: Coincident(g773,g774)
    c: Coincident(g774,g760)
FEATURE [Sketcher::SketchObject] Sketch022
  ExternalGeometry = -> [Pad011]
  FullyConstrained = true
  MapMode = 5
  Placement = pos=(0,-13.95,3.1e-15) rot=(1,0,0;1.5708rad)
  Support = -> [Pad011]
  sketch-geometry (12):
    g0: LineSegment StartX=-19 StartY=104.35 StartZ=0 EndX=19 EndY=104.35 EndZ=0
    g1: LineSegment StartX=19 StartY=104.35 StartZ=0 EndX=19 EndY=83.1 EndZ=0
    g2: LineSegment StartX=19 StartY=83.1 StartZ=0 EndX=-19 EndY=83.1 EndZ=0
    g3: LineSegment StartX=-19 StartY=83.1 StartZ=0 EndX=-19 EndY=104.35 EndZ=0
    g4: LineSegment StartX=-16.75 StartY=102.1 StartZ=0 EndX=16.75 EndY=102.1 EndZ=0
    g5: LineSegment StartX=16.75 StartY=102.1 StartZ=0 EndX=16.75 EndY=85.35 EndZ=0
    g6: LineSegment StartX=16.75 StartY=85.35 StartZ=0 EndX=-16.75 EndY=85.35 EndZ=0
    g7: LineSegment StartX=-16.75 StartY=85.35 StartZ=0 EndX=-16.75 EndY=102.1 EndZ=0
    g8: LineSegment StartX=-16.75 StartY=102.1 StartZ=0 EndX=-19 EndY=102.1 EndZ=0
    g9: LineSegment StartX=-16.75 StartY=102.1 StartZ=0 EndX=-16.75 EndY=104.35 EndZ=0
    g10: LineSegment StartX=16.75 StartY=85.35 StartZ=0 EndX=16.75 EndY=83.1 EndZ=0
    g11: LineSegment StartX=16.75 StartY=85.35 StartZ=0 EndX=19 EndY=85.35 EndZ=0
  constraints (34):
    c: Coincident(g0,g1)
    c: Coincident(g1,g2)
    c: Coincident(g2,g3)
    c: Coincident(g3,g0)
    c: Horizontal(g0)
    c: Horizontal(g2)
    c: Vertical(g1)
    c: Vertical(g3)
    c: Coincident(g0,g-3)
    c: Coincident(g1,g-5)
    c: Coincident(g4,g5)
    c: Coincident(g5,g6)
    c: Coincident(g6,g7)
    c: Coincident(g7,g4)
    c: Horizontal(g4)
    c: Horizontal(g6)
    c: Vertical(g5)
    c: Vertical(g7)
    c: Coincident(g8,g4)
    c: PointOnObject(g8,g3)
    c: Horizontal(g8)
    c: Coincident(g9,g4)
    c: PointOnObject(g9,g0)
    c: Vertical(g9)
    c: Coincident(g10,g5)
    c: PointOnObject(g10,g2)
    c: Vertical(g10)
    c: Coincident(g11,g5)
    c: PointOnObject(g11,g1)
    c: Horizontal(g11)
    c: Equal(g10,g11)
    c: Equal(g11,g9)
    c: Equal(g9,g8)
    c: DistanceY(g9,g9) = 2.25
FEATURE [PartDesign::Pocket] Pocket001
  BaseFeature = -> Pad011
  Direction = (0,1,-2e-16)
  Length = 0.1
  Length2 = 5
  Profile = -> Sketch022
  ReferenceAxis = -> Sketch022 [N_Axis]
  Type = 0
FEATURE [PartDesign::Body] Body022  label="trunk"
  Group = -> [Binder017,Binder018,Binder019,Sketch011,Pad011,Sketch022,Pocket001]
  Origin = -> Origin025
  Tip = -> Pocket001
FEATURE [App::DocumentObjectGroup] Group002  label="Acrylic_parts"
  Group = -> [Body,Body003,Body004,Body002,Body008,Body009,Body010,Body014,Body007,Body015,Body017,Body018,Body023,Body024,Body022]
FEATURE [Part::Part2DObjectPython] Shape2DView018  label="trunk_DXF"  # Draft 2D object (typed FeaturePython)
  AutoUpdate = true
  Base = -> Body022
  Clip = false
  FuseArch = false
  HiddenLines = false
  InPlace = true
  OnlySolids = false
  Projection = (0,-1,0)
  ProjectionMode = 0
  SegmentLength = 0.05
  Tessellation = false
  VisibleOnly = false
FEATURE [App::DocumentObjectGroup] Group004  label="DXF_acrylic"
  Group = -> [Shape2DView,Shape2DView001,Shape2DView002,Shape2DView003,Shape2DView004,Shape2DView005,Shape2DView006,Shape2DView007,Shape2DView008,Shape2DView009,Shape2DView010,Shape2DView011,Shape2DView012,Shape2DView013,Shape2DView014,Shape2DView015,Shape2DView016,Shape2DView018,Shape2DView019]
FEATURE [Spreadsheet::Sheet] Fasteners_BOM001  label="Fasteners_BOM"
  cells = A1='Type; B1='Qty; A2='DIN967 Screw M3x14; B2=4; A3='DIN967 Screw M3x30; B3=2; A4='ISO4032 Nut M3; B4=8; A5='ISO7045 Screw M2x10; B5=2; A6='ISO7093-1 Washer M3; B6=2; A7='Threaded Rod M3x70; B7=1
